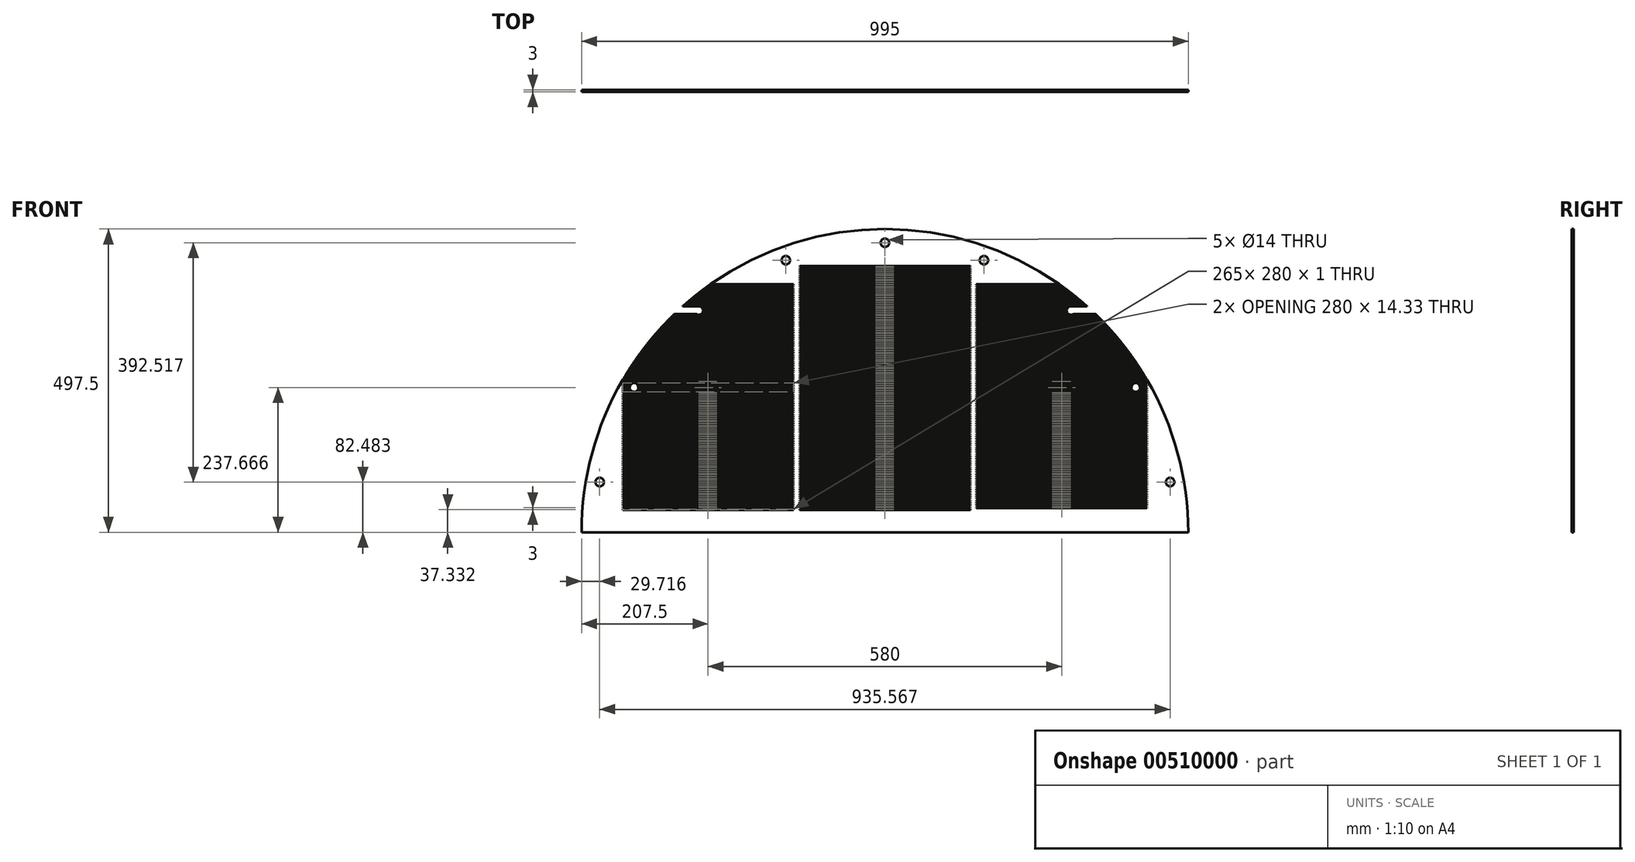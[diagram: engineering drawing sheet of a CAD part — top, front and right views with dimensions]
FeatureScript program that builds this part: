
annotation { "Feature Type Name" : "Feature", "Feature Type Description" : "" }
export const myFeature = defineFeature(function(context is Context, id is Id, definition is map)
    precondition{}
    {
        {
            var Q0;
            Q0=qCreatedBy(makeId("Front.planeOp"),FACE);
            var sketch = newSketch(context, id + "F0", { "sketchPlane" : qUnion([Q0])});
            skArc(sketch, "E0", {"start": v(497.5, 0) * mm, "mid": v(0, 497.5) * mm, "end": v(-497.5, 0) * mm});
            skLineSegment(sketch, "E1", {"start": v(-497.5, 0) * mm, "end": v(497.5, 0) * mm});
            skSolve(sketch);
        }
        {
            var Q0;
            Q0=makeQuery(id+"F0.imprint","IMPRINT",FACE,{"disambiguationData":[TD([[makeQuery(id+"F0.imprint","IMPRINT",EDGE,{"derivedFrom":sQuery(id+"F0.wireOp",EDGE,"E0")}),1.0]])]});
            extrude(context, id + "F1", {"entities" : qUnion([Q0]), "depth" : 3 * mm});
        }
        {
            var Q0;
            Q0=makeQuery(id+"F1.opExtrude","CAP_FACE",FACE,{"disambiguationData":[OSD([sQuery(id+"F0.wireOp",EDGE,"E0"),sQuery(id+"F0.wireOp",EDGE,"E1")])],"isStart":false});
            var sketch = newSketch(context, id + "F2", { "sketchPlane" : qUnion([Q0])});
            skCircle(sketch, "E2", {"center": v(0, 0) * mm, "radius": 475 * mm, "construction": true});
            skLineSegment(sketch, "E3", {"start": v(0, 0) * mm, "end": v(-467.78, 82.48) * mm});
            skCircle(sketch, "E4", {"center": v(-467.78, 82.48) * mm, "radius": 7 * mm});
            skCircle(sketch, "E5.1.0", {"center": v(-411.36, 237.5) * mm, "radius": 7 * mm});
            skCircle(sketch, "E5.2.0", {"center": v(-305.32, 363.87) * mm, "radius": 7 * mm});
            skCircle(sketch, "E5.3.0", {"center": v(-162.46, 446.35) * mm, "radius": 7 * mm});
            skCircle(sketch, "E5.4.0", {"center": v(0, 475) * mm, "radius": 7 * mm});
            skCircle(sketch, "E5.5.0", {"center": v(162.46, 446.35) * mm, "radius": 7 * mm});
            skCircle(sketch, "E5.6.0", {"center": v(305.32, 363.87) * mm, "radius": 7 * mm});
            skCircle(sketch, "E5.7.0", {"center": v(411.36, 237.5) * mm, "radius": 7 * mm});
            skCircle(sketch, "E5.8.0", {"center": v(467.78, 82.48) * mm, "radius": 7 * mm});
            skLineSegment(sketch, "E5.anchor1", {"start": v(0, 0) * mm, "end": v(-467.78, 82.48) * mm, "construction": true});
            skLineSegment(sketch, "E5.anchor2", {"start": v(0, 0) * mm, "end": v(467.78, 82.48) * mm, "construction": true});
            skSolve(sketch);
        }
        {
            var Q0;
            Q0=makeQuery(id+"F2.imprint","IMPRINT",FACE,{"disambiguationData":[TD([[makeQuery(id+"F2.imprint","IMPRINT",EDGE,{"derivedFrom":sQuery(id+"F2.wireOp",EDGE,"E4")}),-1.0]])]});
            extrude(context, id + "F3", {"entities" : qUnion([Q0]), "operationType" : NewBodyOperationType.INTERSECT, "oppositeDirection" : true, "depth" : 25 * mm});
        }
        {
            var Q0;
            Q0=makeQuery(id+"F1.opExtrude","CAP_FACE",FACE,{"disambiguationData":[OSD([sQuery(id+"F0.wireOp",EDGE,"E0"),sQuery(id+"F0.wireOp",EDGE,"E1")])],"isStart":false});
            var sketch = newSketch(context, id + "F4", { "sketchPlane" : qUnion([Q0])});
            skSolve(sketch);
        }
        {
            var Q0;
            Q0=makeQuery(id+"F4.imprint","IMPRINT",FACE,{"disambiguationData":[TD([[makeQuery(id+"F4.imprint","IMPRINT",EDGE,{"derivedFrom":makeQuery(id+"F1.opExtrude","CAP_EDGE",EDGE,{"disambiguationData":[OSD([sQuery(id+"F0.wireOp",EDGE,"E0")])],"isStart":false})}),1.0]])]});
            var sketch = newSketch(context, id + "F5", { "sketchPlane" : qUnion([Q0])});
            skLineSegment(sketch, "E6.bottom", {"start": v(-430, 37.83) * mm, "end": v(-150, 37.83) * mm});
            skLineSegment(sketch, "E6.top", {"start": v(-430, 36.83) * mm, "end": v(-150, 36.83) * mm});
            skLineSegment(sketch, "E6.left", {"start": v(-430, 37.83) * mm, "end": v(-430, 36.83) * mm});
            skLineSegment(sketch, "E6.right", {"start": v(-150, 37.83) * mm, "end": v(-150, 36.83) * mm});
            skLineSegment(sketch, "E7.bottom", {"start": v(-140, 36.83) * mm, "end": v(140, 36.83) * mm});
            skLineSegment(sketch, "E7.top", {"start": v(-140, 37.83) * mm, "end": v(140, 37.83) * mm});
            skLineSegment(sketch, "E7.left", {"start": v(-140, 36.83) * mm, "end": v(-140, 37.83) * mm});
            skLineSegment(sketch, "E7.right", {"start": v(140, 36.83) * mm, "end": v(140, 37.83) * mm});
            skLineSegment(sketch, "E8.bottom", {"start": v(150, 36.83) * mm, "end": v(430, 36.83) * mm});
            skLineSegment(sketch, "E8.top", {"start": v(150, 37.83) * mm, "end": v(430, 37.83) * mm});
            skLineSegment(sketch, "E8.left", {"start": v(150, 36.83) * mm, "end": v(150, 37.83) * mm});
            skLineSegment(sketch, "E9.0.1.0", {"start": v(150, 40.83) * mm, "end": v(429.64, 40.83) * mm});
            skLineSegment(sketch, "E9.0.1.1", {"start": v(-140, 40.83) * mm, "end": v(140, 40.83) * mm});
            skLineSegment(sketch, "E9.0.1.2", {"start": v(-430, 39.83) * mm, "end": v(-150, 39.83) * mm});
            skLineSegment(sketch, "E9.0.1.3", {"start": v(150, 39.83) * mm, "end": v(429.73, 39.83) * mm});
            skLineSegment(sketch, "E9.0.1.4", {"start": v(-140, 39.83) * mm, "end": v(140, 39.83) * mm});
            skLineSegment(sketch, "E9.0.1.5", {"start": v(-430, 40.83) * mm, "end": v(-150, 40.83) * mm});
            skLineSegment(sketch, "E9.0.1.7", {"start": v(150, 39.83) * mm, "end": v(150, 40.83) * mm});
            skLineSegment(sketch, "E9.0.1.8", {"start": v(140, 39.83) * mm, "end": v(140, 40.83) * mm});
            skLineSegment(sketch, "E9.0.1.9", {"start": v(-140, 39.83) * mm, "end": v(-140, 40.83) * mm});
            skLineSegment(sketch, "E9.0.1.10", {"start": v(-150, 40.83) * mm, "end": v(-150, 39.83) * mm});
            skLineSegment(sketch, "E9.0.1.11", {"start": v(-430, 40.83) * mm, "end": v(-430, 39.83) * mm});
            skLineSegment(sketch, "E9.0.2.0", {"start": v(150, 43.83) * mm, "end": v(429.34, 43.83) * mm});
            skLineSegment(sketch, "E9.0.2.1", {"start": v(-140, 43.83) * mm, "end": v(140, 43.83) * mm});
            skLineSegment(sketch, "E9.0.2.2", {"start": v(-430, 42.83) * mm, "end": v(-150, 42.83) * mm});
            skLineSegment(sketch, "E9.0.2.3", {"start": v(150, 42.83) * mm, "end": v(429.44, 42.83) * mm});
            skLineSegment(sketch, "E9.0.2.4", {"start": v(-140, 42.83) * mm, "end": v(140, 42.83) * mm});
            skLineSegment(sketch, "E9.0.2.5", {"start": v(-430, 43.83) * mm, "end": v(-150, 43.83) * mm});
            skLineSegment(sketch, "E9.0.2.7", {"start": v(150, 42.83) * mm, "end": v(150, 43.83) * mm});
            skLineSegment(sketch, "E9.0.2.8", {"start": v(140, 42.83) * mm, "end": v(140, 43.83) * mm});
            skLineSegment(sketch, "E9.0.2.9", {"start": v(-140, 42.83) * mm, "end": v(-140, 43.83) * mm});
            skLineSegment(sketch, "E9.0.2.10", {"start": v(-150, 43.83) * mm, "end": v(-150, 42.83) * mm});
            skLineSegment(sketch, "E9.0.2.11", {"start": v(-430, 43.83) * mm, "end": v(-430, 42.83) * mm});
            skLineSegment(sketch, "E9.0.3.0", {"start": v(150, 46.83) * mm, "end": v(429.03, 46.83) * mm});
            skLineSegment(sketch, "E9.0.3.1", {"start": v(-140, 46.83) * mm, "end": v(140, 46.83) * mm});
            skLineSegment(sketch, "E9.0.3.2", {"start": v(-430, 45.83) * mm, "end": v(-150, 45.83) * mm});
            skLineSegment(sketch, "E9.0.3.3", {"start": v(150, 45.83) * mm, "end": v(429.13, 45.83) * mm});
            skLineSegment(sketch, "E9.0.3.4", {"start": v(-140, 45.83) * mm, "end": v(140, 45.83) * mm});
            skLineSegment(sketch, "E9.0.3.5", {"start": v(-430, 46.83) * mm, "end": v(-150, 46.83) * mm});
            skLineSegment(sketch, "E9.0.3.7", {"start": v(150, 45.83) * mm, "end": v(150, 46.83) * mm});
            skLineSegment(sketch, "E9.0.3.8", {"start": v(140, 45.83) * mm, "end": v(140, 46.83) * mm});
            skLineSegment(sketch, "E9.0.3.9", {"start": v(-140, 45.83) * mm, "end": v(-140, 46.83) * mm});
            skLineSegment(sketch, "E9.0.3.10", {"start": v(-150, 46.83) * mm, "end": v(-150, 45.83) * mm});
            skLineSegment(sketch, "E9.0.3.11", {"start": v(-430, 46.83) * mm, "end": v(-430, 45.83) * mm});
            skLineSegment(sketch, "E9.0.4.0", {"start": v(150, 49.83) * mm, "end": v(430, 49.83) * mm});
            skLineSegment(sketch, "E9.0.4.1", {"start": v(-140, 49.83) * mm, "end": v(140, 49.83) * mm});
            skLineSegment(sketch, "E9.0.4.2", {"start": v(-430, 48.83) * mm, "end": v(-150, 48.83) * mm});
            skLineSegment(sketch, "E9.0.4.3", {"start": v(150, 48.83) * mm, "end": v(430, 48.83) * mm});
            skLineSegment(sketch, "E9.0.4.4", {"start": v(-140, 48.83) * mm, "end": v(140, 48.83) * mm});
            skLineSegment(sketch, "E9.0.4.5", {"start": v(-430, 49.83) * mm, "end": v(-150, 49.83) * mm});
            skLineSegment(sketch, "E9.0.4.6", {"start": v(430, 48.83) * mm, "end": v(430, 49.83) * mm});
            skLineSegment(sketch, "E9.0.4.7", {"start": v(150, 48.83) * mm, "end": v(150, 49.83) * mm});
            skLineSegment(sketch, "E9.0.4.8", {"start": v(140, 48.83) * mm, "end": v(140, 49.83) * mm});
            skLineSegment(sketch, "E9.0.4.9", {"start": v(-140, 48.83) * mm, "end": v(-140, 49.83) * mm});
            skLineSegment(sketch, "E9.0.4.10", {"start": v(-150, 49.83) * mm, "end": v(-150, 48.83) * mm});
            skLineSegment(sketch, "E9.0.4.11", {"start": v(-430, 49.83) * mm, "end": v(-430, 48.83) * mm});
            skLineSegment(sketch, "E9.0.5.0", {"start": v(150, 52.83) * mm, "end": v(430, 52.83) * mm});
            skLineSegment(sketch, "E9.0.5.1", {"start": v(-140, 52.83) * mm, "end": v(140, 52.83) * mm});
            skLineSegment(sketch, "E9.0.5.2", {"start": v(-430, 51.83) * mm, "end": v(-150, 51.83) * mm});
            skLineSegment(sketch, "E9.0.5.3", {"start": v(150, 51.83) * mm, "end": v(430, 51.83) * mm});
            skLineSegment(sketch, "E9.0.5.4", {"start": v(-140, 51.83) * mm, "end": v(140, 51.83) * mm});
            skLineSegment(sketch, "E9.0.5.5", {"start": v(-430, 52.83) * mm, "end": v(-150, 52.83) * mm});
            skLineSegment(sketch, "E9.0.5.6", {"start": v(430, 51.83) * mm, "end": v(430, 52.83) * mm});
            skLineSegment(sketch, "E9.0.5.7", {"start": v(150, 51.83) * mm, "end": v(150, 52.83) * mm});
            skLineSegment(sketch, "E9.0.5.8", {"start": v(140, 51.83) * mm, "end": v(140, 52.83) * mm});
            skLineSegment(sketch, "E9.0.5.9", {"start": v(-140, 51.83) * mm, "end": v(-140, 52.83) * mm});
            skLineSegment(sketch, "E9.0.5.10", {"start": v(-150, 52.83) * mm, "end": v(-150, 51.83) * mm});
            skLineSegment(sketch, "E9.0.5.11", {"start": v(-430, 52.83) * mm, "end": v(-430, 51.83) * mm});
            skLineSegment(sketch, "E9.0.6.0", {"start": v(150, 55.83) * mm, "end": v(430, 55.83) * mm});
            skLineSegment(sketch, "E9.0.6.1", {"start": v(-140, 55.83) * mm, "end": v(140, 55.83) * mm});
            skLineSegment(sketch, "E9.0.6.2", {"start": v(-430, 54.83) * mm, "end": v(-150, 54.83) * mm});
            skLineSegment(sketch, "E9.0.6.3", {"start": v(150, 54.83) * mm, "end": v(430, 54.83) * mm});
            skLineSegment(sketch, "E9.0.6.4", {"start": v(-140, 54.83) * mm, "end": v(140, 54.83) * mm});
            skLineSegment(sketch, "E9.0.6.5", {"start": v(-430, 55.83) * mm, "end": v(-150, 55.83) * mm});
            skLineSegment(sketch, "E9.0.6.6", {"start": v(430, 54.83) * mm, "end": v(430, 55.83) * mm});
            skLineSegment(sketch, "E9.0.6.7", {"start": v(150, 54.83) * mm, "end": v(150, 55.83) * mm});
            skLineSegment(sketch, "E9.0.6.8", {"start": v(140, 54.83) * mm, "end": v(140, 55.83) * mm});
            skLineSegment(sketch, "E9.0.6.9", {"start": v(-140, 54.83) * mm, "end": v(-140, 55.83) * mm});
            skLineSegment(sketch, "E9.0.6.10", {"start": v(-150, 55.83) * mm, "end": v(-150, 54.83) * mm});
            skLineSegment(sketch, "E9.0.6.11", {"start": v(-430, 55.83) * mm, "end": v(-430, 54.83) * mm});
            skLineSegment(sketch, "E9.0.7.0", {"start": v(150, 58.83) * mm, "end": v(430, 58.83) * mm});
            skLineSegment(sketch, "E9.0.7.1", {"start": v(-140, 58.83) * mm, "end": v(140, 58.83) * mm});
            skLineSegment(sketch, "E9.0.7.2", {"start": v(-430, 57.83) * mm, "end": v(-150, 57.83) * mm});
            skLineSegment(sketch, "E9.0.7.3", {"start": v(150, 57.83) * mm, "end": v(430, 57.83) * mm});
            skLineSegment(sketch, "E9.0.7.4", {"start": v(-140, 57.83) * mm, "end": v(140, 57.83) * mm});
            skLineSegment(sketch, "E9.0.7.5", {"start": v(-430, 58.83) * mm, "end": v(-150, 58.83) * mm});
            skLineSegment(sketch, "E9.0.7.6", {"start": v(430, 57.83) * mm, "end": v(430, 58.83) * mm});
            skLineSegment(sketch, "E9.0.7.7", {"start": v(150, 57.83) * mm, "end": v(150, 58.83) * mm});
            skLineSegment(sketch, "E9.0.7.8", {"start": v(140, 57.83) * mm, "end": v(140, 58.83) * mm});
            skLineSegment(sketch, "E9.0.7.9", {"start": v(-140, 57.83) * mm, "end": v(-140, 58.83) * mm});
            skLineSegment(sketch, "E9.0.7.10", {"start": v(-150, 58.83) * mm, "end": v(-150, 57.83) * mm});
            skLineSegment(sketch, "E9.0.7.11", {"start": v(-430, 58.83) * mm, "end": v(-430, 57.83) * mm});
            skLineSegment(sketch, "E9.0.8.0", {"start": v(150, 61.83) * mm, "end": v(430, 61.83) * mm});
            skLineSegment(sketch, "E9.0.8.1", {"start": v(-140, 61.83) * mm, "end": v(140, 61.83) * mm});
            skLineSegment(sketch, "E9.0.8.2", {"start": v(-430, 60.83) * mm, "end": v(-150, 60.83) * mm});
            skLineSegment(sketch, "E9.0.8.3", {"start": v(150, 60.83) * mm, "end": v(430, 60.83) * mm});
            skLineSegment(sketch, "E9.0.8.4", {"start": v(-140, 60.83) * mm, "end": v(140, 60.83) * mm});
            skLineSegment(sketch, "E9.0.8.5", {"start": v(-430, 61.83) * mm, "end": v(-150, 61.83) * mm});
            skLineSegment(sketch, "E9.0.8.6", {"start": v(430, 60.83) * mm, "end": v(430, 61.83) * mm});
            skLineSegment(sketch, "E9.0.8.7", {"start": v(150, 60.83) * mm, "end": v(150, 61.83) * mm});
            skLineSegment(sketch, "E9.0.8.8", {"start": v(140, 60.83) * mm, "end": v(140, 61.83) * mm});
            skLineSegment(sketch, "E9.0.8.9", {"start": v(-140, 60.83) * mm, "end": v(-140, 61.83) * mm});
            skLineSegment(sketch, "E9.0.8.10", {"start": v(-150, 61.83) * mm, "end": v(-150, 60.83) * mm});
            skLineSegment(sketch, "E9.0.8.11", {"start": v(-430, 61.83) * mm, "end": v(-430, 60.83) * mm});
            skLineSegment(sketch, "E9.0.9.0", {"start": v(150, 64.83) * mm, "end": v(430, 64.83) * mm});
            skLineSegment(sketch, "E9.0.9.1", {"start": v(-140, 64.83) * mm, "end": v(140, 64.83) * mm});
            skLineSegment(sketch, "E9.0.9.2", {"start": v(-430, 63.83) * mm, "end": v(-150, 63.83) * mm});
            skLineSegment(sketch, "E9.0.9.3", {"start": v(150, 63.83) * mm, "end": v(430, 63.83) * mm});
            skLineSegment(sketch, "E9.0.9.4", {"start": v(-140, 63.83) * mm, "end": v(140, 63.83) * mm});
            skLineSegment(sketch, "E9.0.9.5", {"start": v(-430, 64.83) * mm, "end": v(-150, 64.83) * mm});
            skLineSegment(sketch, "E9.0.9.6", {"start": v(430, 63.83) * mm, "end": v(430, 64.83) * mm});
            skLineSegment(sketch, "E9.0.9.7", {"start": v(150, 63.83) * mm, "end": v(150, 64.83) * mm});
            skLineSegment(sketch, "E9.0.9.8", {"start": v(140, 63.83) * mm, "end": v(140, 64.83) * mm});
            skLineSegment(sketch, "E9.0.9.9", {"start": v(-140, 63.83) * mm, "end": v(-140, 64.83) * mm});
            skLineSegment(sketch, "E9.0.9.10", {"start": v(-150, 64.83) * mm, "end": v(-150, 63.83) * mm});
            skLineSegment(sketch, "E9.0.9.11", {"start": v(-430, 64.83) * mm, "end": v(-430, 63.83) * mm});
            skLineSegment(sketch, "E9.0.10.0", {"start": v(150, 67.83) * mm, "end": v(430, 67.83) * mm});
            skLineSegment(sketch, "E9.0.10.1", {"start": v(-140, 67.83) * mm, "end": v(140, 67.83) * mm});
            skLineSegment(sketch, "E9.0.10.2", {"start": v(-430, 66.83) * mm, "end": v(-150, 66.83) * mm});
            skLineSegment(sketch, "E9.0.10.3", {"start": v(150, 66.83) * mm, "end": v(430, 66.83) * mm});
            skLineSegment(sketch, "E9.0.10.4", {"start": v(-140, 66.83) * mm, "end": v(140, 66.83) * mm});
            skLineSegment(sketch, "E9.0.10.5", {"start": v(-430, 67.83) * mm, "end": v(-150, 67.83) * mm});
            skLineSegment(sketch, "E9.0.10.6", {"start": v(430, 66.83) * mm, "end": v(430, 67.83) * mm});
            skLineSegment(sketch, "E9.0.10.7", {"start": v(150, 66.83) * mm, "end": v(150, 67.83) * mm});
            skLineSegment(sketch, "E9.0.10.8", {"start": v(140, 66.83) * mm, "end": v(140, 67.83) * mm});
            skLineSegment(sketch, "E9.0.10.9", {"start": v(-140, 66.83) * mm, "end": v(-140, 67.83) * mm});
            skLineSegment(sketch, "E9.0.10.10", {"start": v(-150, 67.83) * mm, "end": v(-150, 66.83) * mm});
            skLineSegment(sketch, "E9.0.10.11", {"start": v(-430, 67.83) * mm, "end": v(-430, 66.83) * mm});
            skLineSegment(sketch, "E9.0.11.0", {"start": v(150, 70.83) * mm, "end": v(430, 70.83) * mm});
            skLineSegment(sketch, "E9.0.11.1", {"start": v(-140, 70.83) * mm, "end": v(140, 70.83) * mm});
            skLineSegment(sketch, "E9.0.11.2", {"start": v(-430, 69.83) * mm, "end": v(-150, 69.83) * mm});
            skLineSegment(sketch, "E9.0.11.3", {"start": v(150, 69.83) * mm, "end": v(430, 69.83) * mm});
            skLineSegment(sketch, "E9.0.11.4", {"start": v(-140, 69.83) * mm, "end": v(140, 69.83) * mm});
            skLineSegment(sketch, "E9.0.11.5", {"start": v(-430, 70.83) * mm, "end": v(-150, 70.83) * mm});
            skLineSegment(sketch, "E9.0.11.6", {"start": v(430, 69.83) * mm, "end": v(430, 70.83) * mm});
            skLineSegment(sketch, "E9.0.11.7", {"start": v(150, 69.83) * mm, "end": v(150, 70.83) * mm});
            skLineSegment(sketch, "E9.0.11.8", {"start": v(140, 69.83) * mm, "end": v(140, 70.83) * mm});
            skLineSegment(sketch, "E9.0.11.9", {"start": v(-140, 69.83) * mm, "end": v(-140, 70.83) * mm});
            skLineSegment(sketch, "E9.0.11.10", {"start": v(-150, 70.83) * mm, "end": v(-150, 69.83) * mm});
            skLineSegment(sketch, "E9.0.11.11", {"start": v(-430, 70.83) * mm, "end": v(-430, 69.83) * mm});
            skLineSegment(sketch, "E9.0.12.0", {"start": v(150, 73.83) * mm, "end": v(430, 73.83) * mm});
            skLineSegment(sketch, "E9.0.12.1", {"start": v(-140, 73.83) * mm, "end": v(140, 73.83) * mm});
            skLineSegment(sketch, "E9.0.12.2", {"start": v(-430, 72.83) * mm, "end": v(-150, 72.83) * mm});
            skLineSegment(sketch, "E9.0.12.3", {"start": v(150, 72.83) * mm, "end": v(430, 72.83) * mm});
            skLineSegment(sketch, "E9.0.12.4", {"start": v(-140, 72.83) * mm, "end": v(140, 72.83) * mm});
            skLineSegment(sketch, "E9.0.12.5", {"start": v(-430, 73.83) * mm, "end": v(-150, 73.83) * mm});
            skLineSegment(sketch, "E9.0.12.6", {"start": v(430, 72.83) * mm, "end": v(430, 73.83) * mm});
            skLineSegment(sketch, "E9.0.12.7", {"start": v(150, 72.83) * mm, "end": v(150, 73.83) * mm});
            skLineSegment(sketch, "E9.0.12.8", {"start": v(140, 72.83) * mm, "end": v(140, 73.83) * mm});
            skLineSegment(sketch, "E9.0.12.9", {"start": v(-140, 72.83) * mm, "end": v(-140, 73.83) * mm});
            skLineSegment(sketch, "E9.0.12.10", {"start": v(-150, 73.83) * mm, "end": v(-150, 72.83) * mm});
            skLineSegment(sketch, "E9.0.12.11", {"start": v(-430, 73.83) * mm, "end": v(-430, 72.83) * mm});
            skLineSegment(sketch, "E9.0.13.0", {"start": v(150, 76.83) * mm, "end": v(430, 76.83) * mm});
            skLineSegment(sketch, "E9.0.13.1", {"start": v(-140, 76.83) * mm, "end": v(140, 76.83) * mm});
            skLineSegment(sketch, "E9.0.13.2", {"start": v(-430, 75.83) * mm, "end": v(-150, 75.83) * mm});
            skLineSegment(sketch, "E9.0.13.3", {"start": v(150, 75.83) * mm, "end": v(430, 75.83) * mm});
            skLineSegment(sketch, "E9.0.13.4", {"start": v(-140, 75.83) * mm, "end": v(140, 75.83) * mm});
            skLineSegment(sketch, "E9.0.13.5", {"start": v(-430, 76.83) * mm, "end": v(-150, 76.83) * mm});
            skLineSegment(sketch, "E9.0.13.6", {"start": v(430, 75.83) * mm, "end": v(430, 76.83) * mm});
            skLineSegment(sketch, "E9.0.13.7", {"start": v(150, 75.83) * mm, "end": v(150, 76.83) * mm});
            skLineSegment(sketch, "E9.0.13.8", {"start": v(140, 75.83) * mm, "end": v(140, 76.83) * mm});
            skLineSegment(sketch, "E9.0.13.9", {"start": v(-140, 75.83) * mm, "end": v(-140, 76.83) * mm});
            skLineSegment(sketch, "E9.0.13.10", {"start": v(-150, 76.83) * mm, "end": v(-150, 75.83) * mm});
            skLineSegment(sketch, "E9.0.13.11", {"start": v(-430, 76.83) * mm, "end": v(-430, 75.83) * mm});
            skLineSegment(sketch, "E9.0.14.0", {"start": v(150, 79.83) * mm, "end": v(430, 79.83) * mm});
            skLineSegment(sketch, "E9.0.14.1", {"start": v(-140, 79.83) * mm, "end": v(140, 79.83) * mm});
            skLineSegment(sketch, "E9.0.14.2", {"start": v(-430, 78.83) * mm, "end": v(-150, 78.83) * mm});
            skLineSegment(sketch, "E9.0.14.3", {"start": v(150, 78.83) * mm, "end": v(430, 78.83) * mm});
            skLineSegment(sketch, "E9.0.14.4", {"start": v(-140, 78.83) * mm, "end": v(140, 78.83) * mm});
            skLineSegment(sketch, "E9.0.14.5", {"start": v(-430, 79.83) * mm, "end": v(-150, 79.83) * mm});
            skLineSegment(sketch, "E9.0.14.6", {"start": v(430, 78.83) * mm, "end": v(430, 79.83) * mm});
            skLineSegment(sketch, "E9.0.14.7", {"start": v(150, 78.83) * mm, "end": v(150, 79.83) * mm});
            skLineSegment(sketch, "E9.0.14.8", {"start": v(140, 78.83) * mm, "end": v(140, 79.83) * mm});
            skLineSegment(sketch, "E9.0.14.9", {"start": v(-140, 78.83) * mm, "end": v(-140, 79.83) * mm});
            skLineSegment(sketch, "E9.0.14.10", {"start": v(-150, 79.83) * mm, "end": v(-150, 78.83) * mm});
            skLineSegment(sketch, "E9.0.14.11", {"start": v(-430, 79.83) * mm, "end": v(-430, 78.83) * mm});
            skLineSegment(sketch, "E9.0.15.0", {"start": v(150, 82.83) * mm, "end": v(430, 82.83) * mm});
            skLineSegment(sketch, "E9.0.15.1", {"start": v(-140, 82.83) * mm, "end": v(140, 82.83) * mm});
            skLineSegment(sketch, "E9.0.15.2", {"start": v(-430, 81.83) * mm, "end": v(-150, 81.83) * mm});
            skLineSegment(sketch, "E9.0.15.3", {"start": v(150, 81.83) * mm, "end": v(430, 81.83) * mm});
            skLineSegment(sketch, "E9.0.15.4", {"start": v(-140, 81.83) * mm, "end": v(140, 81.83) * mm});
            skLineSegment(sketch, "E9.0.15.5", {"start": v(-430, 82.83) * mm, "end": v(-150, 82.83) * mm});
            skLineSegment(sketch, "E9.0.15.6", {"start": v(430, 81.83) * mm, "end": v(430, 82.83) * mm});
            skLineSegment(sketch, "E9.0.15.7", {"start": v(150, 81.83) * mm, "end": v(150, 82.83) * mm});
            skLineSegment(sketch, "E9.0.15.8", {"start": v(140, 81.83) * mm, "end": v(140, 82.83) * mm});
            skLineSegment(sketch, "E9.0.15.9", {"start": v(-140, 81.83) * mm, "end": v(-140, 82.83) * mm});
            skLineSegment(sketch, "E9.0.15.10", {"start": v(-150, 82.83) * mm, "end": v(-150, 81.83) * mm});
            skLineSegment(sketch, "E9.0.15.11", {"start": v(-430, 82.83) * mm, "end": v(-430, 81.83) * mm});
            skLineSegment(sketch, "E9.0.16.0", {"start": v(150, 85.83) * mm, "end": v(430, 85.83) * mm});
            skLineSegment(sketch, "E9.0.16.1", {"start": v(-140, 85.83) * mm, "end": v(140, 85.83) * mm});
            skLineSegment(sketch, "E9.0.16.2", {"start": v(-430, 84.83) * mm, "end": v(-150, 84.83) * mm});
            skLineSegment(sketch, "E9.0.16.3", {"start": v(150, 84.83) * mm, "end": v(430, 84.83) * mm});
            skLineSegment(sketch, "E9.0.16.4", {"start": v(-140, 84.83) * mm, "end": v(140, 84.83) * mm});
            skLineSegment(sketch, "E9.0.16.5", {"start": v(-430, 85.83) * mm, "end": v(-150, 85.83) * mm});
            skLineSegment(sketch, "E9.0.16.6", {"start": v(430, 84.83) * mm, "end": v(430, 85.83) * mm});
            skLineSegment(sketch, "E9.0.16.7", {"start": v(150, 84.83) * mm, "end": v(150, 85.83) * mm});
            skLineSegment(sketch, "E9.0.16.8", {"start": v(140, 84.83) * mm, "end": v(140, 85.83) * mm});
            skLineSegment(sketch, "E9.0.16.9", {"start": v(-140, 84.83) * mm, "end": v(-140, 85.83) * mm});
            skLineSegment(sketch, "E9.0.16.10", {"start": v(-150, 85.83) * mm, "end": v(-150, 84.83) * mm});
            skLineSegment(sketch, "E9.0.16.11", {"start": v(-430, 85.83) * mm, "end": v(-430, 84.83) * mm});
            skLineSegment(sketch, "E9.0.17.0", {"start": v(150, 88.83) * mm, "end": v(430, 88.83) * mm});
            skLineSegment(sketch, "E9.0.17.1", {"start": v(-140, 88.83) * mm, "end": v(140, 88.83) * mm});
            skLineSegment(sketch, "E9.0.17.2", {"start": v(-430, 87.83) * mm, "end": v(-150, 87.83) * mm});
            skLineSegment(sketch, "E9.0.17.3", {"start": v(150, 87.83) * mm, "end": v(430, 87.83) * mm});
            skLineSegment(sketch, "E9.0.17.4", {"start": v(-140, 87.83) * mm, "end": v(140, 87.83) * mm});
            skLineSegment(sketch, "E9.0.17.5", {"start": v(-430, 88.83) * mm, "end": v(-150, 88.83) * mm});
            skLineSegment(sketch, "E9.0.17.6", {"start": v(430, 87.83) * mm, "end": v(430, 88.83) * mm});
            skLineSegment(sketch, "E9.0.17.7", {"start": v(150, 87.83) * mm, "end": v(150, 88.83) * mm});
            skLineSegment(sketch, "E9.0.17.8", {"start": v(140, 87.83) * mm, "end": v(140, 88.83) * mm});
            skLineSegment(sketch, "E9.0.17.9", {"start": v(-140, 87.83) * mm, "end": v(-140, 88.83) * mm});
            skLineSegment(sketch, "E9.0.17.10", {"start": v(-150, 88.83) * mm, "end": v(-150, 87.83) * mm});
            skLineSegment(sketch, "E9.0.17.11", {"start": v(-430, 88.83) * mm, "end": v(-430, 87.83) * mm});
            skLineSegment(sketch, "E9.0.18.0", {"start": v(150, 91.83) * mm, "end": v(430, 91.83) * mm});
            skLineSegment(sketch, "E9.0.18.1", {"start": v(-140, 91.83) * mm, "end": v(140, 91.83) * mm});
            skLineSegment(sketch, "E9.0.18.2", {"start": v(-430, 90.83) * mm, "end": v(-150, 90.83) * mm});
            skLineSegment(sketch, "E9.0.18.3", {"start": v(150, 90.83) * mm, "end": v(430, 90.83) * mm});
            skLineSegment(sketch, "E9.0.18.4", {"start": v(-140, 90.83) * mm, "end": v(140, 90.83) * mm});
            skLineSegment(sketch, "E9.0.18.5", {"start": v(-430, 91.83) * mm, "end": v(-150, 91.83) * mm});
            skLineSegment(sketch, "E9.0.18.6", {"start": v(430, 90.83) * mm, "end": v(430, 91.83) * mm});
            skLineSegment(sketch, "E9.0.18.7", {"start": v(150, 90.83) * mm, "end": v(150, 91.83) * mm});
            skLineSegment(sketch, "E9.0.18.8", {"start": v(140, 90.83) * mm, "end": v(140, 91.83) * mm});
            skLineSegment(sketch, "E9.0.18.9", {"start": v(-140, 90.83) * mm, "end": v(-140, 91.83) * mm});
            skLineSegment(sketch, "E9.0.18.10", {"start": v(-150, 91.83) * mm, "end": v(-150, 90.83) * mm});
            skLineSegment(sketch, "E9.0.18.11", {"start": v(-430, 91.83) * mm, "end": v(-430, 90.83) * mm});
            skLineSegment(sketch, "E9.0.19.0", {"start": v(150, 94.83) * mm, "end": v(430, 94.83) * mm});
            skLineSegment(sketch, "E9.0.19.1", {"start": v(-140, 94.83) * mm, "end": v(140, 94.83) * mm});
            skLineSegment(sketch, "E9.0.19.2", {"start": v(-430, 93.83) * mm, "end": v(-150, 93.83) * mm});
            skLineSegment(sketch, "E9.0.19.3", {"start": v(150, 93.83) * mm, "end": v(430, 93.83) * mm});
            skLineSegment(sketch, "E9.0.19.4", {"start": v(-140, 93.83) * mm, "end": v(140, 93.83) * mm});
            skLineSegment(sketch, "E9.0.19.5", {"start": v(-430, 94.83) * mm, "end": v(-150, 94.83) * mm});
            skLineSegment(sketch, "E9.0.19.6", {"start": v(430, 93.83) * mm, "end": v(430, 94.83) * mm});
            skLineSegment(sketch, "E9.0.19.7", {"start": v(150, 93.83) * mm, "end": v(150, 94.83) * mm});
            skLineSegment(sketch, "E9.0.19.8", {"start": v(140, 93.83) * mm, "end": v(140, 94.83) * mm});
            skLineSegment(sketch, "E9.0.19.9", {"start": v(-140, 93.83) * mm, "end": v(-140, 94.83) * mm});
            skLineSegment(sketch, "E9.0.19.10", {"start": v(-150, 94.83) * mm, "end": v(-150, 93.83) * mm});
            skLineSegment(sketch, "E9.0.19.11", {"start": v(-430, 94.83) * mm, "end": v(-430, 93.83) * mm});
            skLineSegment(sketch, "E9.0.20.0", {"start": v(150, 97.83) * mm, "end": v(430, 97.83) * mm});
            skLineSegment(sketch, "E9.0.20.1", {"start": v(-140, 97.83) * mm, "end": v(140, 97.83) * mm});
            skLineSegment(sketch, "E9.0.20.2", {"start": v(-430, 96.83) * mm, "end": v(-150, 96.83) * mm});
            skLineSegment(sketch, "E9.0.20.3", {"start": v(150, 96.83) * mm, "end": v(430, 96.83) * mm});
            skLineSegment(sketch, "E9.0.20.4", {"start": v(-140, 96.83) * mm, "end": v(140, 96.83) * mm});
            skLineSegment(sketch, "E9.0.20.5", {"start": v(-430, 97.83) * mm, "end": v(-150, 97.83) * mm});
            skLineSegment(sketch, "E9.0.20.6", {"start": v(430, 96.83) * mm, "end": v(430, 97.83) * mm});
            skLineSegment(sketch, "E9.0.20.7", {"start": v(150, 96.83) * mm, "end": v(150, 97.83) * mm});
            skLineSegment(sketch, "E9.0.20.8", {"start": v(140, 96.83) * mm, "end": v(140, 97.83) * mm});
            skLineSegment(sketch, "E9.0.20.9", {"start": v(-140, 96.83) * mm, "end": v(-140, 97.83) * mm});
            skLineSegment(sketch, "E9.0.20.10", {"start": v(-150, 97.83) * mm, "end": v(-150, 96.83) * mm});
            skLineSegment(sketch, "E9.0.20.11", {"start": v(-430, 97.83) * mm, "end": v(-430, 96.83) * mm});
            skLineSegment(sketch, "E9.0.21.0", {"start": v(150, 100.83) * mm, "end": v(430, 100.83) * mm});
            skLineSegment(sketch, "E9.0.21.1", {"start": v(-140, 100.83) * mm, "end": v(140, 100.83) * mm});
            skLineSegment(sketch, "E9.0.21.2", {"start": v(-430, 99.83) * mm, "end": v(-150, 99.83) * mm});
            skLineSegment(sketch, "E9.0.21.3", {"start": v(150, 99.83) * mm, "end": v(430, 99.83) * mm});
            skLineSegment(sketch, "E9.0.21.4", {"start": v(-140, 99.83) * mm, "end": v(140, 99.83) * mm});
            skLineSegment(sketch, "E9.0.21.5", {"start": v(-430, 100.83) * mm, "end": v(-150, 100.83) * mm});
            skLineSegment(sketch, "E9.0.21.6", {"start": v(430, 99.83) * mm, "end": v(430, 100.83) * mm});
            skLineSegment(sketch, "E9.0.21.7", {"start": v(150, 99.83) * mm, "end": v(150, 100.83) * mm});
            skLineSegment(sketch, "E9.0.21.8", {"start": v(140, 99.83) * mm, "end": v(140, 100.83) * mm});
            skLineSegment(sketch, "E9.0.21.9", {"start": v(-140, 99.83) * mm, "end": v(-140, 100.83) * mm});
            skLineSegment(sketch, "E9.0.21.10", {"start": v(-150, 100.83) * mm, "end": v(-150, 99.83) * mm});
            skLineSegment(sketch, "E9.0.21.11", {"start": v(-430, 100.83) * mm, "end": v(-430, 99.83) * mm});
            skLineSegment(sketch, "E9.0.22.0", {"start": v(150, 103.83) * mm, "end": v(430, 103.83) * mm});
            skLineSegment(sketch, "E9.0.22.1", {"start": v(-140, 103.83) * mm, "end": v(140, 103.83) * mm});
            skLineSegment(sketch, "E9.0.22.2", {"start": v(-430, 102.83) * mm, "end": v(-150, 102.83) * mm});
            skLineSegment(sketch, "E9.0.22.3", {"start": v(150, 102.83) * mm, "end": v(430, 102.83) * mm});
            skLineSegment(sketch, "E9.0.22.4", {"start": v(-140, 102.83) * mm, "end": v(140, 102.83) * mm});
            skLineSegment(sketch, "E9.0.22.5", {"start": v(-430, 103.83) * mm, "end": v(-150, 103.83) * mm});
            skLineSegment(sketch, "E9.0.22.6", {"start": v(430, 102.83) * mm, "end": v(430, 103.83) * mm});
            skLineSegment(sketch, "E9.0.22.7", {"start": v(150, 102.83) * mm, "end": v(150, 103.83) * mm});
            skLineSegment(sketch, "E9.0.22.8", {"start": v(140, 102.83) * mm, "end": v(140, 103.83) * mm});
            skLineSegment(sketch, "E9.0.22.9", {"start": v(-140, 102.83) * mm, "end": v(-140, 103.83) * mm});
            skLineSegment(sketch, "E9.0.22.10", {"start": v(-150, 103.83) * mm, "end": v(-150, 102.83) * mm});
            skLineSegment(sketch, "E9.0.22.11", {"start": v(-430, 103.83) * mm, "end": v(-430, 102.83) * mm});
            skLineSegment(sketch, "E9.0.23.0", {"start": v(150, 106.83) * mm, "end": v(430, 106.83) * mm});
            skLineSegment(sketch, "E9.0.23.1", {"start": v(-140, 106.83) * mm, "end": v(140, 106.83) * mm});
            skLineSegment(sketch, "E9.0.23.2", {"start": v(-430, 105.83) * mm, "end": v(-150, 105.83) * mm});
            skLineSegment(sketch, "E9.0.23.3", {"start": v(150, 105.83) * mm, "end": v(430, 105.83) * mm});
            skLineSegment(sketch, "E9.0.23.4", {"start": v(-140, 105.83) * mm, "end": v(140, 105.83) * mm});
            skLineSegment(sketch, "E9.0.23.5", {"start": v(-430, 106.83) * mm, "end": v(-150, 106.83) * mm});
            skLineSegment(sketch, "E9.0.23.6", {"start": v(430, 105.83) * mm, "end": v(430, 106.83) * mm});
            skLineSegment(sketch, "E9.0.23.7", {"start": v(150, 105.83) * mm, "end": v(150, 106.83) * mm});
            skLineSegment(sketch, "E9.0.23.8", {"start": v(140, 105.83) * mm, "end": v(140, 106.83) * mm});
            skLineSegment(sketch, "E9.0.23.9", {"start": v(-140, 105.83) * mm, "end": v(-140, 106.83) * mm});
            skLineSegment(sketch, "E9.0.23.10", {"start": v(-150, 106.83) * mm, "end": v(-150, 105.83) * mm});
            skLineSegment(sketch, "E9.0.23.11", {"start": v(-430, 106.83) * mm, "end": v(-430, 105.83) * mm});
            skLineSegment(sketch, "E9.0.24.0", {"start": v(150, 109.83) * mm, "end": v(430, 109.83) * mm});
            skLineSegment(sketch, "E9.0.24.1", {"start": v(-140, 109.83) * mm, "end": v(140, 109.83) * mm});
            skLineSegment(sketch, "E9.0.24.2", {"start": v(-430, 108.83) * mm, "end": v(-150, 108.83) * mm});
            skLineSegment(sketch, "E9.0.24.3", {"start": v(150, 108.83) * mm, "end": v(430, 108.83) * mm});
            skLineSegment(sketch, "E9.0.24.4", {"start": v(-140, 108.83) * mm, "end": v(140, 108.83) * mm});
            skLineSegment(sketch, "E9.0.24.5", {"start": v(-430, 109.83) * mm, "end": v(-150, 109.83) * mm});
            skLineSegment(sketch, "E9.0.24.6", {"start": v(430, 108.83) * mm, "end": v(430, 109.83) * mm});
            skLineSegment(sketch, "E9.0.24.7", {"start": v(150, 108.83) * mm, "end": v(150, 109.83) * mm});
            skLineSegment(sketch, "E9.0.24.8", {"start": v(140, 108.83) * mm, "end": v(140, 109.83) * mm});
            skLineSegment(sketch, "E9.0.24.9", {"start": v(-140, 108.83) * mm, "end": v(-140, 109.83) * mm});
            skLineSegment(sketch, "E9.0.24.10", {"start": v(-150, 109.83) * mm, "end": v(-150, 108.83) * mm});
            skLineSegment(sketch, "E9.0.24.11", {"start": v(-430, 109.83) * mm, "end": v(-430, 108.83) * mm});
            skLineSegment(sketch, "E9.0.25.0", {"start": v(150, 112.83) * mm, "end": v(430, 112.83) * mm});
            skLineSegment(sketch, "E9.0.25.1", {"start": v(-140, 112.83) * mm, "end": v(140, 112.83) * mm});
            skLineSegment(sketch, "E9.0.25.2", {"start": v(-430, 111.83) * mm, "end": v(-150, 111.83) * mm});
            skLineSegment(sketch, "E9.0.25.3", {"start": v(150, 111.83) * mm, "end": v(430, 111.83) * mm});
            skLineSegment(sketch, "E9.0.25.4", {"start": v(-140, 111.83) * mm, "end": v(140, 111.83) * mm});
            skLineSegment(sketch, "E9.0.25.5", {"start": v(-430, 112.83) * mm, "end": v(-150, 112.83) * mm});
            skLineSegment(sketch, "E9.0.25.6", {"start": v(430, 111.83) * mm, "end": v(430, 112.83) * mm});
            skLineSegment(sketch, "E9.0.25.7", {"start": v(150, 111.83) * mm, "end": v(150, 112.83) * mm});
            skLineSegment(sketch, "E9.0.25.8", {"start": v(140, 111.83) * mm, "end": v(140, 112.83) * mm});
            skLineSegment(sketch, "E9.0.25.9", {"start": v(-140, 111.83) * mm, "end": v(-140, 112.83) * mm});
            skLineSegment(sketch, "E9.0.25.10", {"start": v(-150, 112.83) * mm, "end": v(-150, 111.83) * mm});
            skLineSegment(sketch, "E9.0.25.11", {"start": v(-430, 112.83) * mm, "end": v(-430, 111.83) * mm});
            skLineSegment(sketch, "E9.0.26.0", {"start": v(150, 115.83) * mm, "end": v(430, 115.83) * mm});
            skLineSegment(sketch, "E9.0.26.1", {"start": v(-140, 115.83) * mm, "end": v(140, 115.83) * mm});
            skLineSegment(sketch, "E9.0.26.2", {"start": v(-430, 114.83) * mm, "end": v(-150, 114.83) * mm});
            skLineSegment(sketch, "E9.0.26.3", {"start": v(150, 114.83) * mm, "end": v(430, 114.83) * mm});
            skLineSegment(sketch, "E9.0.26.4", {"start": v(-140, 114.83) * mm, "end": v(140, 114.83) * mm});
            skLineSegment(sketch, "E9.0.26.5", {"start": v(-430, 115.83) * mm, "end": v(-150, 115.83) * mm});
            skLineSegment(sketch, "E9.0.26.6", {"start": v(430, 114.83) * mm, "end": v(430, 115.83) * mm});
            skLineSegment(sketch, "E9.0.26.7", {"start": v(150, 114.83) * mm, "end": v(150, 115.83) * mm});
            skLineSegment(sketch, "E9.0.26.8", {"start": v(140, 114.83) * mm, "end": v(140, 115.83) * mm});
            skLineSegment(sketch, "E9.0.26.9", {"start": v(-140, 114.83) * mm, "end": v(-140, 115.83) * mm});
            skLineSegment(sketch, "E9.0.26.10", {"start": v(-150, 115.83) * mm, "end": v(-150, 114.83) * mm});
            skLineSegment(sketch, "E9.0.26.11", {"start": v(-430, 115.83) * mm, "end": v(-430, 114.83) * mm});
            skLineSegment(sketch, "E9.0.27.0", {"start": v(150, 118.83) * mm, "end": v(430, 118.83) * mm});
            skLineSegment(sketch, "E9.0.27.1", {"start": v(-140, 118.83) * mm, "end": v(140, 118.83) * mm});
            skLineSegment(sketch, "E9.0.27.2", {"start": v(-430, 117.83) * mm, "end": v(-150, 117.83) * mm});
            skLineSegment(sketch, "E9.0.27.3", {"start": v(150, 117.83) * mm, "end": v(430, 117.83) * mm});
            skLineSegment(sketch, "E9.0.27.4", {"start": v(-140, 117.83) * mm, "end": v(140, 117.83) * mm});
            skLineSegment(sketch, "E9.0.27.5", {"start": v(-430, 118.83) * mm, "end": v(-150, 118.83) * mm});
            skLineSegment(sketch, "E9.0.27.6", {"start": v(430, 117.83) * mm, "end": v(430, 118.83) * mm});
            skLineSegment(sketch, "E9.0.27.7", {"start": v(150, 117.83) * mm, "end": v(150, 118.83) * mm});
            skLineSegment(sketch, "E9.0.27.8", {"start": v(140, 117.83) * mm, "end": v(140, 118.83) * mm});
            skLineSegment(sketch, "E9.0.27.9", {"start": v(-140, 117.83) * mm, "end": v(-140, 118.83) * mm});
            skLineSegment(sketch, "E9.0.27.10", {"start": v(-150, 118.83) * mm, "end": v(-150, 117.83) * mm});
            skLineSegment(sketch, "E9.0.27.11", {"start": v(-430, 118.83) * mm, "end": v(-430, 117.83) * mm});
            skLineSegment(sketch, "E9.0.28.0", {"start": v(150, 121.83) * mm, "end": v(430, 121.83) * mm});
            skLineSegment(sketch, "E9.0.28.1", {"start": v(-140, 121.83) * mm, "end": v(140, 121.83) * mm});
            skLineSegment(sketch, "E9.0.28.2", {"start": v(-430, 120.83) * mm, "end": v(-150, 120.83) * mm});
            skLineSegment(sketch, "E9.0.28.3", {"start": v(150, 120.83) * mm, "end": v(430, 120.83) * mm});
            skLineSegment(sketch, "E9.0.28.4", {"start": v(-140, 120.83) * mm, "end": v(140, 120.83) * mm});
            skLineSegment(sketch, "E9.0.28.5", {"start": v(-430, 121.83) * mm, "end": v(-150, 121.83) * mm});
            skLineSegment(sketch, "E9.0.28.6", {"start": v(430, 120.83) * mm, "end": v(430, 121.83) * mm});
            skLineSegment(sketch, "E9.0.28.7", {"start": v(150, 120.83) * mm, "end": v(150, 121.83) * mm});
            skLineSegment(sketch, "E9.0.28.8", {"start": v(140, 120.83) * mm, "end": v(140, 121.83) * mm});
            skLineSegment(sketch, "E9.0.28.9", {"start": v(-140, 120.83) * mm, "end": v(-140, 121.83) * mm});
            skLineSegment(sketch, "E9.0.28.10", {"start": v(-150, 121.83) * mm, "end": v(-150, 120.83) * mm});
            skLineSegment(sketch, "E9.0.28.11", {"start": v(-430, 121.83) * mm, "end": v(-430, 120.83) * mm});
            skLineSegment(sketch, "E9.0.29.0", {"start": v(150, 124.83) * mm, "end": v(430, 124.83) * mm});
            skLineSegment(sketch, "E9.0.29.1", {"start": v(-140, 124.83) * mm, "end": v(140, 124.83) * mm});
            skLineSegment(sketch, "E9.0.29.2", {"start": v(-430, 123.83) * mm, "end": v(-150, 123.83) * mm});
            skLineSegment(sketch, "E9.0.29.3", {"start": v(150, 123.83) * mm, "end": v(430, 123.83) * mm});
            skLineSegment(sketch, "E9.0.29.4", {"start": v(-140, 123.83) * mm, "end": v(140, 123.83) * mm});
            skLineSegment(sketch, "E9.0.29.5", {"start": v(-430, 124.83) * mm, "end": v(-150, 124.83) * mm});
            skLineSegment(sketch, "E9.0.29.6", {"start": v(430, 123.83) * mm, "end": v(430, 124.83) * mm});
            skLineSegment(sketch, "E9.0.29.7", {"start": v(150, 123.83) * mm, "end": v(150, 124.83) * mm});
            skLineSegment(sketch, "E9.0.29.8", {"start": v(140, 123.83) * mm, "end": v(140, 124.83) * mm});
            skLineSegment(sketch, "E9.0.29.9", {"start": v(-140, 123.83) * mm, "end": v(-140, 124.83) * mm});
            skLineSegment(sketch, "E9.0.29.10", {"start": v(-150, 124.83) * mm, "end": v(-150, 123.83) * mm});
            skLineSegment(sketch, "E9.0.29.11", {"start": v(-430, 124.83) * mm, "end": v(-430, 123.83) * mm});
            skLineSegment(sketch, "E9.0.30.0", {"start": v(150, 127.83) * mm, "end": v(430, 127.83) * mm});
            skLineSegment(sketch, "E9.0.30.1", {"start": v(-140, 127.83) * mm, "end": v(140, 127.83) * mm});
            skLineSegment(sketch, "E9.0.30.2", {"start": v(-430, 126.83) * mm, "end": v(-150, 126.83) * mm});
            skLineSegment(sketch, "E9.0.30.3", {"start": v(150, 126.83) * mm, "end": v(430, 126.83) * mm});
            skLineSegment(sketch, "E9.0.30.4", {"start": v(-140, 126.83) * mm, "end": v(140, 126.83) * mm});
            skLineSegment(sketch, "E9.0.30.5", {"start": v(-430, 127.83) * mm, "end": v(-150, 127.83) * mm});
            skLineSegment(sketch, "E9.0.30.6", {"start": v(430, 126.83) * mm, "end": v(430, 127.83) * mm});
            skLineSegment(sketch, "E9.0.30.7", {"start": v(150, 126.83) * mm, "end": v(150, 127.83) * mm});
            skLineSegment(sketch, "E9.0.30.8", {"start": v(140, 126.83) * mm, "end": v(140, 127.83) * mm});
            skLineSegment(sketch, "E9.0.30.9", {"start": v(-140, 126.83) * mm, "end": v(-140, 127.83) * mm});
            skLineSegment(sketch, "E9.0.30.10", {"start": v(-150, 127.83) * mm, "end": v(-150, 126.83) * mm});
            skLineSegment(sketch, "E9.0.30.11", {"start": v(-430, 127.83) * mm, "end": v(-430, 126.83) * mm});
            skLineSegment(sketch, "E9.0.31.0", {"start": v(150, 130.83) * mm, "end": v(430, 130.83) * mm});
            skLineSegment(sketch, "E9.0.31.1", {"start": v(-140, 130.83) * mm, "end": v(140, 130.83) * mm});
            skLineSegment(sketch, "E9.0.31.2", {"start": v(-430, 129.83) * mm, "end": v(-150, 129.83) * mm});
            skLineSegment(sketch, "E9.0.31.3", {"start": v(150, 129.83) * mm, "end": v(430, 129.83) * mm});
            skLineSegment(sketch, "E9.0.31.4", {"start": v(-140, 129.83) * mm, "end": v(140, 129.83) * mm});
            skLineSegment(sketch, "E9.0.31.5", {"start": v(-430, 130.83) * mm, "end": v(-150, 130.83) * mm});
            skLineSegment(sketch, "E9.0.31.6", {"start": v(430, 129.83) * mm, "end": v(430, 130.83) * mm});
            skLineSegment(sketch, "E9.0.31.7", {"start": v(150, 129.83) * mm, "end": v(150, 130.83) * mm});
            skLineSegment(sketch, "E9.0.31.8", {"start": v(140, 129.83) * mm, "end": v(140, 130.83) * mm});
            skLineSegment(sketch, "E9.0.31.9", {"start": v(-140, 129.83) * mm, "end": v(-140, 130.83) * mm});
            skLineSegment(sketch, "E9.0.31.10", {"start": v(-150, 130.83) * mm, "end": v(-150, 129.83) * mm});
            skLineSegment(sketch, "E9.0.31.11", {"start": v(-430, 130.83) * mm, "end": v(-430, 129.83) * mm});
            skLineSegment(sketch, "E9.0.32.0", {"start": v(150, 133.83) * mm, "end": v(430, 133.83) * mm});
            skLineSegment(sketch, "E9.0.32.1", {"start": v(-140, 133.83) * mm, "end": v(140, 133.83) * mm});
            skLineSegment(sketch, "E9.0.32.2", {"start": v(-430, 132.83) * mm, "end": v(-150, 132.83) * mm});
            skLineSegment(sketch, "E9.0.32.3", {"start": v(150, 132.83) * mm, "end": v(430, 132.83) * mm});
            skLineSegment(sketch, "E9.0.32.4", {"start": v(-140, 132.83) * mm, "end": v(140, 132.83) * mm});
            skLineSegment(sketch, "E9.0.32.5", {"start": v(-430, 133.83) * mm, "end": v(-150, 133.83) * mm});
            skLineSegment(sketch, "E9.0.32.6", {"start": v(430, 132.83) * mm, "end": v(430, 133.83) * mm});
            skLineSegment(sketch, "E9.0.32.7", {"start": v(150, 132.83) * mm, "end": v(150, 133.83) * mm});
            skLineSegment(sketch, "E9.0.32.8", {"start": v(140, 132.83) * mm, "end": v(140, 133.83) * mm});
            skLineSegment(sketch, "E9.0.32.9", {"start": v(-140, 132.83) * mm, "end": v(-140, 133.83) * mm});
            skLineSegment(sketch, "E9.0.32.10", {"start": v(-150, 133.83) * mm, "end": v(-150, 132.83) * mm});
            skLineSegment(sketch, "E9.0.32.11", {"start": v(-430, 133.83) * mm, "end": v(-430, 132.83) * mm});
            skLineSegment(sketch, "E9.0.33.0", {"start": v(150, 136.83) * mm, "end": v(430, 136.83) * mm});
            skLineSegment(sketch, "E9.0.33.1", {"start": v(-140, 136.83) * mm, "end": v(140, 136.83) * mm});
            skLineSegment(sketch, "E9.0.33.2", {"start": v(-430, 135.83) * mm, "end": v(-150, 135.83) * mm});
            skLineSegment(sketch, "E9.0.33.3", {"start": v(150, 135.83) * mm, "end": v(430, 135.83) * mm});
            skLineSegment(sketch, "E9.0.33.4", {"start": v(-140, 135.83) * mm, "end": v(140, 135.83) * mm});
            skLineSegment(sketch, "E9.0.33.5", {"start": v(-430, 136.83) * mm, "end": v(-150, 136.83) * mm});
            skLineSegment(sketch, "E9.0.33.6", {"start": v(430, 135.83) * mm, "end": v(430, 136.83) * mm});
            skLineSegment(sketch, "E9.0.33.7", {"start": v(150, 135.83) * mm, "end": v(150, 136.83) * mm});
            skLineSegment(sketch, "E9.0.33.8", {"start": v(140, 135.83) * mm, "end": v(140, 136.83) * mm});
            skLineSegment(sketch, "E9.0.33.9", {"start": v(-140, 135.83) * mm, "end": v(-140, 136.83) * mm});
            skLineSegment(sketch, "E9.0.33.10", {"start": v(-150, 136.83) * mm, "end": v(-150, 135.83) * mm});
            skLineSegment(sketch, "E9.0.33.11", {"start": v(-430, 136.83) * mm, "end": v(-430, 135.83) * mm});
            skLineSegment(sketch, "E9.0.34.0", {"start": v(150, 139.83) * mm, "end": v(430, 139.83) * mm});
            skLineSegment(sketch, "E9.0.34.1", {"start": v(-140, 139.83) * mm, "end": v(140, 139.83) * mm});
            skLineSegment(sketch, "E9.0.34.2", {"start": v(-430, 138.83) * mm, "end": v(-150, 138.83) * mm});
            skLineSegment(sketch, "E9.0.34.3", {"start": v(150, 138.83) * mm, "end": v(430, 138.83) * mm});
            skLineSegment(sketch, "E9.0.34.4", {"start": v(-140, 138.83) * mm, "end": v(140, 138.83) * mm});
            skLineSegment(sketch, "E9.0.34.5", {"start": v(-430, 139.83) * mm, "end": v(-150, 139.83) * mm});
            skLineSegment(sketch, "E9.0.34.6", {"start": v(430, 138.83) * mm, "end": v(430, 139.83) * mm});
            skLineSegment(sketch, "E9.0.34.7", {"start": v(150, 138.83) * mm, "end": v(150, 139.83) * mm});
            skLineSegment(sketch, "E9.0.34.8", {"start": v(140, 138.83) * mm, "end": v(140, 139.83) * mm});
            skLineSegment(sketch, "E9.0.34.9", {"start": v(-140, 138.83) * mm, "end": v(-140, 139.83) * mm});
            skLineSegment(sketch, "E9.0.34.10", {"start": v(-150, 139.83) * mm, "end": v(-150, 138.83) * mm});
            skLineSegment(sketch, "E9.0.34.11", {"start": v(-430, 139.83) * mm, "end": v(-430, 138.83) * mm});
            skLineSegment(sketch, "E9.0.35.0", {"start": v(150, 142.83) * mm, "end": v(430, 142.83) * mm});
            skLineSegment(sketch, "E9.0.35.1", {"start": v(-140, 142.83) * mm, "end": v(140, 142.83) * mm});
            skLineSegment(sketch, "E9.0.35.2", {"start": v(-430, 141.83) * mm, "end": v(-150, 141.83) * mm});
            skLineSegment(sketch, "E9.0.35.3", {"start": v(150, 141.83) * mm, "end": v(430, 141.83) * mm});
            skLineSegment(sketch, "E9.0.35.4", {"start": v(-140, 141.83) * mm, "end": v(140, 141.83) * mm});
            skLineSegment(sketch, "E9.0.35.5", {"start": v(-430, 142.83) * mm, "end": v(-150, 142.83) * mm});
            skLineSegment(sketch, "E9.0.35.6", {"start": v(430, 141.83) * mm, "end": v(430, 142.83) * mm});
            skLineSegment(sketch, "E9.0.35.7", {"start": v(150, 141.83) * mm, "end": v(150, 142.83) * mm});
            skLineSegment(sketch, "E9.0.35.8", {"start": v(140, 141.83) * mm, "end": v(140, 142.83) * mm});
            skLineSegment(sketch, "E9.0.35.9", {"start": v(-140, 141.83) * mm, "end": v(-140, 142.83) * mm});
            skLineSegment(sketch, "E9.0.35.10", {"start": v(-150, 142.83) * mm, "end": v(-150, 141.83) * mm});
            skLineSegment(sketch, "E9.0.35.11", {"start": v(-430, 142.83) * mm, "end": v(-430, 141.83) * mm});
            skLineSegment(sketch, "E9.0.36.0", {"start": v(150, 145.83) * mm, "end": v(430, 145.83) * mm});
            skLineSegment(sketch, "E9.0.36.1", {"start": v(-140, 145.83) * mm, "end": v(140, 145.83) * mm});
            skLineSegment(sketch, "E9.0.36.2", {"start": v(-430, 144.83) * mm, "end": v(-150, 144.83) * mm});
            skLineSegment(sketch, "E9.0.36.3", {"start": v(150, 144.83) * mm, "end": v(430, 144.83) * mm});
            skLineSegment(sketch, "E9.0.36.4", {"start": v(-140, 144.83) * mm, "end": v(140, 144.83) * mm});
            skLineSegment(sketch, "E9.0.36.5", {"start": v(-430, 145.83) * mm, "end": v(-150, 145.83) * mm});
            skLineSegment(sketch, "E9.0.36.6", {"start": v(430, 144.83) * mm, "end": v(430, 145.83) * mm});
            skLineSegment(sketch, "E9.0.36.7", {"start": v(150, 144.83) * mm, "end": v(150, 145.83) * mm});
            skLineSegment(sketch, "E9.0.36.8", {"start": v(140, 144.83) * mm, "end": v(140, 145.83) * mm});
            skLineSegment(sketch, "E9.0.36.9", {"start": v(-140, 144.83) * mm, "end": v(-140, 145.83) * mm});
            skLineSegment(sketch, "E9.0.36.10", {"start": v(-150, 145.83) * mm, "end": v(-150, 144.83) * mm});
            skLineSegment(sketch, "E9.0.36.11", {"start": v(-430, 145.83) * mm, "end": v(-430, 144.83) * mm});
            skLineSegment(sketch, "E9.0.37.0", {"start": v(150, 148.83) * mm, "end": v(430, 148.83) * mm});
            skLineSegment(sketch, "E9.0.37.1", {"start": v(-140, 148.83) * mm, "end": v(140, 148.83) * mm});
            skLineSegment(sketch, "E9.0.37.2", {"start": v(-430, 147.83) * mm, "end": v(-150, 147.83) * mm});
            skLineSegment(sketch, "E9.0.37.3", {"start": v(150, 147.83) * mm, "end": v(430, 147.83) * mm});
            skLineSegment(sketch, "E9.0.37.4", {"start": v(-140, 147.83) * mm, "end": v(140, 147.83) * mm});
            skLineSegment(sketch, "E9.0.37.5", {"start": v(-430, 148.83) * mm, "end": v(-150, 148.83) * mm});
            skLineSegment(sketch, "E9.0.37.6", {"start": v(430, 147.83) * mm, "end": v(430, 148.83) * mm});
            skLineSegment(sketch, "E9.0.37.7", {"start": v(150, 147.83) * mm, "end": v(150, 148.83) * mm});
            skLineSegment(sketch, "E9.0.37.8", {"start": v(140, 147.83) * mm, "end": v(140, 148.83) * mm});
            skLineSegment(sketch, "E9.0.37.9", {"start": v(-140, 147.83) * mm, "end": v(-140, 148.83) * mm});
            skLineSegment(sketch, "E9.0.37.10", {"start": v(-150, 148.83) * mm, "end": v(-150, 147.83) * mm});
            skLineSegment(sketch, "E9.0.37.11", {"start": v(-430, 148.83) * mm, "end": v(-430, 147.83) * mm});
            skLineSegment(sketch, "E9.0.38.0", {"start": v(150, 151.83) * mm, "end": v(430, 151.83) * mm});
            skLineSegment(sketch, "E9.0.38.1", {"start": v(-140, 151.83) * mm, "end": v(140, 151.83) * mm});
            skLineSegment(sketch, "E9.0.38.2", {"start": v(-430, 150.83) * mm, "end": v(-150, 150.83) * mm});
            skLineSegment(sketch, "E9.0.38.3", {"start": v(150, 150.83) * mm, "end": v(430, 150.83) * mm});
            skLineSegment(sketch, "E9.0.38.4", {"start": v(-140, 150.83) * mm, "end": v(140, 150.83) * mm});
            skLineSegment(sketch, "E9.0.38.5", {"start": v(-430, 151.83) * mm, "end": v(-150, 151.83) * mm});
            skLineSegment(sketch, "E9.0.38.6", {"start": v(430, 150.83) * mm, "end": v(430, 151.83) * mm});
            skLineSegment(sketch, "E9.0.38.7", {"start": v(150, 150.83) * mm, "end": v(150, 151.83) * mm});
            skLineSegment(sketch, "E9.0.38.8", {"start": v(140, 150.83) * mm, "end": v(140, 151.83) * mm});
            skLineSegment(sketch, "E9.0.38.9", {"start": v(-140, 150.83) * mm, "end": v(-140, 151.83) * mm});
            skLineSegment(sketch, "E9.0.38.10", {"start": v(-150, 151.83) * mm, "end": v(-150, 150.83) * mm});
            skLineSegment(sketch, "E9.0.38.11", {"start": v(-430, 151.83) * mm, "end": v(-430, 150.83) * mm});
            skLineSegment(sketch, "E9.0.39.0", {"start": v(150, 154.83) * mm, "end": v(430, 154.83) * mm});
            skLineSegment(sketch, "E9.0.39.1", {"start": v(-140, 154.83) * mm, "end": v(140, 154.83) * mm});
            skLineSegment(sketch, "E9.0.39.2", {"start": v(-430, 153.83) * mm, "end": v(-150, 153.83) * mm});
            skLineSegment(sketch, "E9.0.39.3", {"start": v(150, 153.83) * mm, "end": v(430, 153.83) * mm});
            skLineSegment(sketch, "E9.0.39.4", {"start": v(-140, 153.83) * mm, "end": v(140, 153.83) * mm});
            skLineSegment(sketch, "E9.0.39.5", {"start": v(-430, 154.83) * mm, "end": v(-150, 154.83) * mm});
            skLineSegment(sketch, "E9.0.39.6", {"start": v(430, 153.83) * mm, "end": v(430, 154.83) * mm});
            skLineSegment(sketch, "E9.0.39.7", {"start": v(150, 153.83) * mm, "end": v(150, 154.83) * mm});
            skLineSegment(sketch, "E9.0.39.8", {"start": v(140, 153.83) * mm, "end": v(140, 154.83) * mm});
            skLineSegment(sketch, "E9.0.39.9", {"start": v(-140, 153.83) * mm, "end": v(-140, 154.83) * mm});
            skLineSegment(sketch, "E9.0.39.10", {"start": v(-150, 154.83) * mm, "end": v(-150, 153.83) * mm});
            skLineSegment(sketch, "E9.0.39.11", {"start": v(-430, 154.83) * mm, "end": v(-430, 153.83) * mm});
            skLineSegment(sketch, "E9.0.40.0", {"start": v(150, 157.83) * mm, "end": v(430, 157.83) * mm});
            skLineSegment(sketch, "E9.0.40.1", {"start": v(-140, 157.83) * mm, "end": v(140, 157.83) * mm});
            skLineSegment(sketch, "E9.0.40.2", {"start": v(-430, 156.83) * mm, "end": v(-150, 156.83) * mm});
            skLineSegment(sketch, "E9.0.40.3", {"start": v(150, 156.83) * mm, "end": v(430, 156.83) * mm});
            skLineSegment(sketch, "E9.0.40.4", {"start": v(-140, 156.83) * mm, "end": v(140, 156.83) * mm});
            skLineSegment(sketch, "E9.0.40.5", {"start": v(-430, 157.83) * mm, "end": v(-150, 157.83) * mm});
            skLineSegment(sketch, "E9.0.40.6", {"start": v(430, 156.83) * mm, "end": v(430, 157.83) * mm});
            skLineSegment(sketch, "E9.0.40.7", {"start": v(150, 156.83) * mm, "end": v(150, 157.83) * mm});
            skLineSegment(sketch, "E9.0.40.8", {"start": v(140, 156.83) * mm, "end": v(140, 157.83) * mm});
            skLineSegment(sketch, "E9.0.40.9", {"start": v(-140, 156.83) * mm, "end": v(-140, 157.83) * mm});
            skLineSegment(sketch, "E9.0.40.10", {"start": v(-150, 157.83) * mm, "end": v(-150, 156.83) * mm});
            skLineSegment(sketch, "E9.0.40.11", {"start": v(-430, 157.83) * mm, "end": v(-430, 156.83) * mm});
            skLineSegment(sketch, "E9.0.41.0", {"start": v(150, 160.83) * mm, "end": v(430, 160.83) * mm});
            skLineSegment(sketch, "E9.0.41.1", {"start": v(-140, 160.83) * mm, "end": v(140, 160.83) * mm});
            skLineSegment(sketch, "E9.0.41.2", {"start": v(-430, 159.83) * mm, "end": v(-150, 159.83) * mm});
            skLineSegment(sketch, "E9.0.41.3", {"start": v(150, 159.83) * mm, "end": v(430, 159.83) * mm});
            skLineSegment(sketch, "E9.0.41.4", {"start": v(-140, 159.83) * mm, "end": v(140, 159.83) * mm});
            skLineSegment(sketch, "E9.0.41.5", {"start": v(-430, 160.83) * mm, "end": v(-150, 160.83) * mm});
            skLineSegment(sketch, "E9.0.41.6", {"start": v(430, 159.83) * mm, "end": v(430, 160.83) * mm});
            skLineSegment(sketch, "E9.0.41.7", {"start": v(150, 159.83) * mm, "end": v(150, 160.83) * mm});
            skLineSegment(sketch, "E9.0.41.8", {"start": v(140, 159.83) * mm, "end": v(140, 160.83) * mm});
            skLineSegment(sketch, "E9.0.41.9", {"start": v(-140, 159.83) * mm, "end": v(-140, 160.83) * mm});
            skLineSegment(sketch, "E9.0.41.10", {"start": v(-150, 160.83) * mm, "end": v(-150, 159.83) * mm});
            skLineSegment(sketch, "E9.0.41.11", {"start": v(-430, 160.83) * mm, "end": v(-430, 159.83) * mm});
            skLineSegment(sketch, "E9.0.42.0", {"start": v(150, 163.83) * mm, "end": v(430, 163.83) * mm});
            skLineSegment(sketch, "E9.0.42.1", {"start": v(-140, 163.83) * mm, "end": v(140, 163.83) * mm});
            skLineSegment(sketch, "E9.0.42.2", {"start": v(-430, 162.83) * mm, "end": v(-150, 162.83) * mm});
            skLineSegment(sketch, "E9.0.42.3", {"start": v(150, 162.83) * mm, "end": v(430, 162.83) * mm});
            skLineSegment(sketch, "E9.0.42.4", {"start": v(-140, 162.83) * mm, "end": v(140, 162.83) * mm});
            skLineSegment(sketch, "E9.0.42.5", {"start": v(-430, 163.83) * mm, "end": v(-150, 163.83) * mm});
            skLineSegment(sketch, "E9.0.42.6", {"start": v(430, 162.83) * mm, "end": v(430, 163.83) * mm});
            skLineSegment(sketch, "E9.0.42.7", {"start": v(150, 162.83) * mm, "end": v(150, 163.83) * mm});
            skLineSegment(sketch, "E9.0.42.8", {"start": v(140, 162.83) * mm, "end": v(140, 163.83) * mm});
            skLineSegment(sketch, "E9.0.42.9", {"start": v(-140, 162.83) * mm, "end": v(-140, 163.83) * mm});
            skLineSegment(sketch, "E9.0.42.10", {"start": v(-150, 163.83) * mm, "end": v(-150, 162.83) * mm});
            skLineSegment(sketch, "E9.0.42.11", {"start": v(-430, 163.83) * mm, "end": v(-430, 162.83) * mm});
            skLineSegment(sketch, "E9.0.43.0", {"start": v(150, 166.83) * mm, "end": v(430, 166.83) * mm});
            skLineSegment(sketch, "E9.0.43.1", {"start": v(-140, 166.83) * mm, "end": v(140, 166.83) * mm});
            skLineSegment(sketch, "E9.0.43.2", {"start": v(-430, 165.83) * mm, "end": v(-150, 165.83) * mm});
            skLineSegment(sketch, "E9.0.43.3", {"start": v(150, 165.83) * mm, "end": v(430, 165.83) * mm});
            skLineSegment(sketch, "E9.0.43.4", {"start": v(-140, 165.83) * mm, "end": v(140, 165.83) * mm});
            skLineSegment(sketch, "E9.0.43.5", {"start": v(-430, 166.83) * mm, "end": v(-150, 166.83) * mm});
            skLineSegment(sketch, "E9.0.43.6", {"start": v(430, 165.83) * mm, "end": v(430, 166.83) * mm});
            skLineSegment(sketch, "E9.0.43.7", {"start": v(150, 165.83) * mm, "end": v(150, 166.83) * mm});
            skLineSegment(sketch, "E9.0.43.8", {"start": v(140, 165.83) * mm, "end": v(140, 166.83) * mm});
            skLineSegment(sketch, "E9.0.43.9", {"start": v(-140, 165.83) * mm, "end": v(-140, 166.83) * mm});
            skLineSegment(sketch, "E9.0.43.10", {"start": v(-150, 166.83) * mm, "end": v(-150, 165.83) * mm});
            skLineSegment(sketch, "E9.0.43.11", {"start": v(-430, 166.83) * mm, "end": v(-430, 165.83) * mm});
            skLineSegment(sketch, "E9.0.44.0", {"start": v(150, 169.83) * mm, "end": v(430, 169.83) * mm});
            skLineSegment(sketch, "E9.0.44.1", {"start": v(-140, 169.83) * mm, "end": v(140, 169.83) * mm});
            skLineSegment(sketch, "E9.0.44.2", {"start": v(-430, 168.83) * mm, "end": v(-150, 168.83) * mm});
            skLineSegment(sketch, "E9.0.44.3", {"start": v(150, 168.83) * mm, "end": v(430, 168.83) * mm});
            skLineSegment(sketch, "E9.0.44.4", {"start": v(-140, 168.83) * mm, "end": v(140, 168.83) * mm});
            skLineSegment(sketch, "E9.0.44.5", {"start": v(-430, 169.83) * mm, "end": v(-150, 169.83) * mm});
            skLineSegment(sketch, "E9.0.44.6", {"start": v(430, 168.83) * mm, "end": v(430, 169.83) * mm});
            skLineSegment(sketch, "E9.0.44.7", {"start": v(150, 168.83) * mm, "end": v(150, 169.83) * mm});
            skLineSegment(sketch, "E9.0.44.8", {"start": v(140, 168.83) * mm, "end": v(140, 169.83) * mm});
            skLineSegment(sketch, "E9.0.44.9", {"start": v(-140, 168.83) * mm, "end": v(-140, 169.83) * mm});
            skLineSegment(sketch, "E9.0.44.10", {"start": v(-150, 169.83) * mm, "end": v(-150, 168.83) * mm});
            skLineSegment(sketch, "E9.0.44.11", {"start": v(-430, 169.83) * mm, "end": v(-430, 168.83) * mm});
            skLineSegment(sketch, "E9.0.45.0", {"start": v(150, 172.83) * mm, "end": v(430, 172.83) * mm});
            skLineSegment(sketch, "E9.0.45.1", {"start": v(-140, 172.83) * mm, "end": v(140, 172.83) * mm});
            skLineSegment(sketch, "E9.0.45.2", {"start": v(-430, 171.83) * mm, "end": v(-150, 171.83) * mm});
            skLineSegment(sketch, "E9.0.45.3", {"start": v(150, 171.83) * mm, "end": v(430, 171.83) * mm});
            skLineSegment(sketch, "E9.0.45.4", {"start": v(-140, 171.83) * mm, "end": v(140, 171.83) * mm});
            skLineSegment(sketch, "E9.0.45.5", {"start": v(-430, 172.83) * mm, "end": v(-150, 172.83) * mm});
            skLineSegment(sketch, "E9.0.45.6", {"start": v(430, 171.83) * mm, "end": v(430, 172.83) * mm});
            skLineSegment(sketch, "E9.0.45.7", {"start": v(150, 171.83) * mm, "end": v(150, 172.83) * mm});
            skLineSegment(sketch, "E9.0.45.8", {"start": v(140, 171.83) * mm, "end": v(140, 172.83) * mm});
            skLineSegment(sketch, "E9.0.45.9", {"start": v(-140, 171.83) * mm, "end": v(-140, 172.83) * mm});
            skLineSegment(sketch, "E9.0.45.10", {"start": v(-150, 172.83) * mm, "end": v(-150, 171.83) * mm});
            skLineSegment(sketch, "E9.0.45.11", {"start": v(-430, 172.83) * mm, "end": v(-430, 171.83) * mm});
            skLineSegment(sketch, "E9.0.46.0", {"start": v(150, 175.83) * mm, "end": v(430, 175.83) * mm});
            skLineSegment(sketch, "E9.0.46.1", {"start": v(-140, 175.83) * mm, "end": v(140, 175.83) * mm});
            skLineSegment(sketch, "E9.0.46.2", {"start": v(-430, 174.83) * mm, "end": v(-150, 174.83) * mm});
            skLineSegment(sketch, "E9.0.46.3", {"start": v(150, 174.83) * mm, "end": v(430, 174.83) * mm});
            skLineSegment(sketch, "E9.0.46.4", {"start": v(-140, 174.83) * mm, "end": v(140, 174.83) * mm});
            skLineSegment(sketch, "E9.0.46.5", {"start": v(-430, 175.83) * mm, "end": v(-150, 175.83) * mm});
            skLineSegment(sketch, "E9.0.46.6", {"start": v(430, 174.83) * mm, "end": v(430, 175.83) * mm});
            skLineSegment(sketch, "E9.0.46.7", {"start": v(150, 174.83) * mm, "end": v(150, 175.83) * mm});
            skLineSegment(sketch, "E9.0.46.8", {"start": v(140, 174.83) * mm, "end": v(140, 175.83) * mm});
            skLineSegment(sketch, "E9.0.46.9", {"start": v(-140, 174.83) * mm, "end": v(-140, 175.83) * mm});
            skLineSegment(sketch, "E9.0.46.10", {"start": v(-150, 175.83) * mm, "end": v(-150, 174.83) * mm});
            skLineSegment(sketch, "E9.0.46.11", {"start": v(-430, 175.83) * mm, "end": v(-430, 174.83) * mm});
            skLineSegment(sketch, "E9.0.47.0", {"start": v(150, 178.83) * mm, "end": v(430, 178.83) * mm});
            skLineSegment(sketch, "E9.0.47.1", {"start": v(-140, 178.83) * mm, "end": v(140, 178.83) * mm});
            skLineSegment(sketch, "E9.0.47.2", {"start": v(-430, 177.83) * mm, "end": v(-150, 177.83) * mm});
            skLineSegment(sketch, "E9.0.47.3", {"start": v(150, 177.83) * mm, "end": v(430, 177.83) * mm});
            skLineSegment(sketch, "E9.0.47.4", {"start": v(-140, 177.83) * mm, "end": v(140, 177.83) * mm});
            skLineSegment(sketch, "E9.0.47.5", {"start": v(-430, 178.83) * mm, "end": v(-150, 178.83) * mm});
            skLineSegment(sketch, "E9.0.47.6", {"start": v(430, 177.83) * mm, "end": v(430, 178.83) * mm});
            skLineSegment(sketch, "E9.0.47.7", {"start": v(150, 177.83) * mm, "end": v(150, 178.83) * mm});
            skLineSegment(sketch, "E9.0.47.8", {"start": v(140, 177.83) * mm, "end": v(140, 178.83) * mm});
            skLineSegment(sketch, "E9.0.47.9", {"start": v(-140, 177.83) * mm, "end": v(-140, 178.83) * mm});
            skLineSegment(sketch, "E9.0.47.10", {"start": v(-150, 178.83) * mm, "end": v(-150, 177.83) * mm});
            skLineSegment(sketch, "E9.0.47.11", {"start": v(-430, 178.83) * mm, "end": v(-430, 177.83) * mm});
            skLineSegment(sketch, "E9.0.48.0", {"start": v(150, 181.83) * mm, "end": v(430, 181.83) * mm});
            skLineSegment(sketch, "E9.0.48.1", {"start": v(-140, 181.83) * mm, "end": v(140, 181.83) * mm});
            skLineSegment(sketch, "E9.0.48.2", {"start": v(-430, 180.83) * mm, "end": v(-150, 180.83) * mm});
            skLineSegment(sketch, "E9.0.48.3", {"start": v(150, 180.83) * mm, "end": v(430, 180.83) * mm});
            skLineSegment(sketch, "E9.0.48.4", {"start": v(-140, 180.83) * mm, "end": v(140, 180.83) * mm});
            skLineSegment(sketch, "E9.0.48.5", {"start": v(-430, 181.83) * mm, "end": v(-150, 181.83) * mm});
            skLineSegment(sketch, "E9.0.48.6", {"start": v(430, 180.83) * mm, "end": v(430, 181.83) * mm});
            skLineSegment(sketch, "E9.0.48.7", {"start": v(150, 180.83) * mm, "end": v(150, 181.83) * mm});
            skLineSegment(sketch, "E9.0.48.8", {"start": v(140, 180.83) * mm, "end": v(140, 181.83) * mm});
            skLineSegment(sketch, "E9.0.48.9", {"start": v(-140, 180.83) * mm, "end": v(-140, 181.83) * mm});
            skLineSegment(sketch, "E9.0.48.10", {"start": v(-150, 181.83) * mm, "end": v(-150, 180.83) * mm});
            skLineSegment(sketch, "E9.0.48.11", {"start": v(-430, 181.83) * mm, "end": v(-430, 180.83) * mm});
            skLineSegment(sketch, "E9.0.49.0", {"start": v(150, 184.83) * mm, "end": v(430, 184.83) * mm});
            skLineSegment(sketch, "E9.0.49.1", {"start": v(-140, 184.83) * mm, "end": v(140, 184.83) * mm});
            skLineSegment(sketch, "E9.0.49.2", {"start": v(-430, 183.83) * mm, "end": v(-150, 183.83) * mm});
            skLineSegment(sketch, "E9.0.49.3", {"start": v(150, 183.83) * mm, "end": v(430, 183.83) * mm});
            skLineSegment(sketch, "E9.0.49.4", {"start": v(-140, 183.83) * mm, "end": v(140, 183.83) * mm});
            skLineSegment(sketch, "E9.0.49.5", {"start": v(-430, 184.83) * mm, "end": v(-150, 184.83) * mm});
            skLineSegment(sketch, "E9.0.49.6", {"start": v(430, 183.83) * mm, "end": v(430, 184.83) * mm});
            skLineSegment(sketch, "E9.0.49.7", {"start": v(150, 183.83) * mm, "end": v(150, 184.83) * mm});
            skLineSegment(sketch, "E9.0.49.8", {"start": v(140, 183.83) * mm, "end": v(140, 184.83) * mm});
            skLineSegment(sketch, "E9.0.49.9", {"start": v(-140, 183.83) * mm, "end": v(-140, 184.83) * mm});
            skLineSegment(sketch, "E9.0.49.10", {"start": v(-150, 184.83) * mm, "end": v(-150, 183.83) * mm});
            skLineSegment(sketch, "E9.0.49.11", {"start": v(-430, 184.83) * mm, "end": v(-430, 183.83) * mm});
            skLineSegment(sketch, "E9.0.50.0", {"start": v(150, 187.83) * mm, "end": v(430, 187.83) * mm});
            skLineSegment(sketch, "E9.0.50.1", {"start": v(-140, 187.83) * mm, "end": v(140, 187.83) * mm});
            skLineSegment(sketch, "E9.0.50.2", {"start": v(-430, 186.83) * mm, "end": v(-150, 186.83) * mm});
            skLineSegment(sketch, "E9.0.50.3", {"start": v(150, 186.83) * mm, "end": v(430, 186.83) * mm});
            skLineSegment(sketch, "E9.0.50.4", {"start": v(-140, 186.83) * mm, "end": v(140, 186.83) * mm});
            skLineSegment(sketch, "E9.0.50.5", {"start": v(-430, 187.83) * mm, "end": v(-150, 187.83) * mm});
            skLineSegment(sketch, "E9.0.50.6", {"start": v(430, 186.83) * mm, "end": v(430, 187.83) * mm});
            skLineSegment(sketch, "E9.0.50.7", {"start": v(150, 186.83) * mm, "end": v(150, 187.83) * mm});
            skLineSegment(sketch, "E9.0.50.8", {"start": v(140, 186.83) * mm, "end": v(140, 187.83) * mm});
            skLineSegment(sketch, "E9.0.50.9", {"start": v(-140, 186.83) * mm, "end": v(-140, 187.83) * mm});
            skLineSegment(sketch, "E9.0.50.10", {"start": v(-150, 187.83) * mm, "end": v(-150, 186.83) * mm});
            skLineSegment(sketch, "E9.0.50.11", {"start": v(-430, 187.83) * mm, "end": v(-430, 186.83) * mm});
            skLineSegment(sketch, "E9.0.51.0", {"start": v(150, 190.83) * mm, "end": v(430, 190.83) * mm});
            skLineSegment(sketch, "E9.0.51.1", {"start": v(-140, 190.83) * mm, "end": v(140, 190.83) * mm});
            skLineSegment(sketch, "E9.0.51.2", {"start": v(-430, 189.83) * mm, "end": v(-150, 189.83) * mm});
            skLineSegment(sketch, "E9.0.51.3", {"start": v(150, 189.83) * mm, "end": v(430, 189.83) * mm});
            skLineSegment(sketch, "E9.0.51.4", {"start": v(-140, 189.83) * mm, "end": v(140, 189.83) * mm});
            skLineSegment(sketch, "E9.0.51.5", {"start": v(-430, 190.83) * mm, "end": v(-150, 190.83) * mm});
            skLineSegment(sketch, "E9.0.51.6", {"start": v(430, 189.83) * mm, "end": v(430, 190.83) * mm});
            skLineSegment(sketch, "E9.0.51.7", {"start": v(150, 189.83) * mm, "end": v(150, 190.83) * mm});
            skLineSegment(sketch, "E9.0.51.8", {"start": v(140, 189.83) * mm, "end": v(140, 190.83) * mm});
            skLineSegment(sketch, "E9.0.51.9", {"start": v(-140, 189.83) * mm, "end": v(-140, 190.83) * mm});
            skLineSegment(sketch, "E9.0.51.10", {"start": v(-150, 190.83) * mm, "end": v(-150, 189.83) * mm});
            skLineSegment(sketch, "E9.0.51.11", {"start": v(-430, 190.83) * mm, "end": v(-430, 189.83) * mm});
            skLineSegment(sketch, "E9.0.52.0", {"start": v(150, 193.83) * mm, "end": v(430, 193.83) * mm});
            skLineSegment(sketch, "E9.0.52.1", {"start": v(-140, 193.83) * mm, "end": v(140, 193.83) * mm});
            skLineSegment(sketch, "E9.0.52.2", {"start": v(-430, 192.83) * mm, "end": v(-150, 192.83) * mm});
            skLineSegment(sketch, "E9.0.52.3", {"start": v(150, 192.83) * mm, "end": v(430, 192.83) * mm});
            skLineSegment(sketch, "E9.0.52.4", {"start": v(-140, 192.83) * mm, "end": v(140, 192.83) * mm});
            skLineSegment(sketch, "E9.0.52.5", {"start": v(-430, 193.83) * mm, "end": v(-150, 193.83) * mm});
            skLineSegment(sketch, "E9.0.52.6", {"start": v(430, 192.83) * mm, "end": v(430, 193.83) * mm});
            skLineSegment(sketch, "E9.0.52.7", {"start": v(150, 192.83) * mm, "end": v(150, 193.83) * mm});
            skLineSegment(sketch, "E9.0.52.8", {"start": v(140, 192.83) * mm, "end": v(140, 193.83) * mm});
            skLineSegment(sketch, "E9.0.52.9", {"start": v(-140, 192.83) * mm, "end": v(-140, 193.83) * mm});
            skLineSegment(sketch, "E9.0.52.10", {"start": v(-150, 193.83) * mm, "end": v(-150, 192.83) * mm});
            skLineSegment(sketch, "E9.0.52.11", {"start": v(-430, 193.83) * mm, "end": v(-430, 192.83) * mm});
            skLineSegment(sketch, "E9.0.53.0", {"start": v(150, 196.83) * mm, "end": v(430, 196.83) * mm});
            skLineSegment(sketch, "E9.0.53.1", {"start": v(-140, 196.83) * mm, "end": v(140, 196.83) * mm});
            skLineSegment(sketch, "E9.0.53.2", {"start": v(-430, 195.83) * mm, "end": v(-150, 195.83) * mm});
            skLineSegment(sketch, "E9.0.53.3", {"start": v(150, 195.83) * mm, "end": v(430, 195.83) * mm});
            skLineSegment(sketch, "E9.0.53.4", {"start": v(-140, 195.83) * mm, "end": v(140, 195.83) * mm});
            skLineSegment(sketch, "E9.0.53.5", {"start": v(-430, 196.83) * mm, "end": v(-150, 196.83) * mm});
            skLineSegment(sketch, "E9.0.53.6", {"start": v(430, 195.83) * mm, "end": v(430, 196.83) * mm});
            skLineSegment(sketch, "E9.0.53.7", {"start": v(150, 195.83) * mm, "end": v(150, 196.83) * mm});
            skLineSegment(sketch, "E9.0.53.8", {"start": v(140, 195.83) * mm, "end": v(140, 196.83) * mm});
            skLineSegment(sketch, "E9.0.53.9", {"start": v(-140, 195.83) * mm, "end": v(-140, 196.83) * mm});
            skLineSegment(sketch, "E9.0.53.10", {"start": v(-150, 196.83) * mm, "end": v(-150, 195.83) * mm});
            skLineSegment(sketch, "E9.0.53.11", {"start": v(-430, 196.83) * mm, "end": v(-430, 195.83) * mm});
            skLineSegment(sketch, "E9.0.54.0", {"start": v(150, 199.83) * mm, "end": v(430, 199.83) * mm});
            skLineSegment(sketch, "E9.0.54.1", {"start": v(-140, 199.83) * mm, "end": v(140, 199.83) * mm});
            skLineSegment(sketch, "E9.0.54.2", {"start": v(-430, 198.83) * mm, "end": v(-150, 198.83) * mm});
            skLineSegment(sketch, "E9.0.54.3", {"start": v(150, 198.83) * mm, "end": v(430, 198.83) * mm});
            skLineSegment(sketch, "E9.0.54.4", {"start": v(-140, 198.83) * mm, "end": v(140, 198.83) * mm});
            skLineSegment(sketch, "E9.0.54.5", {"start": v(-430, 199.83) * mm, "end": v(-150, 199.83) * mm});
            skLineSegment(sketch, "E9.0.54.6", {"start": v(430, 198.83) * mm, "end": v(430, 199.83) * mm});
            skLineSegment(sketch, "E9.0.54.7", {"start": v(150, 198.83) * mm, "end": v(150, 199.83) * mm});
            skLineSegment(sketch, "E9.0.54.8", {"start": v(140, 198.83) * mm, "end": v(140, 199.83) * mm});
            skLineSegment(sketch, "E9.0.54.9", {"start": v(-140, 198.83) * mm, "end": v(-140, 199.83) * mm});
            skLineSegment(sketch, "E9.0.54.10", {"start": v(-150, 199.83) * mm, "end": v(-150, 198.83) * mm});
            skLineSegment(sketch, "E9.0.54.11", {"start": v(-430, 199.83) * mm, "end": v(-430, 198.83) * mm});
            skLineSegment(sketch, "E9.0.55.0", {"start": v(150, 202.83) * mm, "end": v(430, 202.83) * mm});
            skLineSegment(sketch, "E9.0.55.1", {"start": v(-140, 202.83) * mm, "end": v(140, 202.83) * mm});
            skLineSegment(sketch, "E9.0.55.2", {"start": v(-430, 201.83) * mm, "end": v(-150, 201.83) * mm});
            skLineSegment(sketch, "E9.0.55.3", {"start": v(150, 201.83) * mm, "end": v(430, 201.83) * mm});
            skLineSegment(sketch, "E9.0.55.4", {"start": v(-140, 201.83) * mm, "end": v(140, 201.83) * mm});
            skLineSegment(sketch, "E9.0.55.5", {"start": v(-430, 202.83) * mm, "end": v(-150, 202.83) * mm});
            skLineSegment(sketch, "E9.0.55.6", {"start": v(430, 201.83) * mm, "end": v(430, 202.83) * mm});
            skLineSegment(sketch, "E9.0.55.7", {"start": v(150, 201.83) * mm, "end": v(150, 202.83) * mm});
            skLineSegment(sketch, "E9.0.55.8", {"start": v(140, 201.83) * mm, "end": v(140, 202.83) * mm});
            skLineSegment(sketch, "E9.0.55.9", {"start": v(-140, 201.83) * mm, "end": v(-140, 202.83) * mm});
            skLineSegment(sketch, "E9.0.55.10", {"start": v(-150, 202.83) * mm, "end": v(-150, 201.83) * mm});
            skLineSegment(sketch, "E9.0.55.11", {"start": v(-430, 202.83) * mm, "end": v(-430, 201.83) * mm});
            skLineSegment(sketch, "E9.0.56.0", {"start": v(150, 205.83) * mm, "end": v(430, 205.83) * mm});
            skLineSegment(sketch, "E9.0.56.1", {"start": v(-140, 205.83) * mm, "end": v(140, 205.83) * mm});
            skLineSegment(sketch, "E9.0.56.2", {"start": v(-430, 204.83) * mm, "end": v(-150, 204.83) * mm});
            skLineSegment(sketch, "E9.0.56.3", {"start": v(150, 204.83) * mm, "end": v(430, 204.83) * mm});
            skLineSegment(sketch, "E9.0.56.4", {"start": v(-140, 204.83) * mm, "end": v(140, 204.83) * mm});
            skLineSegment(sketch, "E9.0.56.5", {"start": v(-430, 205.83) * mm, "end": v(-150, 205.83) * mm});
            skLineSegment(sketch, "E9.0.56.6", {"start": v(430, 204.83) * mm, "end": v(430, 205.83) * mm});
            skLineSegment(sketch, "E9.0.56.7", {"start": v(150, 204.83) * mm, "end": v(150, 205.83) * mm});
            skLineSegment(sketch, "E9.0.56.8", {"start": v(140, 204.83) * mm, "end": v(140, 205.83) * mm});
            skLineSegment(sketch, "E9.0.56.9", {"start": v(-140, 204.83) * mm, "end": v(-140, 205.83) * mm});
            skLineSegment(sketch, "E9.0.56.10", {"start": v(-150, 205.83) * mm, "end": v(-150, 204.83) * mm});
            skLineSegment(sketch, "E9.0.56.11", {"start": v(-430, 205.83) * mm, "end": v(-430, 204.83) * mm});
            skLineSegment(sketch, "E9.0.57.0", {"start": v(150, 208.83) * mm, "end": v(430, 208.83) * mm});
            skLineSegment(sketch, "E9.0.57.1", {"start": v(-140, 208.83) * mm, "end": v(140, 208.83) * mm});
            skLineSegment(sketch, "E9.0.57.2", {"start": v(-430, 207.83) * mm, "end": v(-150, 207.83) * mm});
            skLineSegment(sketch, "E9.0.57.3", {"start": v(150, 207.83) * mm, "end": v(430, 207.83) * mm});
            skLineSegment(sketch, "E9.0.57.4", {"start": v(-140, 207.83) * mm, "end": v(140, 207.83) * mm});
            skLineSegment(sketch, "E9.0.57.5", {"start": v(-430, 208.83) * mm, "end": v(-150, 208.83) * mm});
            skLineSegment(sketch, "E9.0.57.6", {"start": v(430, 207.83) * mm, "end": v(430, 208.83) * mm});
            skLineSegment(sketch, "E9.0.57.7", {"start": v(150, 207.83) * mm, "end": v(150, 208.83) * mm});
            skLineSegment(sketch, "E9.0.57.8", {"start": v(140, 207.83) * mm, "end": v(140, 208.83) * mm});
            skLineSegment(sketch, "E9.0.57.9", {"start": v(-140, 207.83) * mm, "end": v(-140, 208.83) * mm});
            skLineSegment(sketch, "E9.0.57.10", {"start": v(-150, 208.83) * mm, "end": v(-150, 207.83) * mm});
            skLineSegment(sketch, "E9.0.57.11", {"start": v(-430, 208.83) * mm, "end": v(-430, 207.83) * mm});
            skLineSegment(sketch, "E9.0.58.0", {"start": v(150, 211.83) * mm, "end": v(430, 211.83) * mm});
            skLineSegment(sketch, "E9.0.58.1", {"start": v(-140, 211.83) * mm, "end": v(140, 211.83) * mm});
            skLineSegment(sketch, "E9.0.58.2", {"start": v(-430, 210.83) * mm, "end": v(-150, 210.83) * mm});
            skLineSegment(sketch, "E9.0.58.3", {"start": v(150, 210.83) * mm, "end": v(430, 210.83) * mm});
            skLineSegment(sketch, "E9.0.58.4", {"start": v(-140, 210.83) * mm, "end": v(140, 210.83) * mm});
            skLineSegment(sketch, "E9.0.58.5", {"start": v(-430, 211.83) * mm, "end": v(-150, 211.83) * mm});
            skLineSegment(sketch, "E9.0.58.6", {"start": v(430, 210.83) * mm, "end": v(430, 211.83) * mm});
            skLineSegment(sketch, "E9.0.58.7", {"start": v(150, 210.83) * mm, "end": v(150, 211.83) * mm});
            skLineSegment(sketch, "E9.0.58.8", {"start": v(140, 210.83) * mm, "end": v(140, 211.83) * mm});
            skLineSegment(sketch, "E9.0.58.9", {"start": v(-140, 210.83) * mm, "end": v(-140, 211.83) * mm});
            skLineSegment(sketch, "E9.0.58.10", {"start": v(-150, 211.83) * mm, "end": v(-150, 210.83) * mm});
            skLineSegment(sketch, "E9.0.58.11", {"start": v(-430, 211.83) * mm, "end": v(-430, 210.83) * mm});
            skLineSegment(sketch, "E9.0.59.0", {"start": v(150, 214.83) * mm, "end": v(430, 214.83) * mm});
            skLineSegment(sketch, "E9.0.59.1", {"start": v(-140, 214.83) * mm, "end": v(140, 214.83) * mm});
            skLineSegment(sketch, "E9.0.59.2", {"start": v(-430, 213.83) * mm, "end": v(-150, 213.83) * mm});
            skLineSegment(sketch, "E9.0.59.3", {"start": v(150, 213.83) * mm, "end": v(430, 213.83) * mm});
            skLineSegment(sketch, "E9.0.59.4", {"start": v(-140, 213.83) * mm, "end": v(140, 213.83) * mm});
            skLineSegment(sketch, "E9.0.59.5", {"start": v(-430, 214.83) * mm, "end": v(-150, 214.83) * mm});
            skLineSegment(sketch, "E9.0.59.6", {"start": v(430, 213.83) * mm, "end": v(430, 214.83) * mm});
            skLineSegment(sketch, "E9.0.59.7", {"start": v(150, 213.83) * mm, "end": v(150, 214.83) * mm});
            skLineSegment(sketch, "E9.0.59.8", {"start": v(140, 213.83) * mm, "end": v(140, 214.83) * mm});
            skLineSegment(sketch, "E9.0.59.9", {"start": v(-140, 213.83) * mm, "end": v(-140, 214.83) * mm});
            skLineSegment(sketch, "E9.0.59.10", {"start": v(-150, 214.83) * mm, "end": v(-150, 213.83) * mm});
            skLineSegment(sketch, "E9.0.59.11", {"start": v(-430, 214.83) * mm, "end": v(-430, 213.83) * mm});
            skLineSegment(sketch, "E9.0.60.0", {"start": v(150, 217.83) * mm, "end": v(430, 217.83) * mm});
            skLineSegment(sketch, "E9.0.60.1", {"start": v(-140, 217.83) * mm, "end": v(140, 217.83) * mm});
            skLineSegment(sketch, "E9.0.60.2", {"start": v(-430, 216.83) * mm, "end": v(-150, 216.83) * mm});
            skLineSegment(sketch, "E9.0.60.3", {"start": v(150, 216.83) * mm, "end": v(430, 216.83) * mm});
            skLineSegment(sketch, "E9.0.60.4", {"start": v(-140, 216.83) * mm, "end": v(140, 216.83) * mm});
            skLineSegment(sketch, "E9.0.60.5", {"start": v(-430, 217.83) * mm, "end": v(-150, 217.83) * mm});
            skLineSegment(sketch, "E9.0.60.6", {"start": v(430, 216.83) * mm, "end": v(430, 217.83) * mm});
            skLineSegment(sketch, "E9.0.60.7", {"start": v(150, 216.83) * mm, "end": v(150, 217.83) * mm});
            skLineSegment(sketch, "E9.0.60.8", {"start": v(140, 216.83) * mm, "end": v(140, 217.83) * mm});
            skLineSegment(sketch, "E9.0.60.9", {"start": v(-140, 216.83) * mm, "end": v(-140, 217.83) * mm});
            skLineSegment(sketch, "E9.0.60.10", {"start": v(-150, 217.83) * mm, "end": v(-150, 216.83) * mm});
            skLineSegment(sketch, "E9.0.60.11", {"start": v(-430, 217.83) * mm, "end": v(-430, 216.83) * mm});
            skLineSegment(sketch, "E9.0.61.0", {"start": v(150, 220.83) * mm, "end": v(430, 220.83) * mm});
            skLineSegment(sketch, "E9.0.61.1", {"start": v(-140, 220.83) * mm, "end": v(140, 220.83) * mm});
            skLineSegment(sketch, "E9.0.61.2", {"start": v(-430, 219.83) * mm, "end": v(-150, 219.83) * mm});
            skLineSegment(sketch, "E9.0.61.3", {"start": v(150, 219.83) * mm, "end": v(430, 219.83) * mm});
            skLineSegment(sketch, "E9.0.61.4", {"start": v(-140, 219.83) * mm, "end": v(140, 219.83) * mm});
            skLineSegment(sketch, "E9.0.61.5", {"start": v(-430, 220.83) * mm, "end": v(-150, 220.83) * mm});
            skLineSegment(sketch, "E9.0.61.6", {"start": v(430, 219.83) * mm, "end": v(430, 220.83) * mm});
            skLineSegment(sketch, "E9.0.61.7", {"start": v(150, 219.83) * mm, "end": v(150, 220.83) * mm});
            skLineSegment(sketch, "E9.0.61.8", {"start": v(140, 219.83) * mm, "end": v(140, 220.83) * mm});
            skLineSegment(sketch, "E9.0.61.9", {"start": v(-140, 219.83) * mm, "end": v(-140, 220.83) * mm});
            skLineSegment(sketch, "E9.0.61.10", {"start": v(-150, 220.83) * mm, "end": v(-150, 219.83) * mm});
            skLineSegment(sketch, "E9.0.61.11", {"start": v(-430, 220.83) * mm, "end": v(-430, 219.83) * mm});
            skLineSegment(sketch, "E9.0.62.0", {"start": v(150, 223.83) * mm, "end": v(430, 223.83) * mm});
            skLineSegment(sketch, "E9.0.62.1", {"start": v(-140, 223.83) * mm, "end": v(140, 223.83) * mm});
            skLineSegment(sketch, "E9.0.62.2", {"start": v(-430, 222.83) * mm, "end": v(-150, 222.83) * mm});
            skLineSegment(sketch, "E9.0.62.3", {"start": v(150, 222.83) * mm, "end": v(430, 222.83) * mm});
            skLineSegment(sketch, "E9.0.62.4", {"start": v(-140, 222.83) * mm, "end": v(140, 222.83) * mm});
            skLineSegment(sketch, "E9.0.62.5", {"start": v(-430, 223.83) * mm, "end": v(-150, 223.83) * mm});
            skLineSegment(sketch, "E9.0.62.6", {"start": v(430, 222.83) * mm, "end": v(430, 223.83) * mm});
            skLineSegment(sketch, "E9.0.62.7", {"start": v(150, 222.83) * mm, "end": v(150, 223.83) * mm});
            skLineSegment(sketch, "E9.0.62.8", {"start": v(140, 222.83) * mm, "end": v(140, 223.83) * mm});
            skLineSegment(sketch, "E9.0.62.9", {"start": v(-140, 222.83) * mm, "end": v(-140, 223.83) * mm});
            skLineSegment(sketch, "E9.0.62.10", {"start": v(-150, 223.83) * mm, "end": v(-150, 222.83) * mm});
            skLineSegment(sketch, "E9.0.62.11", {"start": v(-430, 223.83) * mm, "end": v(-430, 222.83) * mm});
            skLineSegment(sketch, "E9.0.63.0", {"start": v(150, 226.83) * mm, "end": v(430, 226.83) * mm});
            skLineSegment(sketch, "E9.0.63.1", {"start": v(-140, 226.83) * mm, "end": v(140, 226.83) * mm});
            skLineSegment(sketch, "E9.0.63.2", {"start": v(-430, 225.83) * mm, "end": v(-150, 225.83) * mm});
            skLineSegment(sketch, "E9.0.63.3", {"start": v(150, 225.83) * mm, "end": v(430, 225.83) * mm});
            skLineSegment(sketch, "E9.0.63.4", {"start": v(-140, 225.83) * mm, "end": v(140, 225.83) * mm});
            skLineSegment(sketch, "E9.0.63.5", {"start": v(-430, 226.83) * mm, "end": v(-150, 226.83) * mm});
            skLineSegment(sketch, "E9.0.63.6", {"start": v(430, 225.83) * mm, "end": v(430, 226.83) * mm});
            skLineSegment(sketch, "E9.0.63.7", {"start": v(150, 225.83) * mm, "end": v(150, 226.83) * mm});
            skLineSegment(sketch, "E9.0.63.8", {"start": v(140, 225.83) * mm, "end": v(140, 226.83) * mm});
            skLineSegment(sketch, "E9.0.63.9", {"start": v(-140, 225.83) * mm, "end": v(-140, 226.83) * mm});
            skLineSegment(sketch, "E9.0.63.10", {"start": v(-150, 226.83) * mm, "end": v(-150, 225.83) * mm});
            skLineSegment(sketch, "E9.0.63.11", {"start": v(-430, 226.83) * mm, "end": v(-430, 225.83) * mm});
            skLineSegment(sketch, "E9.0.64.0", {"start": v(150, 229.83) * mm, "end": v(430, 229.83) * mm});
            skLineSegment(sketch, "E9.0.64.1", {"start": v(-140, 229.83) * mm, "end": v(140, 229.83) * mm});
            skLineSegment(sketch, "E9.0.64.2", {"start": v(-430, 228.83) * mm, "end": v(-150, 228.83) * mm});
            skLineSegment(sketch, "E9.0.64.3", {"start": v(150, 228.83) * mm, "end": v(430, 228.83) * mm});
            skLineSegment(sketch, "E9.0.64.4", {"start": v(-140, 228.83) * mm, "end": v(140, 228.83) * mm});
            skLineSegment(sketch, "E9.0.64.5", {"start": v(-430, 229.83) * mm, "end": v(-150, 229.83) * mm});
            skLineSegment(sketch, "E9.0.64.6", {"start": v(430, 228.83) * mm, "end": v(430, 229.83) * mm});
            skLineSegment(sketch, "E9.0.64.7", {"start": v(150, 228.83) * mm, "end": v(150, 229.83) * mm});
            skLineSegment(sketch, "E9.0.64.8", {"start": v(140, 228.83) * mm, "end": v(140, 229.83) * mm});
            skLineSegment(sketch, "E9.0.64.9", {"start": v(-140, 228.83) * mm, "end": v(-140, 229.83) * mm});
            skLineSegment(sketch, "E9.0.64.10", {"start": v(-150, 229.83) * mm, "end": v(-150, 228.83) * mm});
            skLineSegment(sketch, "E9.0.64.11", {"start": v(-430, 229.83) * mm, "end": v(-430, 228.83) * mm});
            skLineSegment(sketch, "E9.0.65.0", {"start": v(150, 232.83) * mm, "end": v(430, 232.83) * mm});
            skLineSegment(sketch, "E9.0.65.1", {"start": v(-140, 232.83) * mm, "end": v(140, 232.83) * mm});
            skLineSegment(sketch, "E9.0.65.2", {"start": v(-430, 231.83) * mm, "end": v(-150, 231.83) * mm});
            skLineSegment(sketch, "E9.0.65.3", {"start": v(150, 231.83) * mm, "end": v(430, 231.83) * mm});
            skLineSegment(sketch, "E9.0.65.4", {"start": v(-140, 231.83) * mm, "end": v(140, 231.83) * mm});
            skLineSegment(sketch, "E9.0.65.5", {"start": v(-430, 232.83) * mm, "end": v(-150, 232.83) * mm});
            skLineSegment(sketch, "E9.0.65.6", {"start": v(430, 231.83) * mm, "end": v(430, 232.83) * mm});
            skLineSegment(sketch, "E9.0.65.7", {"start": v(150, 231.83) * mm, "end": v(150, 232.83) * mm});
            skLineSegment(sketch, "E9.0.65.8", {"start": v(140, 231.83) * mm, "end": v(140, 232.83) * mm});
            skLineSegment(sketch, "E9.0.65.9", {"start": v(-140, 231.83) * mm, "end": v(-140, 232.83) * mm});
            skLineSegment(sketch, "E9.0.65.10", {"start": v(-150, 232.83) * mm, "end": v(-150, 231.83) * mm});
            skLineSegment(sketch, "E9.0.65.11", {"start": v(-430, 232.83) * mm, "end": v(-430, 231.83) * mm});
            skLineSegment(sketch, "E9.0.66.0", {"start": v(150, 235.83) * mm, "end": v(430, 235.83) * mm});
            skLineSegment(sketch, "E9.0.66.1", {"start": v(-140, 235.83) * mm, "end": v(140, 235.83) * mm});
            skLineSegment(sketch, "E9.0.66.2", {"start": v(-430, 234.83) * mm, "end": v(-150, 234.83) * mm});
            skLineSegment(sketch, "E9.0.66.3", {"start": v(150, 234.83) * mm, "end": v(430, 234.83) * mm});
            skLineSegment(sketch, "E9.0.66.4", {"start": v(-140, 234.83) * mm, "end": v(140, 234.83) * mm});
            skLineSegment(sketch, "E9.0.66.5", {"start": v(-430, 235.83) * mm, "end": v(-150, 235.83) * mm});
            skLineSegment(sketch, "E9.0.66.6", {"start": v(430, 234.83) * mm, "end": v(430, 235.83) * mm});
            skLineSegment(sketch, "E9.0.66.7", {"start": v(150, 234.83) * mm, "end": v(150, 235.83) * mm});
            skLineSegment(sketch, "E9.0.66.8", {"start": v(140, 234.83) * mm, "end": v(140, 235.83) * mm});
            skLineSegment(sketch, "E9.0.66.9", {"start": v(-140, 234.83) * mm, "end": v(-140, 235.83) * mm});
            skLineSegment(sketch, "E9.0.66.10", {"start": v(-150, 235.83) * mm, "end": v(-150, 234.83) * mm});
            skLineSegment(sketch, "E9.0.66.11", {"start": v(-430, 235.83) * mm, "end": v(-430, 234.83) * mm});
            skLineSegment(sketch, "E9.0.67.0", {"start": v(150, 238.83) * mm, "end": v(430, 238.83) * mm});
            skLineSegment(sketch, "E9.0.67.1", {"start": v(-140, 238.83) * mm, "end": v(140, 238.83) * mm});
            skLineSegment(sketch, "E9.0.67.2", {"start": v(-430, 237.83) * mm, "end": v(-150, 237.83) * mm});
            skLineSegment(sketch, "E9.0.67.3", {"start": v(150, 237.83) * mm, "end": v(430, 237.83) * mm});
            skLineSegment(sketch, "E9.0.67.4", {"start": v(-140, 237.83) * mm, "end": v(140, 237.83) * mm});
            skLineSegment(sketch, "E9.0.67.5", {"start": v(-430, 238.83) * mm, "end": v(-150, 238.83) * mm});
            skLineSegment(sketch, "E9.0.67.6", {"start": v(430, 237.83) * mm, "end": v(430, 238.83) * mm});
            skLineSegment(sketch, "E9.0.67.7", {"start": v(150, 237.83) * mm, "end": v(150, 238.83) * mm});
            skLineSegment(sketch, "E9.0.67.8", {"start": v(140, 237.83) * mm, "end": v(140, 238.83) * mm});
            skLineSegment(sketch, "E9.0.67.9", {"start": v(-140, 237.83) * mm, "end": v(-140, 238.83) * mm});
            skLineSegment(sketch, "E9.0.67.10", {"start": v(-150, 238.83) * mm, "end": v(-150, 237.83) * mm});
            skLineSegment(sketch, "E9.0.67.11", {"start": v(-430, 238.83) * mm, "end": v(-430, 237.83) * mm});
            skLineSegment(sketch, "E9.0.68.0", {"start": v(150, 241.83) * mm, "end": v(430, 241.83) * mm});
            skLineSegment(sketch, "E9.0.68.1", {"start": v(-140, 241.83) * mm, "end": v(140, 241.83) * mm});
            skLineSegment(sketch, "E9.0.68.2", {"start": v(-430, 240.83) * mm, "end": v(-150, 240.83) * mm});
            skLineSegment(sketch, "E9.0.68.3", {"start": v(150, 240.83) * mm, "end": v(430, 240.83) * mm});
            skLineSegment(sketch, "E9.0.68.4", {"start": v(-140, 240.83) * mm, "end": v(140, 240.83) * mm});
            skLineSegment(sketch, "E9.0.68.5", {"start": v(-430, 241.83) * mm, "end": v(-150, 241.83) * mm});
            skLineSegment(sketch, "E9.0.68.6", {"start": v(430, 240.83) * mm, "end": v(430, 241.83) * mm});
            skLineSegment(sketch, "E9.0.68.7", {"start": v(150, 240.83) * mm, "end": v(150, 241.83) * mm});
            skLineSegment(sketch, "E9.0.68.8", {"start": v(140, 240.83) * mm, "end": v(140, 241.83) * mm});
            skLineSegment(sketch, "E9.0.68.9", {"start": v(-140, 240.83) * mm, "end": v(-140, 241.83) * mm});
            skLineSegment(sketch, "E9.0.68.10", {"start": v(-150, 241.83) * mm, "end": v(-150, 240.83) * mm});
            skLineSegment(sketch, "E9.0.68.11", {"start": v(-430, 241.83) * mm, "end": v(-430, 240.83) * mm});
            skLineSegment(sketch, "E9.0.69.0", {"start": v(150, 244.83) * mm, "end": v(430, 244.83) * mm});
            skLineSegment(sketch, "E9.0.69.1", {"start": v(-140, 244.83) * mm, "end": v(140, 244.83) * mm});
            skLineSegment(sketch, "E9.0.69.2", {"start": v(-430, 243.83) * mm, "end": v(-150, 243.83) * mm});
            skLineSegment(sketch, "E9.0.69.3", {"start": v(150, 243.83) * mm, "end": v(430, 243.83) * mm});
            skLineSegment(sketch, "E9.0.69.4", {"start": v(-140, 243.83) * mm, "end": v(140, 243.83) * mm});
            skLineSegment(sketch, "E9.0.69.5", {"start": v(-430, 244.83) * mm, "end": v(-150, 244.83) * mm});
            skLineSegment(sketch, "E9.0.69.6", {"start": v(430, 243.83) * mm, "end": v(430, 244.83) * mm});
            skLineSegment(sketch, "E9.0.69.7", {"start": v(150, 243.83) * mm, "end": v(150, 244.83) * mm});
            skLineSegment(sketch, "E9.0.69.8", {"start": v(140, 243.83) * mm, "end": v(140, 244.83) * mm});
            skLineSegment(sketch, "E9.0.69.9", {"start": v(-140, 243.83) * mm, "end": v(-140, 244.83) * mm});
            skLineSegment(sketch, "E9.0.69.10", {"start": v(-150, 244.83) * mm, "end": v(-150, 243.83) * mm});
            skLineSegment(sketch, "E9.0.69.11", {"start": v(-430, 244.83) * mm, "end": v(-430, 243.83) * mm});
            skLineSegment(sketch, "E9.0.70.0", {"start": v(150, 247.83) * mm, "end": v(430, 247.83) * mm});
            skLineSegment(sketch, "E9.0.70.1", {"start": v(-140, 247.83) * mm, "end": v(140, 247.83) * mm});
            skLineSegment(sketch, "E9.0.70.2", {"start": v(-430, 246.83) * mm, "end": v(-150, 246.83) * mm});
            skLineSegment(sketch, "E9.0.70.3", {"start": v(150, 246.83) * mm, "end": v(430, 246.83) * mm});
            skLineSegment(sketch, "E9.0.70.4", {"start": v(-140, 246.83) * mm, "end": v(140, 246.83) * mm});
            skLineSegment(sketch, "E9.0.70.5", {"start": v(-430, 247.83) * mm, "end": v(-150, 247.83) * mm});
            skLineSegment(sketch, "E9.0.70.6", {"start": v(430, 246.83) * mm, "end": v(430, 247.83) * mm});
            skLineSegment(sketch, "E9.0.70.7", {"start": v(150, 246.83) * mm, "end": v(150, 247.83) * mm});
            skLineSegment(sketch, "E9.0.70.8", {"start": v(140, 246.83) * mm, "end": v(140, 247.83) * mm});
            skLineSegment(sketch, "E9.0.70.9", {"start": v(-140, 246.83) * mm, "end": v(-140, 247.83) * mm});
            skLineSegment(sketch, "E9.0.70.10", {"start": v(-150, 247.83) * mm, "end": v(-150, 246.83) * mm});
            skLineSegment(sketch, "E9.0.70.11", {"start": v(-430, 247.83) * mm, "end": v(-430, 246.83) * mm});
            skLineSegment(sketch, "E9.0.71.0", {"start": v(150, 250.83) * mm, "end": v(430, 250.83) * mm});
            skLineSegment(sketch, "E9.0.71.1", {"start": v(-140, 250.83) * mm, "end": v(140, 250.83) * mm});
            skLineSegment(sketch, "E9.0.71.2", {"start": v(-430, 249.83) * mm, "end": v(-150, 249.83) * mm});
            skLineSegment(sketch, "E9.0.71.3", {"start": v(150, 249.83) * mm, "end": v(430, 249.83) * mm});
            skLineSegment(sketch, "E9.0.71.4", {"start": v(-140, 249.83) * mm, "end": v(140, 249.83) * mm});
            skLineSegment(sketch, "E9.0.71.5", {"start": v(-430, 250.83) * mm, "end": v(-150, 250.83) * mm});
            skLineSegment(sketch, "E9.0.71.6", {"start": v(430, 249.83) * mm, "end": v(430, 250.83) * mm});
            skLineSegment(sketch, "E9.0.71.7", {"start": v(150, 249.83) * mm, "end": v(150, 250.83) * mm});
            skLineSegment(sketch, "E9.0.71.8", {"start": v(140, 249.83) * mm, "end": v(140, 250.83) * mm});
            skLineSegment(sketch, "E9.0.71.9", {"start": v(-140, 249.83) * mm, "end": v(-140, 250.83) * mm});
            skLineSegment(sketch, "E9.0.71.10", {"start": v(-150, 250.83) * mm, "end": v(-150, 249.83) * mm});
            skLineSegment(sketch, "E9.0.71.11", {"start": v(-430, 250.83) * mm, "end": v(-430, 249.83) * mm});
            skLineSegment(sketch, "E9.0.72.0", {"start": v(150, 253.83) * mm, "end": v(430, 253.83) * mm});
            skLineSegment(sketch, "E9.0.72.1", {"start": v(-140, 253.83) * mm, "end": v(140, 253.83) * mm});
            skLineSegment(sketch, "E9.0.72.2", {"start": v(-430, 252.83) * mm, "end": v(-150, 252.83) * mm});
            skLineSegment(sketch, "E9.0.72.3", {"start": v(150, 252.83) * mm, "end": v(430, 252.83) * mm});
            skLineSegment(sketch, "E9.0.72.4", {"start": v(-140, 252.83) * mm, "end": v(140, 252.83) * mm});
            skLineSegment(sketch, "E9.0.72.5", {"start": v(-430, 253.83) * mm, "end": v(-150, 253.83) * mm});
            skLineSegment(sketch, "E9.0.72.6", {"start": v(430, 252.83) * mm, "end": v(430, 253.83) * mm});
            skLineSegment(sketch, "E9.0.72.7", {"start": v(150, 252.83) * mm, "end": v(150, 253.83) * mm});
            skLineSegment(sketch, "E9.0.72.8", {"start": v(140, 252.83) * mm, "end": v(140, 253.83) * mm});
            skLineSegment(sketch, "E9.0.72.9", {"start": v(-140, 252.83) * mm, "end": v(-140, 253.83) * mm});
            skLineSegment(sketch, "E9.0.72.10", {"start": v(-150, 253.83) * mm, "end": v(-150, 252.83) * mm});
            skLineSegment(sketch, "E9.0.72.11", {"start": v(-430, 253.83) * mm, "end": v(-430, 252.83) * mm});
            skLineSegment(sketch, "E9.0.73.0", {"start": v(150, 256.83) * mm, "end": v(430, 256.83) * mm});
            skLineSegment(sketch, "E9.0.73.1", {"start": v(-140, 256.83) * mm, "end": v(140, 256.83) * mm});
            skLineSegment(sketch, "E9.0.73.2", {"start": v(-430, 255.83) * mm, "end": v(-150, 255.83) * mm});
            skLineSegment(sketch, "E9.0.73.3", {"start": v(150, 255.83) * mm, "end": v(430, 255.83) * mm});
            skLineSegment(sketch, "E9.0.73.4", {"start": v(-140, 255.83) * mm, "end": v(140, 255.83) * mm});
            skLineSegment(sketch, "E9.0.73.5", {"start": v(-430, 256.83) * mm, "end": v(-150, 256.83) * mm});
            skLineSegment(sketch, "E9.0.73.6", {"start": v(430, 255.83) * mm, "end": v(430, 256.83) * mm});
            skLineSegment(sketch, "E9.0.73.7", {"start": v(150, 255.83) * mm, "end": v(150, 256.83) * mm});
            skLineSegment(sketch, "E9.0.73.8", {"start": v(140, 255.83) * mm, "end": v(140, 256.83) * mm});
            skLineSegment(sketch, "E9.0.73.9", {"start": v(-140, 255.83) * mm, "end": v(-140, 256.83) * mm});
            skLineSegment(sketch, "E9.0.73.10", {"start": v(-150, 256.83) * mm, "end": v(-150, 255.83) * mm});
            skLineSegment(sketch, "E9.0.73.11", {"start": v(-430, 256.83) * mm, "end": v(-430, 255.83) * mm});
            skLineSegment(sketch, "E9.0.74.0", {"start": v(150, 259.83) * mm, "end": v(430, 259.83) * mm});
            skLineSegment(sketch, "E9.0.74.1", {"start": v(-140, 259.83) * mm, "end": v(140, 259.83) * mm});
            skLineSegment(sketch, "E9.0.74.2", {"start": v(-430, 258.83) * mm, "end": v(-150, 258.83) * mm});
            skLineSegment(sketch, "E9.0.74.3", {"start": v(150, 258.83) * mm, "end": v(430, 258.83) * mm});
            skLineSegment(sketch, "E9.0.74.4", {"start": v(-140, 258.83) * mm, "end": v(140, 258.83) * mm});
            skLineSegment(sketch, "E9.0.74.5", {"start": v(-430, 259.83) * mm, "end": v(-150, 259.83) * mm});
            skLineSegment(sketch, "E9.0.74.6", {"start": v(430, 258.83) * mm, "end": v(430, 259.83) * mm});
            skLineSegment(sketch, "E9.0.74.7", {"start": v(150, 258.83) * mm, "end": v(150, 259.83) * mm});
            skLineSegment(sketch, "E9.0.74.8", {"start": v(140, 258.83) * mm, "end": v(140, 259.83) * mm});
            skLineSegment(sketch, "E9.0.74.9", {"start": v(-140, 258.83) * mm, "end": v(-140, 259.83) * mm});
            skLineSegment(sketch, "E9.0.74.10", {"start": v(-150, 259.83) * mm, "end": v(-150, 258.83) * mm});
            skLineSegment(sketch, "E9.0.74.11", {"start": v(-430, 259.83) * mm, "end": v(-430, 258.83) * mm});
            skLineSegment(sketch, "E9.0.75.0", {"start": v(150, 262.83) * mm, "end": v(430, 262.83) * mm});
            skLineSegment(sketch, "E9.0.75.1", {"start": v(-140, 262.83) * mm, "end": v(140, 262.83) * mm});
            skLineSegment(sketch, "E9.0.75.2", {"start": v(-430, 261.83) * mm, "end": v(-150, 261.83) * mm});
            skLineSegment(sketch, "E9.0.75.3", {"start": v(150, 261.83) * mm, "end": v(430, 261.83) * mm});
            skLineSegment(sketch, "E9.0.75.4", {"start": v(-140, 261.83) * mm, "end": v(140, 261.83) * mm});
            skLineSegment(sketch, "E9.0.75.5", {"start": v(-430, 262.83) * mm, "end": v(-150, 262.83) * mm});
            skLineSegment(sketch, "E9.0.75.6", {"start": v(430, 261.83) * mm, "end": v(430, 262.83) * mm});
            skLineSegment(sketch, "E9.0.75.7", {"start": v(150, 261.83) * mm, "end": v(150, 262.83) * mm});
            skLineSegment(sketch, "E9.0.75.8", {"start": v(140, 261.83) * mm, "end": v(140, 262.83) * mm});
            skLineSegment(sketch, "E9.0.75.9", {"start": v(-140, 261.83) * mm, "end": v(-140, 262.83) * mm});
            skLineSegment(sketch, "E9.0.75.10", {"start": v(-150, 262.83) * mm, "end": v(-150, 261.83) * mm});
            skLineSegment(sketch, "E9.0.75.11", {"start": v(-430, 262.83) * mm, "end": v(-430, 261.83) * mm});
            skLineSegment(sketch, "E9.0.76.0", {"start": v(150, 265.83) * mm, "end": v(430, 265.83) * mm});
            skLineSegment(sketch, "E9.0.76.1", {"start": v(-140, 265.83) * mm, "end": v(140, 265.83) * mm});
            skLineSegment(sketch, "E9.0.76.2", {"start": v(-430, 264.83) * mm, "end": v(-150, 264.83) * mm});
            skLineSegment(sketch, "E9.0.76.3", {"start": v(150, 264.83) * mm, "end": v(430, 264.83) * mm});
            skLineSegment(sketch, "E9.0.76.4", {"start": v(-140, 264.83) * mm, "end": v(140, 264.83) * mm});
            skLineSegment(sketch, "E9.0.76.5", {"start": v(-430, 265.83) * mm, "end": v(-150, 265.83) * mm});
            skLineSegment(sketch, "E9.0.76.6", {"start": v(430, 264.83) * mm, "end": v(430, 265.83) * mm});
            skLineSegment(sketch, "E9.0.76.7", {"start": v(150, 264.83) * mm, "end": v(150, 265.83) * mm});
            skLineSegment(sketch, "E9.0.76.8", {"start": v(140, 264.83) * mm, "end": v(140, 265.83) * mm});
            skLineSegment(sketch, "E9.0.76.9", {"start": v(-140, 264.83) * mm, "end": v(-140, 265.83) * mm});
            skLineSegment(sketch, "E9.0.76.10", {"start": v(-150, 265.83) * mm, "end": v(-150, 264.83) * mm});
            skLineSegment(sketch, "E9.0.76.11", {"start": v(-430, 265.83) * mm, "end": v(-430, 264.83) * mm});
            skLineSegment(sketch, "E9.0.77.0", {"start": v(150, 268.83) * mm, "end": v(430, 268.83) * mm});
            skLineSegment(sketch, "E9.0.77.1", {"start": v(-140, 268.83) * mm, "end": v(140, 268.83) * mm});
            skLineSegment(sketch, "E9.0.77.2", {"start": v(-430, 267.83) * mm, "end": v(-150, 267.83) * mm});
            skLineSegment(sketch, "E9.0.77.3", {"start": v(150, 267.83) * mm, "end": v(430, 267.83) * mm});
            skLineSegment(sketch, "E9.0.77.4", {"start": v(-140, 267.83) * mm, "end": v(140, 267.83) * mm});
            skLineSegment(sketch, "E9.0.77.5", {"start": v(-430, 268.83) * mm, "end": v(-150, 268.83) * mm});
            skLineSegment(sketch, "E9.0.77.6", {"start": v(430, 267.83) * mm, "end": v(430, 268.83) * mm});
            skLineSegment(sketch, "E9.0.77.7", {"start": v(150, 267.83) * mm, "end": v(150, 268.83) * mm});
            skLineSegment(sketch, "E9.0.77.8", {"start": v(140, 267.83) * mm, "end": v(140, 268.83) * mm});
            skLineSegment(sketch, "E9.0.77.9", {"start": v(-140, 267.83) * mm, "end": v(-140, 268.83) * mm});
            skLineSegment(sketch, "E9.0.77.10", {"start": v(-150, 268.83) * mm, "end": v(-150, 267.83) * mm});
            skLineSegment(sketch, "E9.0.77.11", {"start": v(-430, 268.83) * mm, "end": v(-430, 267.83) * mm});
            skLineSegment(sketch, "E9.0.78.0", {"start": v(150, 271.83) * mm, "end": v(430, 271.83) * mm});
            skLineSegment(sketch, "E9.0.78.1", {"start": v(-140, 271.83) * mm, "end": v(140, 271.83) * mm});
            skLineSegment(sketch, "E9.0.78.2", {"start": v(-430, 270.83) * mm, "end": v(-150, 270.83) * mm});
            skLineSegment(sketch, "E9.0.78.3", {"start": v(150, 270.83) * mm, "end": v(430, 270.83) * mm});
            skLineSegment(sketch, "E9.0.78.4", {"start": v(-140, 270.83) * mm, "end": v(140, 270.83) * mm});
            skLineSegment(sketch, "E9.0.78.5", {"start": v(-430, 271.83) * mm, "end": v(-150, 271.83) * mm});
            skLineSegment(sketch, "E9.0.78.6", {"start": v(430, 270.83) * mm, "end": v(430, 271.83) * mm});
            skLineSegment(sketch, "E9.0.78.7", {"start": v(150, 270.83) * mm, "end": v(150, 271.83) * mm});
            skLineSegment(sketch, "E9.0.78.8", {"start": v(140, 270.83) * mm, "end": v(140, 271.83) * mm});
            skLineSegment(sketch, "E9.0.78.9", {"start": v(-140, 270.83) * mm, "end": v(-140, 271.83) * mm});
            skLineSegment(sketch, "E9.0.78.10", {"start": v(-150, 271.83) * mm, "end": v(-150, 270.83) * mm});
            skLineSegment(sketch, "E9.0.78.11", {"start": v(-430, 271.83) * mm, "end": v(-430, 270.83) * mm});
            skLineSegment(sketch, "E9.0.79.0", {"start": v(150, 274.83) * mm, "end": v(430, 274.83) * mm});
            skLineSegment(sketch, "E9.0.79.1", {"start": v(-140, 274.83) * mm, "end": v(140, 274.83) * mm});
            skLineSegment(sketch, "E9.0.79.2", {"start": v(-430, 273.83) * mm, "end": v(-150, 273.83) * mm});
            skLineSegment(sketch, "E9.0.79.3", {"start": v(150, 273.83) * mm, "end": v(430, 273.83) * mm});
            skLineSegment(sketch, "E9.0.79.4", {"start": v(-140, 273.83) * mm, "end": v(140, 273.83) * mm});
            skLineSegment(sketch, "E9.0.79.5", {"start": v(-430, 274.83) * mm, "end": v(-150, 274.83) * mm});
            skLineSegment(sketch, "E9.0.79.6", {"start": v(430, 273.83) * mm, "end": v(430, 274.83) * mm});
            skLineSegment(sketch, "E9.0.79.7", {"start": v(150, 273.83) * mm, "end": v(150, 274.83) * mm});
            skLineSegment(sketch, "E9.0.79.8", {"start": v(140, 273.83) * mm, "end": v(140, 274.83) * mm});
            skLineSegment(sketch, "E9.0.79.9", {"start": v(-140, 273.83) * mm, "end": v(-140, 274.83) * mm});
            skLineSegment(sketch, "E9.0.79.10", {"start": v(-150, 274.83) * mm, "end": v(-150, 273.83) * mm});
            skLineSegment(sketch, "E9.0.79.11", {"start": v(-430, 274.83) * mm, "end": v(-430, 273.83) * mm});
            skLineSegment(sketch, "E9.0.80.0", {"start": v(150, 277.83) * mm, "end": v(430, 277.83) * mm});
            skLineSegment(sketch, "E9.0.80.1", {"start": v(-140, 277.83) * mm, "end": v(140, 277.83) * mm});
            skLineSegment(sketch, "E9.0.80.2", {"start": v(-430, 276.83) * mm, "end": v(-150, 276.83) * mm});
            skLineSegment(sketch, "E9.0.80.3", {"start": v(150, 276.83) * mm, "end": v(430, 276.83) * mm});
            skLineSegment(sketch, "E9.0.80.4", {"start": v(-140, 276.83) * mm, "end": v(140, 276.83) * mm});
            skLineSegment(sketch, "E9.0.80.5", {"start": v(-430, 277.83) * mm, "end": v(-150, 277.83) * mm});
            skLineSegment(sketch, "E9.0.80.6", {"start": v(430, 276.83) * mm, "end": v(430, 277.83) * mm});
            skLineSegment(sketch, "E9.0.80.7", {"start": v(150, 276.83) * mm, "end": v(150, 277.83) * mm});
            skLineSegment(sketch, "E9.0.80.8", {"start": v(140, 276.83) * mm, "end": v(140, 277.83) * mm});
            skLineSegment(sketch, "E9.0.80.9", {"start": v(-140, 276.83) * mm, "end": v(-140, 277.83) * mm});
            skLineSegment(sketch, "E9.0.80.10", {"start": v(-150, 277.83) * mm, "end": v(-150, 276.83) * mm});
            skLineSegment(sketch, "E9.0.80.11", {"start": v(-430, 277.83) * mm, "end": v(-430, 276.83) * mm});
            skLineSegment(sketch, "E9.0.81.0", {"start": v(150, 280.83) * mm, "end": v(430, 280.83) * mm});
            skLineSegment(sketch, "E9.0.81.1", {"start": v(-140, 280.83) * mm, "end": v(140, 280.83) * mm});
            skLineSegment(sketch, "E9.0.81.2", {"start": v(-430, 279.83) * mm, "end": v(-150, 279.83) * mm});
            skLineSegment(sketch, "E9.0.81.3", {"start": v(150, 279.83) * mm, "end": v(430, 279.83) * mm});
            skLineSegment(sketch, "E9.0.81.4", {"start": v(-140, 279.83) * mm, "end": v(140, 279.83) * mm});
            skLineSegment(sketch, "E9.0.81.5", {"start": v(-430, 280.83) * mm, "end": v(-150, 280.83) * mm});
            skLineSegment(sketch, "E9.0.81.6", {"start": v(430, 279.83) * mm, "end": v(430, 280.83) * mm});
            skLineSegment(sketch, "E9.0.81.7", {"start": v(150, 279.83) * mm, "end": v(150, 280.83) * mm});
            skLineSegment(sketch, "E9.0.81.8", {"start": v(140, 279.83) * mm, "end": v(140, 280.83) * mm});
            skLineSegment(sketch, "E9.0.81.9", {"start": v(-140, 279.83) * mm, "end": v(-140, 280.83) * mm});
            skLineSegment(sketch, "E9.0.81.10", {"start": v(-150, 280.83) * mm, "end": v(-150, 279.83) * mm});
            skLineSegment(sketch, "E9.0.81.11", {"start": v(-430, 280.83) * mm, "end": v(-430, 279.83) * mm});
            skLineSegment(sketch, "E9.0.82.0", {"start": v(150, 283.83) * mm, "end": v(430, 283.83) * mm});
            skLineSegment(sketch, "E9.0.82.1", {"start": v(-140, 283.83) * mm, "end": v(140, 283.83) * mm});
            skLineSegment(sketch, "E9.0.82.2", {"start": v(-430, 282.83) * mm, "end": v(-150, 282.83) * mm});
            skLineSegment(sketch, "E9.0.82.3", {"start": v(150, 282.83) * mm, "end": v(430, 282.83) * mm});
            skLineSegment(sketch, "E9.0.82.4", {"start": v(-140, 282.83) * mm, "end": v(140, 282.83) * mm});
            skLineSegment(sketch, "E9.0.82.5", {"start": v(-430, 283.83) * mm, "end": v(-150, 283.83) * mm});
            skLineSegment(sketch, "E9.0.82.6", {"start": v(430, 282.83) * mm, "end": v(430, 283.83) * mm});
            skLineSegment(sketch, "E9.0.82.7", {"start": v(150, 282.83) * mm, "end": v(150, 283.83) * mm});
            skLineSegment(sketch, "E9.0.82.8", {"start": v(140, 282.83) * mm, "end": v(140, 283.83) * mm});
            skLineSegment(sketch, "E9.0.82.9", {"start": v(-140, 282.83) * mm, "end": v(-140, 283.83) * mm});
            skLineSegment(sketch, "E9.0.82.10", {"start": v(-150, 283.83) * mm, "end": v(-150, 282.83) * mm});
            skLineSegment(sketch, "E9.0.82.11", {"start": v(-430, 283.83) * mm, "end": v(-430, 282.83) * mm});
            skLineSegment(sketch, "E9.0.83.0", {"start": v(150, 286.83) * mm, "end": v(430, 286.83) * mm});
            skLineSegment(sketch, "E9.0.83.1", {"start": v(-140, 286.83) * mm, "end": v(140, 286.83) * mm});
            skLineSegment(sketch, "E9.0.83.2", {"start": v(-430, 285.83) * mm, "end": v(-150, 285.83) * mm});
            skLineSegment(sketch, "E9.0.83.3", {"start": v(150, 285.83) * mm, "end": v(430, 285.83) * mm});
            skLineSegment(sketch, "E9.0.83.4", {"start": v(-140, 285.83) * mm, "end": v(140, 285.83) * mm});
            skLineSegment(sketch, "E9.0.83.5", {"start": v(-430, 286.83) * mm, "end": v(-150, 286.83) * mm});
            skLineSegment(sketch, "E9.0.83.6", {"start": v(430, 285.83) * mm, "end": v(430, 286.83) * mm});
            skLineSegment(sketch, "E9.0.83.7", {"start": v(150, 285.83) * mm, "end": v(150, 286.83) * mm});
            skLineSegment(sketch, "E9.0.83.8", {"start": v(140, 285.83) * mm, "end": v(140, 286.83) * mm});
            skLineSegment(sketch, "E9.0.83.9", {"start": v(-140, 285.83) * mm, "end": v(-140, 286.83) * mm});
            skLineSegment(sketch, "E9.0.83.10", {"start": v(-150, 286.83) * mm, "end": v(-150, 285.83) * mm});
            skLineSegment(sketch, "E9.0.83.11", {"start": v(-430, 286.83) * mm, "end": v(-430, 285.83) * mm});
            skLineSegment(sketch, "E9.0.84.0", {"start": v(150, 289.83) * mm, "end": v(430, 289.83) * mm});
            skLineSegment(sketch, "E9.0.84.1", {"start": v(-140, 289.83) * mm, "end": v(140, 289.83) * mm});
            skLineSegment(sketch, "E9.0.84.2", {"start": v(-430, 288.83) * mm, "end": v(-150, 288.83) * mm});
            skLineSegment(sketch, "E9.0.84.3", {"start": v(150, 288.83) * mm, "end": v(430, 288.83) * mm});
            skLineSegment(sketch, "E9.0.84.4", {"start": v(-140, 288.83) * mm, "end": v(140, 288.83) * mm});
            skLineSegment(sketch, "E9.0.84.5", {"start": v(-430, 289.83) * mm, "end": v(-150, 289.83) * mm});
            skLineSegment(sketch, "E9.0.84.6", {"start": v(430, 288.83) * mm, "end": v(430, 289.83) * mm});
            skLineSegment(sketch, "E9.0.84.7", {"start": v(150, 288.83) * mm, "end": v(150, 289.83) * mm});
            skLineSegment(sketch, "E9.0.84.8", {"start": v(140, 288.83) * mm, "end": v(140, 289.83) * mm});
            skLineSegment(sketch, "E9.0.84.9", {"start": v(-140, 288.83) * mm, "end": v(-140, 289.83) * mm});
            skLineSegment(sketch, "E9.0.84.10", {"start": v(-150, 289.83) * mm, "end": v(-150, 288.83) * mm});
            skLineSegment(sketch, "E9.0.84.11", {"start": v(-430, 289.83) * mm, "end": v(-430, 288.83) * mm});
            skLineSegment(sketch, "E9.0.85.0", {"start": v(150, 292.83) * mm, "end": v(430, 292.83) * mm});
            skLineSegment(sketch, "E9.0.85.1", {"start": v(-140, 292.83) * mm, "end": v(140, 292.83) * mm});
            skLineSegment(sketch, "E9.0.85.2", {"start": v(-430, 291.83) * mm, "end": v(-150, 291.83) * mm});
            skLineSegment(sketch, "E9.0.85.3", {"start": v(150, 291.83) * mm, "end": v(430, 291.83) * mm});
            skLineSegment(sketch, "E9.0.85.4", {"start": v(-140, 291.83) * mm, "end": v(140, 291.83) * mm});
            skLineSegment(sketch, "E9.0.85.5", {"start": v(-430, 292.83) * mm, "end": v(-150, 292.83) * mm});
            skLineSegment(sketch, "E9.0.85.6", {"start": v(430, 291.83) * mm, "end": v(430, 292.83) * mm});
            skLineSegment(sketch, "E9.0.85.7", {"start": v(150, 291.83) * mm, "end": v(150, 292.83) * mm});
            skLineSegment(sketch, "E9.0.85.8", {"start": v(140, 291.83) * mm, "end": v(140, 292.83) * mm});
            skLineSegment(sketch, "E9.0.85.9", {"start": v(-140, 291.83) * mm, "end": v(-140, 292.83) * mm});
            skLineSegment(sketch, "E9.0.85.10", {"start": v(-150, 292.83) * mm, "end": v(-150, 291.83) * mm});
            skLineSegment(sketch, "E9.0.85.11", {"start": v(-430, 292.83) * mm, "end": v(-430, 291.83) * mm});
            skLineSegment(sketch, "E9.0.86.0", {"start": v(150, 295.83) * mm, "end": v(430, 295.83) * mm});
            skLineSegment(sketch, "E9.0.86.1", {"start": v(-140, 295.83) * mm, "end": v(140, 295.83) * mm});
            skLineSegment(sketch, "E9.0.86.2", {"start": v(-430, 294.83) * mm, "end": v(-150, 294.83) * mm});
            skLineSegment(sketch, "E9.0.86.3", {"start": v(150, 294.83) * mm, "end": v(430, 294.83) * mm});
            skLineSegment(sketch, "E9.0.86.4", {"start": v(-140, 294.83) * mm, "end": v(140, 294.83) * mm});
            skLineSegment(sketch, "E9.0.86.5", {"start": v(-430, 295.83) * mm, "end": v(-150, 295.83) * mm});
            skLineSegment(sketch, "E9.0.86.6", {"start": v(430, 294.83) * mm, "end": v(430, 295.83) * mm});
            skLineSegment(sketch, "E9.0.86.7", {"start": v(150, 294.83) * mm, "end": v(150, 295.83) * mm});
            skLineSegment(sketch, "E9.0.86.8", {"start": v(140, 294.83) * mm, "end": v(140, 295.83) * mm});
            skLineSegment(sketch, "E9.0.86.9", {"start": v(-140, 294.83) * mm, "end": v(-140, 295.83) * mm});
            skLineSegment(sketch, "E9.0.86.10", {"start": v(-150, 295.83) * mm, "end": v(-150, 294.83) * mm});
            skLineSegment(sketch, "E9.0.86.11", {"start": v(-430, 295.83) * mm, "end": v(-430, 294.83) * mm});
            skLineSegment(sketch, "E9.0.87.0", {"start": v(150, 298.83) * mm, "end": v(430, 298.83) * mm});
            skLineSegment(sketch, "E9.0.87.1", {"start": v(-140, 298.83) * mm, "end": v(140, 298.83) * mm});
            skLineSegment(sketch, "E9.0.87.2", {"start": v(-430, 297.83) * mm, "end": v(-150, 297.83) * mm});
            skLineSegment(sketch, "E9.0.87.3", {"start": v(150, 297.83) * mm, "end": v(430, 297.83) * mm});
            skLineSegment(sketch, "E9.0.87.4", {"start": v(-140, 297.83) * mm, "end": v(140, 297.83) * mm});
            skLineSegment(sketch, "E9.0.87.5", {"start": v(-430, 298.83) * mm, "end": v(-150, 298.83) * mm});
            skLineSegment(sketch, "E9.0.87.6", {"start": v(430, 297.83) * mm, "end": v(430, 298.83) * mm});
            skLineSegment(sketch, "E9.0.87.7", {"start": v(150, 297.83) * mm, "end": v(150, 298.83) * mm});
            skLineSegment(sketch, "E9.0.87.8", {"start": v(140, 297.83) * mm, "end": v(140, 298.83) * mm});
            skLineSegment(sketch, "E9.0.87.9", {"start": v(-140, 297.83) * mm, "end": v(-140, 298.83) * mm});
            skLineSegment(sketch, "E9.0.87.10", {"start": v(-150, 298.83) * mm, "end": v(-150, 297.83) * mm});
            skLineSegment(sketch, "E9.0.87.11", {"start": v(-430, 298.83) * mm, "end": v(-430, 297.83) * mm});
            skLineSegment(sketch, "E9.0.88.0", {"start": v(150, 301.83) * mm, "end": v(430, 301.83) * mm});
            skLineSegment(sketch, "E9.0.88.1", {"start": v(-140, 301.83) * mm, "end": v(140, 301.83) * mm});
            skLineSegment(sketch, "E9.0.88.2", {"start": v(-430, 300.83) * mm, "end": v(-150, 300.83) * mm});
            skLineSegment(sketch, "E9.0.88.3", {"start": v(150, 300.83) * mm, "end": v(430, 300.83) * mm});
            skLineSegment(sketch, "E9.0.88.4", {"start": v(-140, 300.83) * mm, "end": v(140, 300.83) * mm});
            skLineSegment(sketch, "E9.0.88.5", {"start": v(-430, 301.83) * mm, "end": v(-150, 301.83) * mm});
            skLineSegment(sketch, "E9.0.88.6", {"start": v(430, 300.83) * mm, "end": v(430, 301.83) * mm});
            skLineSegment(sketch, "E9.0.88.7", {"start": v(150, 300.83) * mm, "end": v(150, 301.83) * mm});
            skLineSegment(sketch, "E9.0.88.8", {"start": v(140, 300.83) * mm, "end": v(140, 301.83) * mm});
            skLineSegment(sketch, "E9.0.88.9", {"start": v(-140, 300.83) * mm, "end": v(-140, 301.83) * mm});
            skLineSegment(sketch, "E9.0.88.10", {"start": v(-150, 301.83) * mm, "end": v(-150, 300.83) * mm});
            skLineSegment(sketch, "E9.0.88.11", {"start": v(-430, 301.83) * mm, "end": v(-430, 300.83) * mm});
            skLineSegment(sketch, "E9.0.89.0", {"start": v(150, 304.83) * mm, "end": v(430, 304.83) * mm});
            skLineSegment(sketch, "E9.0.89.1", {"start": v(-140, 304.83) * mm, "end": v(140, 304.83) * mm});
            skLineSegment(sketch, "E9.0.89.2", {"start": v(-430, 303.83) * mm, "end": v(-150, 303.83) * mm});
            skLineSegment(sketch, "E9.0.89.3", {"start": v(150, 303.83) * mm, "end": v(430, 303.83) * mm});
            skLineSegment(sketch, "E9.0.89.4", {"start": v(-140, 303.83) * mm, "end": v(140, 303.83) * mm});
            skLineSegment(sketch, "E9.0.89.5", {"start": v(-430, 304.83) * mm, "end": v(-150, 304.83) * mm});
            skLineSegment(sketch, "E9.0.89.6", {"start": v(430, 303.83) * mm, "end": v(430, 304.83) * mm});
            skLineSegment(sketch, "E9.0.89.7", {"start": v(150, 303.83) * mm, "end": v(150, 304.83) * mm});
            skLineSegment(sketch, "E9.0.89.8", {"start": v(140, 303.83) * mm, "end": v(140, 304.83) * mm});
            skLineSegment(sketch, "E9.0.89.9", {"start": v(-140, 303.83) * mm, "end": v(-140, 304.83) * mm});
            skLineSegment(sketch, "E9.0.89.10", {"start": v(-150, 304.83) * mm, "end": v(-150, 303.83) * mm});
            skLineSegment(sketch, "E9.0.89.11", {"start": v(-430, 304.83) * mm, "end": v(-430, 303.83) * mm});
            skLineSegment(sketch, "E9.direction1", {"start": v(-430, 36.83) * mm, "end": v(-405, 36.83) * mm, "construction": true});
            skLineSegment(sketch, "E9.direction2", {"start": v(-430, 36.83) * mm, "end": v(-430, 39.83) * mm, "construction": true});
            skLineSegment(sketch, "E10.0.0.90", {"start": v(150, 307.83) * mm, "end": v(430, 307.83) * mm});
            skLineSegment(sketch, "E10.3.0.90", {"start": v(-140, 307.83) * mm, "end": v(140, 307.83) * mm});
            skLineSegment(sketch, "E10.6.0.90", {"start": v(-430, 306.83) * mm, "end": v(-150, 306.83) * mm});
            skLineSegment(sketch, "E10.9.0.90", {"start": v(150, 306.83) * mm, "end": v(430, 306.83) * mm});
            skLineSegment(sketch, "E10.12.0.90", {"start": v(-140, 306.83) * mm, "end": v(140, 306.83) * mm});
            skLineSegment(sketch, "E10.15.0.90", {"start": v(-430, 307.83) * mm, "end": v(-150, 307.83) * mm});
            skLineSegment(sketch, "E10.18.0.90", {"start": v(430, 306.83) * mm, "end": v(430, 307.83) * mm});
            skLineSegment(sketch, "E10.21.0.90", {"start": v(150, 306.83) * mm, "end": v(150, 307.83) * mm});
            skLineSegment(sketch, "E10.24.0.90", {"start": v(140, 306.83) * mm, "end": v(140, 307.83) * mm});
            skLineSegment(sketch, "E10.27.0.90", {"start": v(-140, 306.83) * mm, "end": v(-140, 307.83) * mm});
            skLineSegment(sketch, "E10.30.0.90", {"start": v(-150, 307.83) * mm, "end": v(-150, 306.83) * mm});
            skLineSegment(sketch, "E10.33.0.90", {"start": v(-430, 307.83) * mm, "end": v(-430, 306.83) * mm});
            skLineSegment(sketch, "E10.0.0.91", {"start": v(150, 310.83) * mm, "end": v(430, 310.83) * mm});
            skLineSegment(sketch, "E10.3.0.91", {"start": v(-140, 310.83) * mm, "end": v(140, 310.83) * mm});
            skLineSegment(sketch, "E10.6.0.91", {"start": v(-430, 309.83) * mm, "end": v(-150, 309.83) * mm});
            skLineSegment(sketch, "E10.9.0.91", {"start": v(150, 309.83) * mm, "end": v(430, 309.83) * mm});
            skLineSegment(sketch, "E10.12.0.91", {"start": v(-140, 309.83) * mm, "end": v(140, 309.83) * mm});
            skLineSegment(sketch, "E10.15.0.91", {"start": v(-430, 310.83) * mm, "end": v(-150, 310.83) * mm});
            skLineSegment(sketch, "E10.18.0.91", {"start": v(430, 309.83) * mm, "end": v(430, 310.83) * mm});
            skLineSegment(sketch, "E10.21.0.91", {"start": v(150, 309.83) * mm, "end": v(150, 310.83) * mm});
            skLineSegment(sketch, "E10.24.0.91", {"start": v(140, 309.83) * mm, "end": v(140, 310.83) * mm});
            skLineSegment(sketch, "E10.27.0.91", {"start": v(-140, 309.83) * mm, "end": v(-140, 310.83) * mm});
            skLineSegment(sketch, "E10.30.0.91", {"start": v(-150, 310.83) * mm, "end": v(-150, 309.83) * mm});
            skLineSegment(sketch, "E10.33.0.91", {"start": v(-430, 310.83) * mm, "end": v(-430, 309.83) * mm});
            skLineSegment(sketch, "E10.0.0.92", {"start": v(150, 313.83) * mm, "end": v(430, 313.83) * mm});
            skLineSegment(sketch, "E10.3.0.92", {"start": v(-140, 313.83) * mm, "end": v(140, 313.83) * mm});
            skLineSegment(sketch, "E10.6.0.92", {"start": v(-430, 312.83) * mm, "end": v(-150, 312.83) * mm});
            skLineSegment(sketch, "E10.9.0.92", {"start": v(150, 312.83) * mm, "end": v(430, 312.83) * mm});
            skLineSegment(sketch, "E10.12.0.92", {"start": v(-140, 312.83) * mm, "end": v(140, 312.83) * mm});
            skLineSegment(sketch, "E10.15.0.92", {"start": v(-430, 313.83) * mm, "end": v(-150, 313.83) * mm});
            skLineSegment(sketch, "E10.18.0.92", {"start": v(430, 312.83) * mm, "end": v(430, 313.83) * mm});
            skLineSegment(sketch, "E10.21.0.92", {"start": v(150, 312.83) * mm, "end": v(150, 313.83) * mm});
            skLineSegment(sketch, "E10.24.0.92", {"start": v(140, 312.83) * mm, "end": v(140, 313.83) * mm});
            skLineSegment(sketch, "E10.27.0.92", {"start": v(-140, 312.83) * mm, "end": v(-140, 313.83) * mm});
            skLineSegment(sketch, "E10.30.0.92", {"start": v(-150, 313.83) * mm, "end": v(-150, 312.83) * mm});
            skLineSegment(sketch, "E10.33.0.92", {"start": v(-430, 313.83) * mm, "end": v(-430, 312.83) * mm});
            skLineSegment(sketch, "E10.0.0.93", {"start": v(150, 316.83) * mm, "end": v(430, 316.83) * mm});
            skLineSegment(sketch, "E10.3.0.93", {"start": v(-140, 316.83) * mm, "end": v(140, 316.83) * mm});
            skLineSegment(sketch, "E10.6.0.93", {"start": v(-430, 315.83) * mm, "end": v(-150, 315.83) * mm});
            skLineSegment(sketch, "E10.9.0.93", {"start": v(150, 315.83) * mm, "end": v(430, 315.83) * mm});
            skLineSegment(sketch, "E10.12.0.93", {"start": v(-140, 315.83) * mm, "end": v(140, 315.83) * mm});
            skLineSegment(sketch, "E10.15.0.93", {"start": v(-430, 316.83) * mm, "end": v(-150, 316.83) * mm});
            skLineSegment(sketch, "E10.18.0.93", {"start": v(430, 315.83) * mm, "end": v(430, 316.83) * mm});
            skLineSegment(sketch, "E10.21.0.93", {"start": v(150, 315.83) * mm, "end": v(150, 316.83) * mm});
            skLineSegment(sketch, "E10.24.0.93", {"start": v(140, 315.83) * mm, "end": v(140, 316.83) * mm});
            skLineSegment(sketch, "E10.27.0.93", {"start": v(-140, 315.83) * mm, "end": v(-140, 316.83) * mm});
            skLineSegment(sketch, "E10.30.0.93", {"start": v(-150, 316.83) * mm, "end": v(-150, 315.83) * mm});
            skLineSegment(sketch, "E10.33.0.93", {"start": v(-430, 316.83) * mm, "end": v(-430, 315.83) * mm});
            skLineSegment(sketch, "E10.0.0.94", {"start": v(150, 319.83) * mm, "end": v(430, 319.83) * mm});
            skLineSegment(sketch, "E10.3.0.94", {"start": v(-140, 319.83) * mm, "end": v(140, 319.83) * mm});
            skLineSegment(sketch, "E10.6.0.94", {"start": v(-430, 318.83) * mm, "end": v(-150, 318.83) * mm});
            skLineSegment(sketch, "E10.9.0.94", {"start": v(150, 318.83) * mm, "end": v(430, 318.83) * mm});
            skLineSegment(sketch, "E10.12.0.94", {"start": v(-140, 318.83) * mm, "end": v(140, 318.83) * mm});
            skLineSegment(sketch, "E10.15.0.94", {"start": v(-430, 319.83) * mm, "end": v(-150, 319.83) * mm});
            skLineSegment(sketch, "E10.18.0.94", {"start": v(430, 318.83) * mm, "end": v(430, 319.83) * mm});
            skLineSegment(sketch, "E10.21.0.94", {"start": v(150, 318.83) * mm, "end": v(150, 319.83) * mm});
            skLineSegment(sketch, "E10.24.0.94", {"start": v(140, 318.83) * mm, "end": v(140, 319.83) * mm});
            skLineSegment(sketch, "E10.27.0.94", {"start": v(-140, 318.83) * mm, "end": v(-140, 319.83) * mm});
            skLineSegment(sketch, "E10.30.0.94", {"start": v(-150, 319.83) * mm, "end": v(-150, 318.83) * mm});
            skLineSegment(sketch, "E10.33.0.94", {"start": v(-430, 319.83) * mm, "end": v(-430, 318.83) * mm});
            skLineSegment(sketch, "E10.0.0.95", {"start": v(150, 322.83) * mm, "end": v(430, 322.83) * mm});
            skLineSegment(sketch, "E10.3.0.95", {"start": v(-140, 322.83) * mm, "end": v(140, 322.83) * mm});
            skLineSegment(sketch, "E10.6.0.95", {"start": v(-430, 321.83) * mm, "end": v(-150, 321.83) * mm});
            skLineSegment(sketch, "E10.9.0.95", {"start": v(150, 321.83) * mm, "end": v(430, 321.83) * mm});
            skLineSegment(sketch, "E10.12.0.95", {"start": v(-140, 321.83) * mm, "end": v(140, 321.83) * mm});
            skLineSegment(sketch, "E10.15.0.95", {"start": v(-430, 322.83) * mm, "end": v(-150, 322.83) * mm});
            skLineSegment(sketch, "E10.18.0.95", {"start": v(430, 321.83) * mm, "end": v(430, 322.83) * mm});
            skLineSegment(sketch, "E10.21.0.95", {"start": v(150, 321.83) * mm, "end": v(150, 322.83) * mm});
            skLineSegment(sketch, "E10.24.0.95", {"start": v(140, 321.83) * mm, "end": v(140, 322.83) * mm});
            skLineSegment(sketch, "E10.27.0.95", {"start": v(-140, 321.83) * mm, "end": v(-140, 322.83) * mm});
            skLineSegment(sketch, "E10.30.0.95", {"start": v(-150, 322.83) * mm, "end": v(-150, 321.83) * mm});
            skLineSegment(sketch, "E10.33.0.95", {"start": v(-430, 322.83) * mm, "end": v(-430, 321.83) * mm});
            skLineSegment(sketch, "E10.0.0.96", {"start": v(150, 325.83) * mm, "end": v(430, 325.83) * mm});
            skLineSegment(sketch, "E10.3.0.96", {"start": v(-140, 325.83) * mm, "end": v(140, 325.83) * mm});
            skLineSegment(sketch, "E10.6.0.96", {"start": v(-430, 324.83) * mm, "end": v(-150, 324.83) * mm});
            skLineSegment(sketch, "E10.9.0.96", {"start": v(150, 324.83) * mm, "end": v(430, 324.83) * mm});
            skLineSegment(sketch, "E10.12.0.96", {"start": v(-140, 324.83) * mm, "end": v(140, 324.83) * mm});
            skLineSegment(sketch, "E10.15.0.96", {"start": v(-430, 325.83) * mm, "end": v(-150, 325.83) * mm});
            skLineSegment(sketch, "E10.18.0.96", {"start": v(430, 324.83) * mm, "end": v(430, 325.83) * mm});
            skLineSegment(sketch, "E10.21.0.96", {"start": v(150, 324.83) * mm, "end": v(150, 325.83) * mm});
            skLineSegment(sketch, "E10.24.0.96", {"start": v(140, 324.83) * mm, "end": v(140, 325.83) * mm});
            skLineSegment(sketch, "E10.27.0.96", {"start": v(-140, 324.83) * mm, "end": v(-140, 325.83) * mm});
            skLineSegment(sketch, "E10.30.0.96", {"start": v(-150, 325.83) * mm, "end": v(-150, 324.83) * mm});
            skLineSegment(sketch, "E10.33.0.96", {"start": v(-430, 325.83) * mm, "end": v(-430, 324.83) * mm});
            skLineSegment(sketch, "E10.0.0.97", {"start": v(150, 328.83) * mm, "end": v(430, 328.83) * mm});
            skLineSegment(sketch, "E10.3.0.97", {"start": v(-140, 328.83) * mm, "end": v(140, 328.83) * mm});
            skLineSegment(sketch, "E10.6.0.97", {"start": v(-430, 327.83) * mm, "end": v(-150, 327.83) * mm});
            skLineSegment(sketch, "E10.9.0.97", {"start": v(150, 327.83) * mm, "end": v(430, 327.83) * mm});
            skLineSegment(sketch, "E10.12.0.97", {"start": v(-140, 327.83) * mm, "end": v(140, 327.83) * mm});
            skLineSegment(sketch, "E10.15.0.97", {"start": v(-430, 328.83) * mm, "end": v(-150, 328.83) * mm});
            skLineSegment(sketch, "E10.18.0.97", {"start": v(430, 327.83) * mm, "end": v(430, 328.83) * mm});
            skLineSegment(sketch, "E10.21.0.97", {"start": v(150, 327.83) * mm, "end": v(150, 328.83) * mm});
            skLineSegment(sketch, "E10.24.0.97", {"start": v(140, 327.83) * mm, "end": v(140, 328.83) * mm});
            skLineSegment(sketch, "E10.27.0.97", {"start": v(-140, 327.83) * mm, "end": v(-140, 328.83) * mm});
            skLineSegment(sketch, "E10.30.0.97", {"start": v(-150, 328.83) * mm, "end": v(-150, 327.83) * mm});
            skLineSegment(sketch, "E10.33.0.97", {"start": v(-430, 328.83) * mm, "end": v(-430, 327.83) * mm});
            skLineSegment(sketch, "E10.0.0.98", {"start": v(150, 331.83) * mm, "end": v(430, 331.83) * mm});
            skLineSegment(sketch, "E10.3.0.98", {"start": v(-140, 331.83) * mm, "end": v(140, 331.83) * mm});
            skLineSegment(sketch, "E10.6.0.98", {"start": v(-430, 330.83) * mm, "end": v(-150, 330.83) * mm});
            skLineSegment(sketch, "E10.9.0.98", {"start": v(150, 330.83) * mm, "end": v(430, 330.83) * mm});
            skLineSegment(sketch, "E10.12.0.98", {"start": v(-140, 330.83) * mm, "end": v(140, 330.83) * mm});
            skLineSegment(sketch, "E10.15.0.98", {"start": v(-430, 331.83) * mm, "end": v(-150, 331.83) * mm});
            skLineSegment(sketch, "E10.18.0.98", {"start": v(430, 330.83) * mm, "end": v(430, 331.83) * mm});
            skLineSegment(sketch, "E10.21.0.98", {"start": v(150, 330.83) * mm, "end": v(150, 331.83) * mm});
            skLineSegment(sketch, "E10.24.0.98", {"start": v(140, 330.83) * mm, "end": v(140, 331.83) * mm});
            skLineSegment(sketch, "E10.27.0.98", {"start": v(-140, 330.83) * mm, "end": v(-140, 331.83) * mm});
            skLineSegment(sketch, "E10.30.0.98", {"start": v(-150, 331.83) * mm, "end": v(-150, 330.83) * mm});
            skLineSegment(sketch, "E10.33.0.98", {"start": v(-430, 331.83) * mm, "end": v(-430, 330.83) * mm});
            skLineSegment(sketch, "E10.0.0.99", {"start": v(150, 334.83) * mm, "end": v(430, 334.83) * mm});
            skLineSegment(sketch, "E10.3.0.99", {"start": v(-140, 334.83) * mm, "end": v(140, 334.83) * mm});
            skLineSegment(sketch, "E10.6.0.99", {"start": v(-430, 333.83) * mm, "end": v(-150, 333.83) * mm});
            skLineSegment(sketch, "E10.9.0.99", {"start": v(150, 333.83) * mm, "end": v(430, 333.83) * mm});
            skLineSegment(sketch, "E10.12.0.99", {"start": v(-140, 333.83) * mm, "end": v(140, 333.83) * mm});
            skLineSegment(sketch, "E10.15.0.99", {"start": v(-430, 334.83) * mm, "end": v(-150, 334.83) * mm});
            skLineSegment(sketch, "E10.18.0.99", {"start": v(430, 333.83) * mm, "end": v(430, 334.83) * mm});
            skLineSegment(sketch, "E10.21.0.99", {"start": v(150, 333.83) * mm, "end": v(150, 334.83) * mm});
            skLineSegment(sketch, "E10.24.0.99", {"start": v(140, 333.83) * mm, "end": v(140, 334.83) * mm});
            skLineSegment(sketch, "E10.27.0.99", {"start": v(-140, 333.83) * mm, "end": v(-140, 334.83) * mm});
            skLineSegment(sketch, "E10.30.0.99", {"start": v(-150, 334.83) * mm, "end": v(-150, 333.83) * mm});
            skLineSegment(sketch, "E10.33.0.99", {"start": v(-430, 334.83) * mm, "end": v(-430, 333.83) * mm});
            skLineSegment(sketch, "E11.0.1.0", {"start": v(-140, 337.83) * mm, "end": v(140, 337.83) * mm});
            skLineSegment(sketch, "E11.0.1.1", {"start": v(-140, 336.83) * mm, "end": v(140, 336.83) * mm});
            skLineSegment(sketch, "E11.0.1.2", {"start": v(-140, 336.83) * mm, "end": v(-140, 337.83) * mm});
            skLineSegment(sketch, "E11.0.1.3", {"start": v(140, 336.83) * mm, "end": v(140, 337.83) * mm});
            skLineSegment(sketch, "E11.0.2.0", {"start": v(-140, 340.83) * mm, "end": v(140, 340.83) * mm});
            skLineSegment(sketch, "E11.0.2.1", {"start": v(-140, 339.83) * mm, "end": v(140, 339.83) * mm});
            skLineSegment(sketch, "E11.0.2.2", {"start": v(-140, 339.83) * mm, "end": v(-140, 340.83) * mm});
            skLineSegment(sketch, "E11.0.2.3", {"start": v(140, 339.83) * mm, "end": v(140, 340.83) * mm});
            skLineSegment(sketch, "E11.0.3.0", {"start": v(-140, 343.83) * mm, "end": v(140, 343.83) * mm});
            skLineSegment(sketch, "E11.0.3.1", {"start": v(-140, 342.83) * mm, "end": v(140, 342.83) * mm});
            skLineSegment(sketch, "E11.0.3.2", {"start": v(-140, 342.83) * mm, "end": v(-140, 343.83) * mm});
            skLineSegment(sketch, "E11.0.3.3", {"start": v(140, 342.83) * mm, "end": v(140, 343.83) * mm});
            skLineSegment(sketch, "E11.0.4.0", {"start": v(-140, 346.83) * mm, "end": v(140, 346.83) * mm});
            skLineSegment(sketch, "E11.0.4.1", {"start": v(-140, 345.83) * mm, "end": v(140, 345.83) * mm});
            skLineSegment(sketch, "E11.0.4.2", {"start": v(-140, 345.83) * mm, "end": v(-140, 346.83) * mm});
            skLineSegment(sketch, "E11.0.4.3", {"start": v(140, 345.83) * mm, "end": v(140, 346.83) * mm});
            skLineSegment(sketch, "E11.0.5.0", {"start": v(-140, 349.83) * mm, "end": v(140, 349.83) * mm});
            skLineSegment(sketch, "E11.0.5.1", {"start": v(-140, 348.83) * mm, "end": v(140, 348.83) * mm});
            skLineSegment(sketch, "E11.0.5.2", {"start": v(-140, 348.83) * mm, "end": v(-140, 349.83) * mm});
            skLineSegment(sketch, "E11.0.5.3", {"start": v(140, 348.83) * mm, "end": v(140, 349.83) * mm});
            skLineSegment(sketch, "E11.0.6.0", {"start": v(-140, 352.83) * mm, "end": v(140, 352.83) * mm});
            skLineSegment(sketch, "E11.0.6.1", {"start": v(-140, 351.83) * mm, "end": v(140, 351.83) * mm});
            skLineSegment(sketch, "E11.0.6.2", {"start": v(-140, 351.83) * mm, "end": v(-140, 352.83) * mm});
            skLineSegment(sketch, "E11.0.6.3", {"start": v(140, 351.83) * mm, "end": v(140, 352.83) * mm});
            skLineSegment(sketch, "E11.0.7.0", {"start": v(-140, 355.83) * mm, "end": v(140, 355.83) * mm});
            skLineSegment(sketch, "E11.0.7.1", {"start": v(-140, 354.83) * mm, "end": v(140, 354.83) * mm});
            skLineSegment(sketch, "E11.0.7.2", {"start": v(-140, 354.83) * mm, "end": v(-140, 355.83) * mm});
            skLineSegment(sketch, "E11.0.7.3", {"start": v(140, 354.83) * mm, "end": v(140, 355.83) * mm});
            skLineSegment(sketch, "E11.0.8.0", {"start": v(-140, 358.83) * mm, "end": v(140, 358.83) * mm});
            skLineSegment(sketch, "E11.0.8.1", {"start": v(-140, 357.83) * mm, "end": v(140, 357.83) * mm});
            skLineSegment(sketch, "E11.0.8.2", {"start": v(-140, 357.83) * mm, "end": v(-140, 358.83) * mm});
            skLineSegment(sketch, "E11.0.8.3", {"start": v(140, 357.83) * mm, "end": v(140, 358.83) * mm});
            skLineSegment(sketch, "E11.0.9.0", {"start": v(-140, 361.83) * mm, "end": v(140, 361.83) * mm});
            skLineSegment(sketch, "E11.0.9.1", {"start": v(-140, 360.83) * mm, "end": v(140, 360.83) * mm});
            skLineSegment(sketch, "E11.0.9.2", {"start": v(-140, 360.83) * mm, "end": v(-140, 361.83) * mm});
            skLineSegment(sketch, "E11.0.9.3", {"start": v(140, 360.83) * mm, "end": v(140, 361.83) * mm});
            skLineSegment(sketch, "E11.0.10.0", {"start": v(-140, 364.83) * mm, "end": v(140, 364.83) * mm});
            skLineSegment(sketch, "E11.0.10.1", {"start": v(-140, 363.83) * mm, "end": v(140, 363.83) * mm});
            skLineSegment(sketch, "E11.0.10.2", {"start": v(-140, 363.83) * mm, "end": v(-140, 364.83) * mm});
            skLineSegment(sketch, "E11.0.10.3", {"start": v(140, 363.83) * mm, "end": v(140, 364.83) * mm});
            skLineSegment(sketch, "E11.0.11.0", {"start": v(-140, 367.83) * mm, "end": v(140, 367.83) * mm});
            skLineSegment(sketch, "E11.0.11.1", {"start": v(-140, 366.83) * mm, "end": v(140, 366.83) * mm});
            skLineSegment(sketch, "E11.0.11.2", {"start": v(-140, 366.83) * mm, "end": v(-140, 367.83) * mm});
            skLineSegment(sketch, "E11.0.11.3", {"start": v(140, 366.83) * mm, "end": v(140, 367.83) * mm});
            skLineSegment(sketch, "E11.0.12.0", {"start": v(-140, 370.83) * mm, "end": v(140, 370.83) * mm});
            skLineSegment(sketch, "E11.0.12.1", {"start": v(-140, 369.83) * mm, "end": v(140, 369.83) * mm});
            skLineSegment(sketch, "E11.0.12.2", {"start": v(-140, 369.83) * mm, "end": v(-140, 370.83) * mm});
            skLineSegment(sketch, "E11.0.12.3", {"start": v(140, 369.83) * mm, "end": v(140, 370.83) * mm});
            skLineSegment(sketch, "E11.0.13.0", {"start": v(-140, 373.83) * mm, "end": v(140, 373.83) * mm});
            skLineSegment(sketch, "E11.0.13.1", {"start": v(-140, 372.83) * mm, "end": v(140, 372.83) * mm});
            skLineSegment(sketch, "E11.0.13.2", {"start": v(-140, 372.83) * mm, "end": v(-140, 373.83) * mm});
            skLineSegment(sketch, "E11.0.13.3", {"start": v(140, 372.83) * mm, "end": v(140, 373.83) * mm});
            skLineSegment(sketch, "E11.0.14.0", {"start": v(-140, 376.83) * mm, "end": v(140, 376.83) * mm});
            skLineSegment(sketch, "E11.0.14.1", {"start": v(-140, 375.83) * mm, "end": v(140, 375.83) * mm});
            skLineSegment(sketch, "E11.0.14.2", {"start": v(-140, 375.83) * mm, "end": v(-140, 376.83) * mm});
            skLineSegment(sketch, "E11.0.14.3", {"start": v(140, 375.83) * mm, "end": v(140, 376.83) * mm});
            skLineSegment(sketch, "E11.0.15.0", {"start": v(-140, 379.83) * mm, "end": v(140, 379.83) * mm});
            skLineSegment(sketch, "E11.0.15.1", {"start": v(-140, 378.83) * mm, "end": v(140, 378.83) * mm});
            skLineSegment(sketch, "E11.0.15.2", {"start": v(-140, 378.83) * mm, "end": v(-140, 379.83) * mm});
            skLineSegment(sketch, "E11.0.15.3", {"start": v(140, 378.83) * mm, "end": v(140, 379.83) * mm});
            skLineSegment(sketch, "E11.0.16.0", {"start": v(-140, 382.83) * mm, "end": v(140, 382.83) * mm});
            skLineSegment(sketch, "E11.0.16.1", {"start": v(-140, 381.83) * mm, "end": v(140, 381.83) * mm});
            skLineSegment(sketch, "E11.0.16.2", {"start": v(-140, 381.83) * mm, "end": v(-140, 382.83) * mm});
            skLineSegment(sketch, "E11.0.16.3", {"start": v(140, 381.83) * mm, "end": v(140, 382.83) * mm});
            skLineSegment(sketch, "E11.0.17.0", {"start": v(-140, 385.83) * mm, "end": v(140, 385.83) * mm});
            skLineSegment(sketch, "E11.0.17.1", {"start": v(-140, 384.83) * mm, "end": v(140, 384.83) * mm});
            skLineSegment(sketch, "E11.0.17.2", {"start": v(-140, 384.83) * mm, "end": v(-140, 385.83) * mm});
            skLineSegment(sketch, "E11.0.17.3", {"start": v(140, 384.83) * mm, "end": v(140, 385.83) * mm});
            skLineSegment(sketch, "E11.0.18.0", {"start": v(-140, 388.83) * mm, "end": v(140, 388.83) * mm});
            skLineSegment(sketch, "E11.0.18.1", {"start": v(-140, 387.83) * mm, "end": v(140, 387.83) * mm});
            skLineSegment(sketch, "E11.0.18.2", {"start": v(-140, 387.83) * mm, "end": v(-140, 388.83) * mm});
            skLineSegment(sketch, "E11.0.18.3", {"start": v(140, 387.83) * mm, "end": v(140, 388.83) * mm});
            skLineSegment(sketch, "E11.0.19.0", {"start": v(-140, 391.83) * mm, "end": v(140, 391.83) * mm});
            skLineSegment(sketch, "E11.0.19.1", {"start": v(-140, 390.83) * mm, "end": v(140, 390.83) * mm});
            skLineSegment(sketch, "E11.0.19.2", {"start": v(-140, 390.83) * mm, "end": v(-140, 391.83) * mm});
            skLineSegment(sketch, "E11.0.19.3", {"start": v(140, 390.83) * mm, "end": v(140, 391.83) * mm});
            skLineSegment(sketch, "E11.0.20.0", {"start": v(-140, 394.83) * mm, "end": v(140, 394.83) * mm});
            skLineSegment(sketch, "E11.0.20.1", {"start": v(-140, 393.83) * mm, "end": v(140, 393.83) * mm});
            skLineSegment(sketch, "E11.0.20.2", {"start": v(-140, 393.83) * mm, "end": v(-140, 394.83) * mm});
            skLineSegment(sketch, "E11.0.20.3", {"start": v(140, 393.83) * mm, "end": v(140, 394.83) * mm});
            skLineSegment(sketch, "E11.0.21.0", {"start": v(-140, 397.83) * mm, "end": v(140, 397.83) * mm});
            skLineSegment(sketch, "E11.0.21.1", {"start": v(-140, 396.83) * mm, "end": v(140, 396.83) * mm});
            skLineSegment(sketch, "E11.0.21.2", {"start": v(-140, 396.83) * mm, "end": v(-140, 397.83) * mm});
            skLineSegment(sketch, "E11.0.21.3", {"start": v(140, 396.83) * mm, "end": v(140, 397.83) * mm});
            skLineSegment(sketch, "E11.0.22.0", {"start": v(-140, 400.83) * mm, "end": v(140, 400.83) * mm});
            skLineSegment(sketch, "E11.0.22.1", {"start": v(-140, 399.83) * mm, "end": v(140, 399.83) * mm});
            skLineSegment(sketch, "E11.0.22.2", {"start": v(-140, 399.83) * mm, "end": v(-140, 400.83) * mm});
            skLineSegment(sketch, "E11.0.22.3", {"start": v(140, 399.83) * mm, "end": v(140, 400.83) * mm});
            skLineSegment(sketch, "E11.0.23.0", {"start": v(-140, 403.83) * mm, "end": v(140, 403.83) * mm});
            skLineSegment(sketch, "E11.0.23.1", {"start": v(-140, 402.83) * mm, "end": v(140, 402.83) * mm});
            skLineSegment(sketch, "E11.0.23.2", {"start": v(-140, 402.83) * mm, "end": v(-140, 403.83) * mm});
            skLineSegment(sketch, "E11.0.23.3", {"start": v(140, 402.83) * mm, "end": v(140, 403.83) * mm});
            skLineSegment(sketch, "E11.0.24.0", {"start": v(-140, 406.83) * mm, "end": v(140, 406.83) * mm});
            skLineSegment(sketch, "E11.0.24.1", {"start": v(-140, 405.83) * mm, "end": v(140, 405.83) * mm});
            skLineSegment(sketch, "E11.0.24.2", {"start": v(-140, 405.83) * mm, "end": v(-140, 406.83) * mm});
            skLineSegment(sketch, "E11.0.24.3", {"start": v(140, 405.83) * mm, "end": v(140, 406.83) * mm});
            skLineSegment(sketch, "E11.0.25.0", {"start": v(-140, 409.83) * mm, "end": v(140, 409.83) * mm});
            skLineSegment(sketch, "E11.0.25.1", {"start": v(-140, 408.83) * mm, "end": v(140, 408.83) * mm});
            skLineSegment(sketch, "E11.0.25.2", {"start": v(-140, 408.83) * mm, "end": v(-140, 409.83) * mm});
            skLineSegment(sketch, "E11.0.25.3", {"start": v(140, 408.83) * mm, "end": v(140, 409.83) * mm});
            skLineSegment(sketch, "E11.0.26.0", {"start": v(-140, 412.83) * mm, "end": v(140, 412.83) * mm});
            skLineSegment(sketch, "E11.0.26.1", {"start": v(-140, 411.83) * mm, "end": v(140, 411.83) * mm});
            skLineSegment(sketch, "E11.0.26.2", {"start": v(-140, 411.83) * mm, "end": v(-140, 412.83) * mm});
            skLineSegment(sketch, "E11.0.26.3", {"start": v(140, 411.83) * mm, "end": v(140, 412.83) * mm});
            skLineSegment(sketch, "E11.0.27.0", {"start": v(-140, 415.83) * mm, "end": v(140, 415.83) * mm});
            skLineSegment(sketch, "E11.0.27.1", {"start": v(-140, 414.83) * mm, "end": v(140, 414.83) * mm});
            skLineSegment(sketch, "E11.0.27.2", {"start": v(-140, 414.83) * mm, "end": v(-140, 415.83) * mm});
            skLineSegment(sketch, "E11.0.27.3", {"start": v(140, 414.83) * mm, "end": v(140, 415.83) * mm});
            skLineSegment(sketch, "E11.0.28.0", {"start": v(-140, 418.83) * mm, "end": v(140, 418.83) * mm});
            skLineSegment(sketch, "E11.0.28.1", {"start": v(-140, 417.83) * mm, "end": v(140, 417.83) * mm});
            skLineSegment(sketch, "E11.0.28.2", {"start": v(-140, 417.83) * mm, "end": v(-140, 418.83) * mm});
            skLineSegment(sketch, "E11.0.28.3", {"start": v(140, 417.83) * mm, "end": v(140, 418.83) * mm});
            skLineSegment(sketch, "E11.0.29.0", {"start": v(-140, 421.83) * mm, "end": v(140, 421.83) * mm});
            skLineSegment(sketch, "E11.0.29.1", {"start": v(-140, 420.83) * mm, "end": v(140, 420.83) * mm});
            skLineSegment(sketch, "E11.0.29.2", {"start": v(-140, 420.83) * mm, "end": v(-140, 421.83) * mm});
            skLineSegment(sketch, "E11.0.29.3", {"start": v(140, 420.83) * mm, "end": v(140, 421.83) * mm});
            skLineSegment(sketch, "E11.0.30.0", {"start": v(-140, 424.83) * mm, "end": v(140, 424.83) * mm});
            skLineSegment(sketch, "E11.0.30.1", {"start": v(-140, 423.83) * mm, "end": v(140, 423.83) * mm});
            skLineSegment(sketch, "E11.0.30.2", {"start": v(-140, 423.83) * mm, "end": v(-140, 424.83) * mm});
            skLineSegment(sketch, "E11.0.30.3", {"start": v(140, 423.83) * mm, "end": v(140, 424.83) * mm});
            skLineSegment(sketch, "E11.0.31.0", {"start": v(-140, 427.83) * mm, "end": v(140, 427.83) * mm});
            skLineSegment(sketch, "E11.0.31.1", {"start": v(-140, 426.83) * mm, "end": v(140, 426.83) * mm});
            skLineSegment(sketch, "E11.0.31.2", {"start": v(-140, 426.83) * mm, "end": v(-140, 427.83) * mm});
            skLineSegment(sketch, "E11.0.31.3", {"start": v(140, 426.83) * mm, "end": v(140, 427.83) * mm});
            skLineSegment(sketch, "E11.0.32.0", {"start": v(-140, 430.83) * mm, "end": v(140, 430.83) * mm});
            skLineSegment(sketch, "E11.0.32.1", {"start": v(-140, 429.83) * mm, "end": v(140, 429.83) * mm});
            skLineSegment(sketch, "E11.0.32.2", {"start": v(-140, 429.83) * mm, "end": v(-140, 430.83) * mm});
            skLineSegment(sketch, "E11.0.32.3", {"start": v(140, 429.83) * mm, "end": v(140, 430.83) * mm});
            skLineSegment(sketch, "E11.0.33.0", {"start": v(-140, 433.83) * mm, "end": v(140, 433.83) * mm});
            skLineSegment(sketch, "E11.0.33.1", {"start": v(-140, 432.83) * mm, "end": v(140, 432.83) * mm});
            skLineSegment(sketch, "E11.0.33.2", {"start": v(-140, 432.83) * mm, "end": v(-140, 433.83) * mm});
            skLineSegment(sketch, "E11.0.33.3", {"start": v(140, 432.83) * mm, "end": v(140, 433.83) * mm});
            skLineSegment(sketch, "E11.0.34.0", {"start": v(-140, 436.83) * mm, "end": v(140, 436.83) * mm});
            skLineSegment(sketch, "E11.0.34.1", {"start": v(-140, 435.83) * mm, "end": v(140, 435.83) * mm});
            skLineSegment(sketch, "E11.0.34.2", {"start": v(-140, 435.83) * mm, "end": v(-140, 436.83) * mm});
            skLineSegment(sketch, "E11.0.34.3", {"start": v(140, 435.83) * mm, "end": v(140, 436.83) * mm});
            skLineSegment(sketch, "E11.direction1", {"start": v(-140, 333.83) * mm, "end": v(-115, 333.83) * mm, "construction": true});
            skLineSegment(sketch, "E11.direction2", {"start": v(-140, 333.83) * mm, "end": v(-140, 336.83) * mm, "construction": true});
            skLineSegment(sketch, "E12.0.1.0", {"start": v(150, 336.83) * mm, "end": v(150, 337.83) * mm});
            skLineSegment(sketch, "E12.0.1.1", {"start": v(150, 337.83) * mm, "end": v(430, 337.83) * mm});
            skLineSegment(sketch, "E12.0.1.2", {"start": v(150, 336.83) * mm, "end": v(430, 336.83) * mm});
            skLineSegment(sketch, "E12.0.2.0", {"start": v(150, 339.83) * mm, "end": v(150, 340.83) * mm});
            skLineSegment(sketch, "E12.0.2.1", {"start": v(150, 340.83) * mm, "end": v(430, 340.83) * mm});
            skLineSegment(sketch, "E12.0.2.2", {"start": v(150, 339.83) * mm, "end": v(430, 339.83) * mm});
            skLineSegment(sketch, "E12.0.3.0", {"start": v(150, 342.83) * mm, "end": v(150, 343.83) * mm});
            skLineSegment(sketch, "E12.0.3.1", {"start": v(150, 343.83) * mm, "end": v(430, 343.83) * mm});
            skLineSegment(sketch, "E12.0.3.2", {"start": v(150, 342.83) * mm, "end": v(430, 342.83) * mm});
            skLineSegment(sketch, "E12.0.4.0", {"start": v(150, 345.83) * mm, "end": v(150, 346.83) * mm});
            skLineSegment(sketch, "E12.0.4.1", {"start": v(150, 346.83) * mm, "end": v(430, 346.83) * mm});
            skLineSegment(sketch, "E12.0.4.2", {"start": v(150, 345.83) * mm, "end": v(430, 345.83) * mm});
            skLineSegment(sketch, "E12.0.5.0", {"start": v(150, 348.83) * mm, "end": v(150, 349.83) * mm});
            skLineSegment(sketch, "E12.0.5.1", {"start": v(150, 349.83) * mm, "end": v(430, 349.83) * mm});
            skLineSegment(sketch, "E12.0.5.2", {"start": v(150, 348.83) * mm, "end": v(430, 348.83) * mm});
            skLineSegment(sketch, "E12.0.6.0", {"start": v(150, 351.83) * mm, "end": v(150, 352.83) * mm});
            skLineSegment(sketch, "E12.0.6.1", {"start": v(150, 352.83) * mm, "end": v(430, 352.83) * mm});
            skLineSegment(sketch, "E12.0.6.2", {"start": v(150, 351.83) * mm, "end": v(430, 351.83) * mm});
            skLineSegment(sketch, "E12.0.7.0", {"start": v(150, 354.83) * mm, "end": v(150, 355.83) * mm});
            skLineSegment(sketch, "E12.0.7.1", {"start": v(150, 355.83) * mm, "end": v(430, 355.83) * mm});
            skLineSegment(sketch, "E12.0.7.2", {"start": v(150, 354.83) * mm, "end": v(430, 354.83) * mm});
            skLineSegment(sketch, "E12.0.8.0", {"start": v(150, 357.83) * mm, "end": v(150, 358.83) * mm});
            skLineSegment(sketch, "E12.0.8.1", {"start": v(150, 358.83) * mm, "end": v(430, 358.83) * mm});
            skLineSegment(sketch, "E12.0.8.2", {"start": v(150, 357.83) * mm, "end": v(430, 357.83) * mm});
            skLineSegment(sketch, "E12.0.9.0", {"start": v(150, 360.83) * mm, "end": v(150, 361.83) * mm});
            skLineSegment(sketch, "E12.0.9.1", {"start": v(150, 361.83) * mm, "end": v(430, 361.83) * mm});
            skLineSegment(sketch, "E12.0.9.2", {"start": v(150, 360.83) * mm, "end": v(430, 360.83) * mm});
            skLineSegment(sketch, "E12.0.10.0", {"start": v(150, 363.83) * mm, "end": v(150, 364.83) * mm});
            skLineSegment(sketch, "E12.0.10.1", {"start": v(150, 364.83) * mm, "end": v(430, 364.83) * mm});
            skLineSegment(sketch, "E12.0.10.2", {"start": v(150, 363.83) * mm, "end": v(430, 363.83) * mm});
            skLineSegment(sketch, "E12.0.11.0", {"start": v(150, 366.83) * mm, "end": v(150, 367.83) * mm});
            skLineSegment(sketch, "E12.0.11.1", {"start": v(150, 367.83) * mm, "end": v(430, 367.83) * mm});
            skLineSegment(sketch, "E12.0.11.2", {"start": v(150, 366.83) * mm, "end": v(430, 366.83) * mm});
            skLineSegment(sketch, "E12.0.12.0", {"start": v(150, 369.83) * mm, "end": v(150, 370.83) * mm});
            skLineSegment(sketch, "E12.0.12.1", {"start": v(150, 370.83) * mm, "end": v(430, 370.83) * mm});
            skLineSegment(sketch, "E12.0.12.2", {"start": v(150, 369.83) * mm, "end": v(430, 369.83) * mm});
            skLineSegment(sketch, "E12.0.13.0", {"start": v(150, 372.83) * mm, "end": v(150, 373.83) * mm});
            skLineSegment(sketch, "E12.0.13.1", {"start": v(150, 373.83) * mm, "end": v(430, 373.83) * mm});
            skLineSegment(sketch, "E12.0.13.2", {"start": v(150, 372.83) * mm, "end": v(430, 372.83) * mm});
            skLineSegment(sketch, "E12.0.14.0", {"start": v(150, 375.83) * mm, "end": v(150, 376.83) * mm});
            skLineSegment(sketch, "E12.0.14.1", {"start": v(150, 376.83) * mm, "end": v(430, 376.83) * mm});
            skLineSegment(sketch, "E12.0.14.2", {"start": v(150, 375.83) * mm, "end": v(430, 375.83) * mm});
            skLineSegment(sketch, "E12.0.15.0", {"start": v(150, 378.83) * mm, "end": v(150, 379.83) * mm});
            skLineSegment(sketch, "E12.0.15.1", {"start": v(150, 379.83) * mm, "end": v(430, 379.83) * mm});
            skLineSegment(sketch, "E12.0.15.2", {"start": v(150, 378.83) * mm, "end": v(430, 378.83) * mm});
            skLineSegment(sketch, "E12.0.16.0", {"start": v(150, 381.83) * mm, "end": v(150, 382.83) * mm});
            skLineSegment(sketch, "E12.0.16.1", {"start": v(150, 382.83) * mm, "end": v(430, 382.83) * mm});
            skLineSegment(sketch, "E12.0.16.2", {"start": v(150, 381.83) * mm, "end": v(430, 381.83) * mm});
            skLineSegment(sketch, "E12.0.17.0", {"start": v(150, 384.83) * mm, "end": v(150, 385.83) * mm});
            skLineSegment(sketch, "E12.0.17.1", {"start": v(150, 385.83) * mm, "end": v(430, 385.83) * mm});
            skLineSegment(sketch, "E12.0.17.2", {"start": v(150, 384.83) * mm, "end": v(430, 384.83) * mm});
            skLineSegment(sketch, "E12.0.18.0", {"start": v(150, 387.83) * mm, "end": v(150, 388.83) * mm});
            skLineSegment(sketch, "E12.0.18.1", {"start": v(150, 388.83) * mm, "end": v(430, 388.83) * mm});
            skLineSegment(sketch, "E12.0.18.2", {"start": v(150, 387.83) * mm, "end": v(430, 387.83) * mm});
            skLineSegment(sketch, "E12.0.19.0", {"start": v(150, 390.83) * mm, "end": v(150, 391.83) * mm});
            skLineSegment(sketch, "E12.0.19.1", {"start": v(150, 391.83) * mm, "end": v(430, 391.83) * mm});
            skLineSegment(sketch, "E12.0.19.2", {"start": v(150, 390.83) * mm, "end": v(430, 390.83) * mm});
            skLineSegment(sketch, "E12.0.20.0", {"start": v(150, 393.83) * mm, "end": v(150, 394.83) * mm});
            skLineSegment(sketch, "E12.0.20.1", {"start": v(150, 394.83) * mm, "end": v(430, 394.83) * mm});
            skLineSegment(sketch, "E12.0.20.2", {"start": v(150, 393.83) * mm, "end": v(430, 393.83) * mm});
            skLineSegment(sketch, "E12.0.21.0", {"start": v(150, 396.83) * mm, "end": v(150, 397.83) * mm});
            skLineSegment(sketch, "E12.0.21.1", {"start": v(150, 397.83) * mm, "end": v(430, 397.83) * mm});
            skLineSegment(sketch, "E12.0.21.2", {"start": v(150, 396.83) * mm, "end": v(430, 396.83) * mm});
            skLineSegment(sketch, "E12.0.22.0", {"start": v(150, 399.83) * mm, "end": v(150, 400.83) * mm});
            skLineSegment(sketch, "E12.0.22.1", {"start": v(150, 400.83) * mm, "end": v(430, 400.83) * mm});
            skLineSegment(sketch, "E12.0.22.2", {"start": v(150, 399.83) * mm, "end": v(430, 399.83) * mm});
            skLineSegment(sketch, "E12.0.23.0", {"start": v(150, 402.83) * mm, "end": v(150, 403.83) * mm});
            skLineSegment(sketch, "E12.0.23.1", {"start": v(150, 403.83) * mm, "end": v(430, 403.83) * mm});
            skLineSegment(sketch, "E12.0.23.2", {"start": v(150, 402.83) * mm, "end": v(430, 402.83) * mm});
            skLineSegment(sketch, "E12.0.24.0", {"start": v(150, 405.83) * mm, "end": v(150, 406.83) * mm});
            skLineSegment(sketch, "E12.0.24.1", {"start": v(150, 406.83) * mm, "end": v(430, 406.83) * mm});
            skLineSegment(sketch, "E12.0.24.2", {"start": v(150, 405.83) * mm, "end": v(430, 405.83) * mm});
            skLineSegment(sketch, "E12.direction1", {"start": v(150, 333.83) * mm, "end": v(175, 333.83) * mm, "construction": true});
            skLineSegment(sketch, "E12.direction2", {"start": v(150, 333.83) * mm, "end": v(150, 336.83) * mm, "construction": true});
            skLineSegment(sketch, "E13.0.1.0", {"start": v(-430, 337.83) * mm, "end": v(-150, 337.83) * mm});
            skLineSegment(sketch, "E13.0.1.1", {"start": v(-150, 337.83) * mm, "end": v(-150, 336.83) * mm});
            skLineSegment(sketch, "E13.0.1.2", {"start": v(-430, 336.83) * mm, "end": v(-150, 336.83) * mm});
            skLineSegment(sketch, "E13.0.2.0", {"start": v(-430, 340.83) * mm, "end": v(-150, 340.83) * mm});
            skLineSegment(sketch, "E13.0.2.1", {"start": v(-150, 340.83) * mm, "end": v(-150, 339.83) * mm});
            skLineSegment(sketch, "E13.0.2.2", {"start": v(-430, 339.83) * mm, "end": v(-150, 339.83) * mm});
            skLineSegment(sketch, "E13.0.3.0", {"start": v(-430, 343.83) * mm, "end": v(-150, 343.83) * mm});
            skLineSegment(sketch, "E13.0.3.1", {"start": v(-150, 343.83) * mm, "end": v(-150, 342.83) * mm});
            skLineSegment(sketch, "E13.0.3.2", {"start": v(-430, 342.83) * mm, "end": v(-150, 342.83) * mm});
            skLineSegment(sketch, "E13.0.4.0", {"start": v(-430, 346.83) * mm, "end": v(-150, 346.83) * mm});
            skLineSegment(sketch, "E13.0.4.1", {"start": v(-150, 346.83) * mm, "end": v(-150, 345.83) * mm});
            skLineSegment(sketch, "E13.0.4.2", {"start": v(-430, 345.83) * mm, "end": v(-150, 345.83) * mm});
            skLineSegment(sketch, "E13.0.5.0", {"start": v(-430, 349.83) * mm, "end": v(-150, 349.83) * mm});
            skLineSegment(sketch, "E13.0.5.1", {"start": v(-150, 349.83) * mm, "end": v(-150, 348.83) * mm});
            skLineSegment(sketch, "E13.0.5.2", {"start": v(-430, 348.83) * mm, "end": v(-150, 348.83) * mm});
            skLineSegment(sketch, "E13.0.6.0", {"start": v(-430, 352.83) * mm, "end": v(-150, 352.83) * mm});
            skLineSegment(sketch, "E13.0.6.1", {"start": v(-150, 352.83) * mm, "end": v(-150, 351.83) * mm});
            skLineSegment(sketch, "E13.0.6.2", {"start": v(-430, 351.83) * mm, "end": v(-150, 351.83) * mm});
            skLineSegment(sketch, "E13.0.7.0", {"start": v(-430, 355.83) * mm, "end": v(-150, 355.83) * mm});
            skLineSegment(sketch, "E13.0.7.1", {"start": v(-150, 355.83) * mm, "end": v(-150, 354.83) * mm});
            skLineSegment(sketch, "E13.0.7.2", {"start": v(-430, 354.83) * mm, "end": v(-150, 354.83) * mm});
            skLineSegment(sketch, "E13.0.8.0", {"start": v(-430, 358.83) * mm, "end": v(-150, 358.83) * mm});
            skLineSegment(sketch, "E13.0.8.1", {"start": v(-150, 358.83) * mm, "end": v(-150, 357.83) * mm});
            skLineSegment(sketch, "E13.0.8.2", {"start": v(-430, 357.83) * mm, "end": v(-150, 357.83) * mm});
            skLineSegment(sketch, "E13.0.9.0", {"start": v(-430, 361.83) * mm, "end": v(-150, 361.83) * mm});
            skLineSegment(sketch, "E13.0.9.1", {"start": v(-150, 361.83) * mm, "end": v(-150, 360.83) * mm});
            skLineSegment(sketch, "E13.0.9.2", {"start": v(-430, 360.83) * mm, "end": v(-150, 360.83) * mm});
            skLineSegment(sketch, "E13.0.10.0", {"start": v(-430, 364.83) * mm, "end": v(-150, 364.83) * mm});
            skLineSegment(sketch, "E13.0.10.1", {"start": v(-150, 364.83) * mm, "end": v(-150, 363.83) * mm});
            skLineSegment(sketch, "E13.0.10.2", {"start": v(-430, 363.83) * mm, "end": v(-150, 363.83) * mm});
            skLineSegment(sketch, "E13.0.11.0", {"start": v(-430, 367.83) * mm, "end": v(-150, 367.83) * mm});
            skLineSegment(sketch, "E13.0.11.1", {"start": v(-150, 367.83) * mm, "end": v(-150, 366.83) * mm});
            skLineSegment(sketch, "E13.0.11.2", {"start": v(-430, 366.83) * mm, "end": v(-150, 366.83) * mm});
            skLineSegment(sketch, "E13.0.12.0", {"start": v(-430, 370.83) * mm, "end": v(-150, 370.83) * mm});
            skLineSegment(sketch, "E13.0.12.1", {"start": v(-150, 370.83) * mm, "end": v(-150, 369.83) * mm});
            skLineSegment(sketch, "E13.0.12.2", {"start": v(-430, 369.83) * mm, "end": v(-150, 369.83) * mm});
            skLineSegment(sketch, "E13.0.13.0", {"start": v(-430, 373.83) * mm, "end": v(-150, 373.83) * mm});
            skLineSegment(sketch, "E13.0.13.1", {"start": v(-150, 373.83) * mm, "end": v(-150, 372.83) * mm});
            skLineSegment(sketch, "E13.0.13.2", {"start": v(-430, 372.83) * mm, "end": v(-150, 372.83) * mm});
            skLineSegment(sketch, "E13.0.14.0", {"start": v(-430, 376.83) * mm, "end": v(-150, 376.83) * mm});
            skLineSegment(sketch, "E13.0.14.1", {"start": v(-150, 376.83) * mm, "end": v(-150, 375.83) * mm});
            skLineSegment(sketch, "E13.0.14.2", {"start": v(-430, 375.83) * mm, "end": v(-150, 375.83) * mm});
            skLineSegment(sketch, "E13.0.15.0", {"start": v(-430, 379.83) * mm, "end": v(-150, 379.83) * mm});
            skLineSegment(sketch, "E13.0.15.1", {"start": v(-150, 379.83) * mm, "end": v(-150, 378.83) * mm});
            skLineSegment(sketch, "E13.0.15.2", {"start": v(-430, 378.83) * mm, "end": v(-150, 378.83) * mm});
            skLineSegment(sketch, "E13.0.16.0", {"start": v(-430, 382.83) * mm, "end": v(-150, 382.83) * mm});
            skLineSegment(sketch, "E13.0.16.1", {"start": v(-150, 382.83) * mm, "end": v(-150, 381.83) * mm});
            skLineSegment(sketch, "E13.0.16.2", {"start": v(-430, 381.83) * mm, "end": v(-150, 381.83) * mm});
            skLineSegment(sketch, "E13.0.17.0", {"start": v(-430, 385.83) * mm, "end": v(-150, 385.83) * mm});
            skLineSegment(sketch, "E13.0.17.1", {"start": v(-150, 385.83) * mm, "end": v(-150, 384.83) * mm});
            skLineSegment(sketch, "E13.0.17.2", {"start": v(-430, 384.83) * mm, "end": v(-150, 384.83) * mm});
            skLineSegment(sketch, "E13.0.18.0", {"start": v(-430, 388.83) * mm, "end": v(-150, 388.83) * mm});
            skLineSegment(sketch, "E13.0.18.1", {"start": v(-150, 388.83) * mm, "end": v(-150, 387.83) * mm});
            skLineSegment(sketch, "E13.0.18.2", {"start": v(-430, 387.83) * mm, "end": v(-150, 387.83) * mm});
            skLineSegment(sketch, "E13.0.19.0", {"start": v(-430, 391.83) * mm, "end": v(-150, 391.83) * mm});
            skLineSegment(sketch, "E13.0.19.1", {"start": v(-150, 391.83) * mm, "end": v(-150, 390.83) * mm});
            skLineSegment(sketch, "E13.0.19.2", {"start": v(-430, 390.83) * mm, "end": v(-150, 390.83) * mm});
            skLineSegment(sketch, "E13.0.20.0", {"start": v(-430, 394.83) * mm, "end": v(-150, 394.83) * mm});
            skLineSegment(sketch, "E13.0.20.1", {"start": v(-150, 394.83) * mm, "end": v(-150, 393.83) * mm});
            skLineSegment(sketch, "E13.0.20.2", {"start": v(-430, 393.83) * mm, "end": v(-150, 393.83) * mm});
            skLineSegment(sketch, "E13.0.21.0", {"start": v(-430, 397.83) * mm, "end": v(-150, 397.83) * mm});
            skLineSegment(sketch, "E13.0.21.1", {"start": v(-150, 397.83) * mm, "end": v(-150, 396.83) * mm});
            skLineSegment(sketch, "E13.0.21.2", {"start": v(-430, 396.83) * mm, "end": v(-150, 396.83) * mm});
            skLineSegment(sketch, "E13.0.22.0", {"start": v(-430, 400.83) * mm, "end": v(-150, 400.83) * mm});
            skLineSegment(sketch, "E13.0.22.1", {"start": v(-150, 400.83) * mm, "end": v(-150, 399.83) * mm});
            skLineSegment(sketch, "E13.0.22.2", {"start": v(-430, 399.83) * mm, "end": v(-150, 399.83) * mm});
            skLineSegment(sketch, "E13.0.23.0", {"start": v(-430, 403.83) * mm, "end": v(-150, 403.83) * mm});
            skLineSegment(sketch, "E13.0.23.1", {"start": v(-150, 403.83) * mm, "end": v(-150, 402.83) * mm});
            skLineSegment(sketch, "E13.0.23.2", {"start": v(-430, 402.83) * mm, "end": v(-150, 402.83) * mm});
            skLineSegment(sketch, "E13.0.24.0", {"start": v(-430, 406.83) * mm, "end": v(-150, 406.83) * mm});
            skLineSegment(sketch, "E13.0.24.1", {"start": v(-150, 406.83) * mm, "end": v(-150, 405.83) * mm});
            skLineSegment(sketch, "E13.0.24.2", {"start": v(-430, 405.83) * mm, "end": v(-150, 405.83) * mm});
            skLineSegment(sketch, "E13.direction1", {"start": v(-430, 333.83) * mm, "end": v(-405, 333.83) * mm, "construction": true});
            skLineSegment(sketch, "E13.direction2", {"start": v(-430, 333.83) * mm, "end": v(-430, 336.83) * mm, "construction": true});
            skPoint(sketch, "E14.orphan", {"position": v(430, 46.83) * mm});
            skLineSegment(sketch, "E15", {"start": v(429.03, 46.83) * mm, "end": v(430, 46.83) * mm});
            skLineSegment(sketch, "E16", {"start": v(430, 46.83) * mm, "end": v(430, 45.83) * mm});
            skLineSegment(sketch, "E17", {"start": v(430, 45.83) * mm, "end": v(429.13, 45.83) * mm});
            skLineSegment(sketch, "E18", {"start": v(429.34, 43.83) * mm, "end": v(430, 43.83) * mm});
            skLineSegment(sketch, "E19", {"start": v(430, 43.83) * mm, "end": v(430, 42.83) * mm});
            skLineSegment(sketch, "E20", {"start": v(430, 42.83) * mm, "end": v(429.44, 42.83) * mm});
            skLineSegment(sketch, "E21", {"start": v(430, 37.83) * mm, "end": v(430, 36.83) * mm});
            skLineSegment(sketch, "E22", {"start": v(429.64, 40.83) * mm, "end": v(430, 40.83) * mm});
            skLineSegment(sketch, "E23", {"start": v(430, 40.83) * mm, "end": v(430, 39.83) * mm});
            skLineSegment(sketch, "E24", {"start": v(430, 39.83) * mm, "end": v(429.73, 39.83) * mm});
            skSolve(sketch);
        }
        {
            var Q0;
            Q0=makeQuery(id+"F5.imprint","IMPRINT",FACE,{"disambiguationData":[TD([[makeQuery(id+"F5.imprint","IMPRINT",EDGE,{"derivedFrom":sQuery(id+"F5.wireOp",EDGE,"E8.bottom")}),1.0]])]});
            var Q1;
            Q1=makeQuery(id+"F5.imprint","IMPRINT",FACE,{"disambiguationData":[TD([[makeQuery(id+"F5.imprint","IMPRINT",EDGE,{"derivedFrom":sQuery(id+"F5.wireOp",EDGE,"E6.bottom")}),1.0]])]});
            extrude(context, id + "F6", {"entities" : qUnion([Q0, Q1]), "operationType" : NewBodyOperationType.INTERSECT, "oppositeDirection" : true, "depth" : 25 * mm, "offsetDistance" : 25 * mm});
        }
    });
